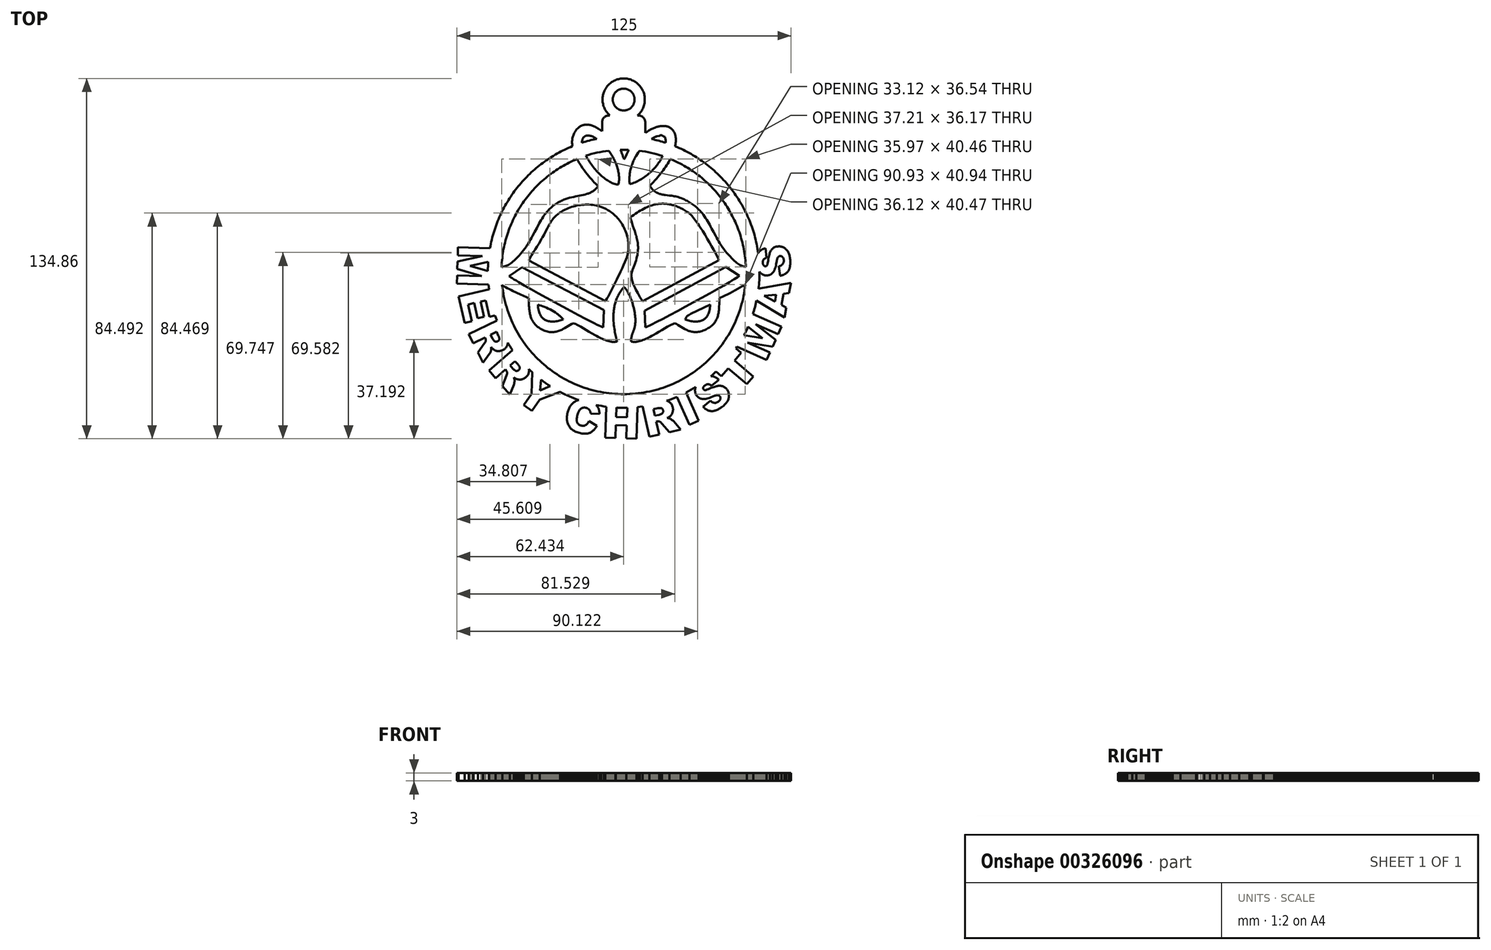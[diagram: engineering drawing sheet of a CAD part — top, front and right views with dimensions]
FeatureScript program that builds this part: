
annotation { "Feature Type Name" : "Feature", "Feature Type Description" : "" }
export const myFeature = defineFeature(function(context is Context, id is Id, definition is map)
    precondition{}
    {
        {
            var Q0;
            Q0=qCreatedBy(makeId("Top.planeOp"),FACE);
            var sketch = newSketch(context, id + "F0", { "sketchPlane" : qUnion([Q0])});
            skLineSegment(sketch, "E0", {"start": v(-50.73, -1.2) * mm, "end": v(-57.52, -2.69) * mm});
            skLineSegment(sketch, "E1", {"start": v(-57.52, -2.69) * mm, "end": v(-50.87, -4.64) * mm});
            skLineSegment(sketch, "E2", {"start": v(-50.87, -4.64) * mm, "end": v(-50.85, -3.77) * mm});
            skLineSegment(sketch, "E3", {"start": v(-50.85, -3.77) * mm, "end": v(-50.83, -2.91) * mm});
            skLineSegment(sketch, "E4", {"start": v(-50.83, -2.91) * mm, "end": v(-50.79, -2.06) * mm});
            skLineSegment(sketch, "E5", {"start": v(-50.79, -2.06) * mm, "end": v(-50.73, -1.2) * mm});
            skLineSegment(sketch, "E6", {"start": v(-0.07, 67.43) * mm, "end": v(0.33, 67.42) * mm});
            skLineSegment(sketch, "E7", {"start": v(0.33, 67.42) * mm, "end": v(0.74, 67.39) * mm});
            skLineSegment(sketch, "E8", {"start": v(0.74, 67.39) * mm, "end": v(1.13, 67.34) * mm});
            skLineSegment(sketch, "E9", {"start": v(1.13, 67.34) * mm, "end": v(1.52, 67.27) * mm});
            skLineSegment(sketch, "E10", {"start": v(1.52, 67.27) * mm, "end": v(1.9, 67.18) * mm});
            skLineSegment(sketch, "E11", {"start": v(1.9, 67.18) * mm, "end": v(2.28, 67.07) * mm});
            skLineSegment(sketch, "E12", {"start": v(2.28, 67.07) * mm, "end": v(2.64, 66.95) * mm});
            skLineSegment(sketch, "E13", {"start": v(2.64, 66.95) * mm, "end": v(3, 66.8) * mm});
            skLineSegment(sketch, "E14", {"start": v(3, 66.8) * mm, "end": v(3.35, 66.65) * mm});
            skLineSegment(sketch, "E15", {"start": v(3.35, 66.65) * mm, "end": v(3.7, 66.47) * mm});
            skLineSegment(sketch, "E16", {"start": v(3.7, 66.47) * mm, "end": v(4.02, 66.28) * mm});
            skLineSegment(sketch, "E17", {"start": v(4.02, 66.28) * mm, "end": v(4.34, 66.08) * mm});
            skLineSegment(sketch, "E18", {"start": v(4.34, 66.08) * mm, "end": v(4.65, 65.86) * mm});
            skLineSegment(sketch, "E19", {"start": v(4.65, 65.86) * mm, "end": v(4.95, 65.62) * mm});
            skLineSegment(sketch, "E20", {"start": v(4.95, 65.62) * mm, "end": v(5.24, 65.38) * mm});
            skLineSegment(sketch, "E21", {"start": v(5.24, 65.38) * mm, "end": v(5.51, 65.11) * mm});
            skLineSegment(sketch, "E22", {"start": v(5.51, 65.11) * mm, "end": v(5.78, 64.84) * mm});
            skLineSegment(sketch, "E23", {"start": v(5.78, 64.84) * mm, "end": v(6.02, 64.55) * mm});
            skLineSegment(sketch, "E24", {"start": v(6.02, 64.55) * mm, "end": v(6.26, 64.25) * mm});
            skLineSegment(sketch, "E25", {"start": v(6.26, 64.25) * mm, "end": v(6.48, 63.94) * mm});
            skLineSegment(sketch, "E26", {"start": v(6.48, 63.94) * mm, "end": v(6.68, 63.62) * mm});
            skLineSegment(sketch, "E27", {"start": v(6.68, 63.62) * mm, "end": v(6.87, 63.3) * mm});
            skLineSegment(sketch, "E28", {"start": v(6.87, 63.3) * mm, "end": v(7.05, 62.95) * mm});
            skLineSegment(sketch, "E29", {"start": v(7.05, 62.95) * mm, "end": v(7.2, 62.6) * mm});
            skLineSegment(sketch, "E30", {"start": v(7.2, 62.6) * mm, "end": v(7.35, 62.24) * mm});
            skLineSegment(sketch, "E31", {"start": v(7.35, 62.24) * mm, "end": v(7.47, 61.88) * mm});
            skLineSegment(sketch, "E32", {"start": v(7.47, 61.88) * mm, "end": v(7.58, 61.5) * mm});
            skLineSegment(sketch, "E33", {"start": v(7.58, 61.5) * mm, "end": v(7.67, 61.12) * mm});
            skLineSegment(sketch, "E34", {"start": v(7.67, 61.12) * mm, "end": v(7.74, 60.73) * mm});
            skLineSegment(sketch, "E35", {"start": v(7.74, 60.73) * mm, "end": v(7.79, 60.33) * mm});
            skLineSegment(sketch, "E36", {"start": v(7.79, 60.33) * mm, "end": v(7.82, 59.93) * mm});
            skLineSegment(sketch, "E37", {"start": v(7.82, 59.93) * mm, "end": v(7.83, 59.53) * mm});
            skLineSegment(sketch, "E38", {"start": v(7.83, 59.53) * mm, "end": v(7.82, 59.09) * mm});
            skLineSegment(sketch, "E39", {"start": v(7.82, 59.09) * mm, "end": v(7.78, 58.65) * mm});
            skLineSegment(sketch, "E40", {"start": v(7.78, 58.65) * mm, "end": v(7.72, 58.22) * mm});
            skLineSegment(sketch, "E41", {"start": v(7.72, 58.22) * mm, "end": v(7.64, 57.8) * mm});
            skLineSegment(sketch, "E42", {"start": v(7.64, 57.8) * mm, "end": v(7.54, 57.39) * mm});
            skLineSegment(sketch, "E43", {"start": v(7.54, 57.39) * mm, "end": v(7.41, 56.99) * mm});
            skLineSegment(sketch, "E44", {"start": v(7.41, 56.99) * mm, "end": v(7.26, 56.6) * mm});
            skLineSegment(sketch, "E45", {"start": v(7.26, 56.6) * mm, "end": v(7.1, 56.2) * mm});
            skLineSegment(sketch, "E46", {"start": v(7.1, 56.2) * mm, "end": v(6.91, 55.83) * mm});
            skLineSegment(sketch, "E47", {"start": v(6.91, 55.83) * mm, "end": v(6.7, 55.47) * mm});
            skLineSegment(sketch, "E48", {"start": v(6.7, 55.47) * mm, "end": v(6.49, 55.12) * mm});
            skLineSegment(sketch, "E49", {"start": v(6.49, 55.12) * mm, "end": v(6.25, 54.79) * mm});
            skLineSegment(sketch, "E50", {"start": v(6.25, 54.79) * mm, "end": v(6, 54.46) * mm});
            skLineSegment(sketch, "E51", {"start": v(6, 54.46) * mm, "end": v(5.72, 54.15) * mm});
            skLineSegment(sketch, "E52", {"start": v(5.72, 54.15) * mm, "end": v(5.43, 53.86) * mm});
            skLineSegment(sketch, "E53", {"start": v(5.43, 53.86) * mm, "end": v(5.13, 53.58) * mm});
            skLineSegment(sketch, "E54", {"start": v(5.13, 53.58) * mm, "end": v(5.46, 53.58) * mm});
            skLineSegment(sketch, "E55", {"start": v(5.46, 53.58) * mm, "end": v(5.72, 53.57) * mm});
            skLineSegment(sketch, "E56", {"start": v(5.72, 53.57) * mm, "end": v(5.97, 53.53) * mm});
            skLineSegment(sketch, "E57", {"start": v(5.97, 53.53) * mm, "end": v(6.22, 53.47) * mm});
            skLineSegment(sketch, "E58", {"start": v(6.22, 53.47) * mm, "end": v(6.45, 53.38) * mm});
            skLineSegment(sketch, "E59", {"start": v(6.45, 53.38) * mm, "end": v(6.67, 53.27) * mm});
            skLineSegment(sketch, "E60", {"start": v(6.67, 53.27) * mm, "end": v(6.88, 53.15) * mm});
            skLineSegment(sketch, "E61", {"start": v(6.88, 53.15) * mm, "end": v(7.08, 53) * mm});
            skLineSegment(sketch, "E62", {"start": v(7.08, 53) * mm, "end": v(7.26, 52.83) * mm});
            skLineSegment(sketch, "E63", {"start": v(7.26, 52.83) * mm, "end": v(7.42, 52.65) * mm});
            skLineSegment(sketch, "E64", {"start": v(7.42, 52.65) * mm, "end": v(7.57, 52.46) * mm});
            skLineSegment(sketch, "E65", {"start": v(7.57, 52.46) * mm, "end": v(7.7, 52.25) * mm});
            skLineSegment(sketch, "E66", {"start": v(7.7, 52.25) * mm, "end": v(7.8, 52.03) * mm});
            skLineSegment(sketch, "E67", {"start": v(7.8, 52.03) * mm, "end": v(7.89, 51.8) * mm});
            skLineSegment(sketch, "E68", {"start": v(7.89, 51.8) * mm, "end": v(7.95, 51.55) * mm});
            skLineSegment(sketch, "E69", {"start": v(7.95, 51.55) * mm, "end": v(8, 51.3) * mm});
            skLineSegment(sketch, "E70", {"start": v(8, 51.3) * mm, "end": v(8, 51.04) * mm});
            skLineSegment(sketch, "E71", {"start": v(8, 51.04) * mm, "end": v(8, 47.03) * mm});
            skLineSegment(sketch, "E72", {"start": v(8, 47.03) * mm, "end": v(8.34, 47.26) * mm});
            skLineSegment(sketch, "E73", {"start": v(8.34, 47.26) * mm, "end": v(8.67, 47.49) * mm});
            skLineSegment(sketch, "E74", {"start": v(8.67, 47.49) * mm, "end": v(9, 47.7) * mm});
            skLineSegment(sketch, "E75", {"start": v(9, 47.7) * mm, "end": v(9.33, 47.9) * mm});
            skLineSegment(sketch, "E76", {"start": v(9.33, 47.9) * mm, "end": v(9.65, 48.1) * mm});
            skLineSegment(sketch, "E77", {"start": v(9.65, 48.1) * mm, "end": v(9.97, 48.27) * mm});
            skLineSegment(sketch, "E78", {"start": v(9.97, 48.27) * mm, "end": v(10.3, 48.44) * mm});
            skLineSegment(sketch, "E79", {"start": v(10.3, 48.44) * mm, "end": v(10.6, 48.6) * mm});
            skLineSegment(sketch, "E80", {"start": v(10.6, 48.6) * mm, "end": v(10.92, 48.74) * mm});
            skLineSegment(sketch, "E81", {"start": v(10.92, 48.74) * mm, "end": v(11.23, 48.87) * mm});
            skLineSegment(sketch, "E82", {"start": v(11.23, 48.87) * mm, "end": v(11.53, 49) * mm});
            skLineSegment(sketch, "E83", {"start": v(11.53, 49) * mm, "end": v(11.83, 49.1) * mm});
            skLineSegment(sketch, "E84", {"start": v(11.83, 49.1) * mm, "end": v(12.13, 49.2) * mm});
            skLineSegment(sketch, "E85", {"start": v(12.13, 49.2) * mm, "end": v(12.42, 49.3) * mm});
            skLineSegment(sketch, "E86", {"start": v(12.42, 49.3) * mm, "end": v(12.71, 49.38) * mm});
            skLineSegment(sketch, "E87", {"start": v(12.71, 49.38) * mm, "end": v(13, 49.45) * mm});
            skLineSegment(sketch, "E88", {"start": v(13, 49.45) * mm, "end": v(13.28, 49.5) * mm});
            skLineSegment(sketch, "E89", {"start": v(13.28, 49.5) * mm, "end": v(13.55, 49.56) * mm});
            skLineSegment(sketch, "E90", {"start": v(13.55, 49.56) * mm, "end": v(13.82, 49.6) * mm});
            skLineSegment(sketch, "E91", {"start": v(13.82, 49.6) * mm, "end": v(14.1, 49.63) * mm});
            skLineSegment(sketch, "E92", {"start": v(14.1, 49.63) * mm, "end": v(14.35, 49.64) * mm});
            skLineSegment(sketch, "E93", {"start": v(14.35, 49.64) * mm, "end": v(14.6, 49.65) * mm});
            skLineSegment(sketch, "E94", {"start": v(14.6, 49.65) * mm, "end": v(14.86, 49.65) * mm});
            skLineSegment(sketch, "E95", {"start": v(14.86, 49.65) * mm, "end": v(15.1, 49.64) * mm});
            skLineSegment(sketch, "E96", {"start": v(15.1, 49.64) * mm, "end": v(15.35, 49.62) * mm});
            skLineSegment(sketch, "E97", {"start": v(15.35, 49.62) * mm, "end": v(15.58, 49.59) * mm});
            skLineSegment(sketch, "E98", {"start": v(15.58, 49.59) * mm, "end": v(15.81, 49.55) * mm});
            skLineSegment(sketch, "E99", {"start": v(15.81, 49.55) * mm, "end": v(16.04, 49.5) * mm});
            skLineSegment(sketch, "E100", {"start": v(16.04, 49.5) * mm, "end": v(16.26, 49.44) * mm});
            skLineSegment(sketch, "E101", {"start": v(16.26, 49.44) * mm, "end": v(16.47, 49.37) * mm});
            skLineSegment(sketch, "E102", {"start": v(16.47, 49.37) * mm, "end": v(16.68, 49.3) * mm});
            skLineSegment(sketch, "E103", {"start": v(16.68, 49.3) * mm, "end": v(16.88, 49.2) * mm});
            skLineSegment(sketch, "E104", {"start": v(16.88, 49.2) * mm, "end": v(17.07, 49.1) * mm});
            skLineSegment(sketch, "E105", {"start": v(17.07, 49.1) * mm, "end": v(17.26, 49) * mm});
            skLineSegment(sketch, "E106", {"start": v(17.26, 49) * mm, "end": v(17.44, 48.89) * mm});
            skLineSegment(sketch, "E107", {"start": v(17.44, 48.89) * mm, "end": v(17.6, 48.77) * mm});
            skLineSegment(sketch, "E108", {"start": v(17.6, 48.77) * mm, "end": v(17.78, 48.63) * mm});
            skLineSegment(sketch, "E109", {"start": v(17.78, 48.63) * mm, "end": v(17.93, 48.5) * mm});
            skLineSegment(sketch, "E110", {"start": v(17.93, 48.5) * mm, "end": v(18.09, 48.34) * mm});
            skLineSegment(sketch, "E111", {"start": v(18.09, 48.34) * mm, "end": v(18.23, 48.19) * mm});
            skLineSegment(sketch, "E112", {"start": v(18.23, 48.19) * mm, "end": v(18.37, 48.02) * mm});
            skLineSegment(sketch, "E113", {"start": v(18.37, 48.02) * mm, "end": v(18.5, 47.85) * mm});
            skLineSegment(sketch, "E114", {"start": v(18.5, 47.85) * mm, "end": v(18.62, 47.66) * mm});
            skLineSegment(sketch, "E115", {"start": v(18.62, 47.66) * mm, "end": v(18.73, 47.47) * mm});
            skLineSegment(sketch, "E116", {"start": v(18.73, 47.47) * mm, "end": v(18.84, 47.27) * mm});
            skLineSegment(sketch, "E117", {"start": v(18.84, 47.27) * mm, "end": v(18.94, 47.06) * mm});
            skLineSegment(sketch, "E118", {"start": v(18.94, 47.06) * mm, "end": v(19.03, 46.85) * mm});
            skLineSegment(sketch, "E119", {"start": v(19.03, 46.85) * mm, "end": v(19.1, 46.62) * mm});
            skLineSegment(sketch, "E120", {"start": v(19.1, 46.62) * mm, "end": v(19.18, 46.4) * mm});
            skLineSegment(sketch, "E121", {"start": v(19.18, 46.4) * mm, "end": v(19.25, 46.15) * mm});
            skLineSegment(sketch, "E122", {"start": v(19.25, 46.15) * mm, "end": v(19.3, 45.9) * mm});
            skLineSegment(sketch, "E123", {"start": v(19.3, 45.9) * mm, "end": v(19.35, 45.65) * mm});
            skLineSegment(sketch, "E124", {"start": v(19.35, 45.65) * mm, "end": v(19.39, 45.4) * mm});
            skLineSegment(sketch, "E125", {"start": v(19.39, 45.4) * mm, "end": v(19.41, 45.12) * mm});
            skLineSegment(sketch, "E126", {"start": v(19.41, 45.12) * mm, "end": v(19.43, 44.85) * mm});
            skLineSegment(sketch, "E127", {"start": v(19.43, 44.85) * mm, "end": v(19.44, 44.56) * mm});
            skLineSegment(sketch, "E128", {"start": v(19.44, 44.56) * mm, "end": v(19.44, 44.27) * mm});
            skLineSegment(sketch, "E129", {"start": v(19.44, 44.27) * mm, "end": v(19.43, 43.97) * mm});
            skLineSegment(sketch, "E130", {"start": v(19.43, 43.97) * mm, "end": v(19.41, 43.67) * mm});
            skLineSegment(sketch, "E131", {"start": v(19.41, 43.67) * mm, "end": v(19.38, 43.36) * mm});
            skLineSegment(sketch, "E132", {"start": v(19.38, 43.36) * mm, "end": v(19.35, 43.04) * mm});
            skLineSegment(sketch, "E133", {"start": v(19.35, 43.04) * mm, "end": v(19.3, 42.71) * mm});
            skLineSegment(sketch, "E134", {"start": v(19.3, 42.71) * mm, "end": v(19.24, 42.38) * mm});
            skLineSegment(sketch, "E135", {"start": v(19.24, 42.38) * mm, "end": v(19.17, 42.04) * mm});
            skLineSegment(sketch, "E136", {"start": v(19.17, 42.04) * mm, "end": v(19.93, 41.72) * mm});
            skLineSegment(sketch, "E137", {"start": v(19.93, 41.72) * mm, "end": v(20.7, 41.39) * mm});
            skLineSegment(sketch, "E138", {"start": v(20.7, 41.39) * mm, "end": v(21.45, 41.04) * mm});
            skLineSegment(sketch, "E139", {"start": v(21.45, 41.04) * mm, "end": v(22.2, 40.68) * mm});
            skLineSegment(sketch, "E140", {"start": v(22.2, 40.68) * mm, "end": v(22.93, 40.31) * mm});
            skLineSegment(sketch, "E141", {"start": v(22.93, 40.31) * mm, "end": v(23.67, 39.93) * mm});
            skLineSegment(sketch, "E142", {"start": v(23.67, 39.93) * mm, "end": v(24.4, 39.54) * mm});
            skLineSegment(sketch, "E143", {"start": v(24.4, 39.54) * mm, "end": v(25.11, 39.14) * mm});
            skLineSegment(sketch, "E144", {"start": v(25.11, 39.14) * mm, "end": v(25.83, 38.72) * mm});
            skLineSegment(sketch, "E145", {"start": v(25.83, 38.72) * mm, "end": v(26.53, 38.3) * mm});
            skLineSegment(sketch, "E146", {"start": v(26.53, 38.3) * mm, "end": v(27.23, 37.86) * mm});
            skLineSegment(sketch, "E147", {"start": v(27.23, 37.86) * mm, "end": v(27.92, 37.41) * mm});
            skLineSegment(sketch, "E148", {"start": v(27.92, 37.41) * mm, "end": v(28.6, 36.95) * mm});
            skLineSegment(sketch, "E149", {"start": v(28.6, 36.95) * mm, "end": v(29.27, 36.48) * mm});
            skLineSegment(sketch, "E150", {"start": v(29.27, 36.48) * mm, "end": v(29.94, 36) * mm});
            skLineSegment(sketch, "E151", {"start": v(29.94, 36) * mm, "end": v(30.6, 35.51) * mm});
            skLineSegment(sketch, "E152", {"start": v(30.6, 35.51) * mm, "end": v(31.25, 35.01) * mm});
            skLineSegment(sketch, "E153", {"start": v(31.25, 35.01) * mm, "end": v(31.89, 34.5) * mm});
            skLineSegment(sketch, "E154", {"start": v(31.89, 34.5) * mm, "end": v(32.52, 33.98) * mm});
            skLineSegment(sketch, "E155", {"start": v(32.52, 33.98) * mm, "end": v(33.14, 33.45) * mm});
            skLineSegment(sketch, "E156", {"start": v(33.14, 33.45) * mm, "end": v(33.76, 32.9) * mm});
            skLineSegment(sketch, "E157", {"start": v(33.76, 32.9) * mm, "end": v(34.36, 32.36) * mm});
            skLineSegment(sketch, "E158", {"start": v(34.36, 32.36) * mm, "end": v(34.96, 31.8) * mm});
            skLineSegment(sketch, "E159", {"start": v(34.96, 31.8) * mm, "end": v(35.55, 31.23) * mm});
            skLineSegment(sketch, "E160", {"start": v(35.55, 31.23) * mm, "end": v(36.13, 30.65) * mm});
            skLineSegment(sketch, "E161", {"start": v(36.13, 30.65) * mm, "end": v(36.7, 30.06) * mm});
            skLineSegment(sketch, "E162", {"start": v(36.7, 30.06) * mm, "end": v(37.26, 29.46) * mm});
            skLineSegment(sketch, "E163", {"start": v(37.26, 29.46) * mm, "end": v(37.8, 28.85) * mm});
            skLineSegment(sketch, "E164", {"start": v(37.8, 28.85) * mm, "end": v(38.35, 28.24) * mm});
            skLineSegment(sketch, "E165", {"start": v(38.35, 28.24) * mm, "end": v(38.88, 27.62) * mm});
            skLineSegment(sketch, "E166", {"start": v(38.88, 27.62) * mm, "end": v(39.4, 26.98) * mm});
            skLineSegment(sketch, "E167", {"start": v(39.4, 26.98) * mm, "end": v(39.91, 26.34) * mm});
            skLineSegment(sketch, "E168", {"start": v(39.91, 26.34) * mm, "end": v(40.42, 25.7) * mm});
            skLineSegment(sketch, "E169", {"start": v(40.42, 25.7) * mm, "end": v(40.9, 25.04) * mm});
            skLineSegment(sketch, "E170", {"start": v(40.9, 25.04) * mm, "end": v(41.39, 24.37) * mm});
            skLineSegment(sketch, "E171", {"start": v(41.39, 24.37) * mm, "end": v(41.86, 23.7) * mm});
            skLineSegment(sketch, "E172", {"start": v(41.86, 23.7) * mm, "end": v(42.32, 23.01) * mm});
            skLineSegment(sketch, "E173", {"start": v(42.32, 23.01) * mm, "end": v(42.76, 22.32) * mm});
            skLineSegment(sketch, "E174", {"start": v(42.76, 22.32) * mm, "end": v(43.2, 21.63) * mm});
            skLineSegment(sketch, "E175", {"start": v(43.2, 21.63) * mm, "end": v(43.63, 20.92) * mm});
            skLineSegment(sketch, "E176", {"start": v(43.63, 20.92) * mm, "end": v(44.04, 20.21) * mm});
            skLineSegment(sketch, "E177", {"start": v(44.04, 20.21) * mm, "end": v(44.45, 19.5) * mm});
            skLineSegment(sketch, "E178", {"start": v(44.45, 19.5) * mm, "end": v(44.84, 18.77) * mm});
            skLineSegment(sketch, "E179", {"start": v(44.84, 18.77) * mm, "end": v(45.22, 18.03) * mm});
            skLineSegment(sketch, "E180", {"start": v(45.22, 18.03) * mm, "end": v(45.59, 17.3) * mm});
            skLineSegment(sketch, "E181", {"start": v(45.59, 17.3) * mm, "end": v(45.95, 16.54) * mm});
            skLineSegment(sketch, "E182", {"start": v(45.95, 16.54) * mm, "end": v(46.3, 15.8) * mm});
            skLineSegment(sketch, "E183", {"start": v(46.3, 15.8) * mm, "end": v(46.63, 15.03) * mm});
            skLineSegment(sketch, "E184", {"start": v(46.63, 15.03) * mm, "end": v(46.95, 14.26) * mm});
            skLineSegment(sketch, "E185", {"start": v(46.95, 14.26) * mm, "end": v(47.26, 13.5) * mm});
            skLineSegment(sketch, "E186", {"start": v(47.26, 13.5) * mm, "end": v(47.56, 12.71) * mm});
            skLineSegment(sketch, "E187", {"start": v(47.56, 12.71) * mm, "end": v(47.84, 11.93) * mm});
            skLineSegment(sketch, "E188", {"start": v(47.84, 11.93) * mm, "end": v(48.11, 11.13) * mm});
            skLineSegment(sketch, "E189", {"start": v(48.11, 11.13) * mm, "end": v(48.37, 10.34) * mm});
            skLineSegment(sketch, "E190", {"start": v(48.37, 10.34) * mm, "end": v(48.62, 9.53) * mm});
            skLineSegment(sketch, "E191", {"start": v(48.62, 9.53) * mm, "end": v(48.85, 8.73) * mm});
            skLineSegment(sketch, "E192", {"start": v(48.85, 8.73) * mm, "end": v(49.07, 7.91) * mm});
            skLineSegment(sketch, "E193", {"start": v(49.07, 7.91) * mm, "end": v(49.28, 7.1) * mm});
            skLineSegment(sketch, "E194", {"start": v(49.28, 7.1) * mm, "end": v(49.47, 6.27) * mm});
            skLineSegment(sketch, "E195", {"start": v(49.47, 6.27) * mm, "end": v(49.65, 5.44) * mm});
            skLineSegment(sketch, "E196", {"start": v(49.65, 5.44) * mm, "end": v(49.82, 4.6) * mm});
            skLineSegment(sketch, "E197", {"start": v(49.82, 4.6) * mm, "end": v(49.97, 3.76) * mm});
            skLineSegment(sketch, "E198", {"start": v(49.97, 3.76) * mm, "end": v(50.11, 2.92) * mm});
            skLineSegment(sketch, "E199", {"start": v(50.11, 2.92) * mm, "end": v(50.24, 2.07) * mm});
            skLineSegment(sketch, "E200", {"start": v(50.24, 2.07) * mm, "end": v(50.3, 2.17) * mm});
            skLineSegment(sketch, "E201", {"start": v(50.3, 2.17) * mm, "end": v(50.4, 2.33) * mm});
            skLineSegment(sketch, "E202", {"start": v(50.4, 2.33) * mm, "end": v(50.5, 2.48) * mm});
            skLineSegment(sketch, "E203", {"start": v(50.5, 2.48) * mm, "end": v(50.62, 2.62) * mm});
            skLineSegment(sketch, "E204", {"start": v(50.62, 2.62) * mm, "end": v(50.75, 2.76) * mm});
            skLineSegment(sketch, "E205", {"start": v(50.75, 2.76) * mm, "end": v(50.88, 2.88) * mm});
            skLineSegment(sketch, "E206", {"start": v(50.88, 2.88) * mm, "end": v(51.03, 3) * mm});
            skLineSegment(sketch, "E207", {"start": v(51.03, 3) * mm, "end": v(51.18, 3.12) * mm});
            skLineSegment(sketch, "E208", {"start": v(51.18, 3.12) * mm, "end": v(51.34, 3.23) * mm});
            skLineSegment(sketch, "E209", {"start": v(51.34, 3.23) * mm, "end": v(51.5, 3.33) * mm});
            skLineSegment(sketch, "E210", {"start": v(51.5, 3.33) * mm, "end": v(51.68, 3.42) * mm});
            skLineSegment(sketch, "E211", {"start": v(51.68, 3.42) * mm, "end": v(51.87, 3.5) * mm});
            skLineSegment(sketch, "E212", {"start": v(51.87, 3.5) * mm, "end": v(52.06, 3.58) * mm});
            skLineSegment(sketch, "E213", {"start": v(52.06, 3.58) * mm, "end": v(52.27, 3.65) * mm});
            skLineSegment(sketch, "E214", {"start": v(52.27, 3.65) * mm, "end": v(52.48, 3.72) * mm});
            skLineSegment(sketch, "E215", {"start": v(52.48, 3.72) * mm, "end": v(52.7, 3.78) * mm});
            skLineSegment(sketch, "E216", {"start": v(52.7, 3.78) * mm, "end": v(52.93, 3.83) * mm});
            skLineSegment(sketch, "E217", {"start": v(52.93, 3.83) * mm, "end": v(53.4, 0.33) * mm});
            skLineSegment(sketch, "E218", {"start": v(53.4, 0.33) * mm, "end": v(53.2, 0.28) * mm});
            skLineSegment(sketch, "E219", {"start": v(53.2, 0.28) * mm, "end": v(53.03, 0.21) * mm});
            skLineSegment(sketch, "E220", {"start": v(53.03, 0.21) * mm, "end": v(52.86, 0.14) * mm});
            skLineSegment(sketch, "E221", {"start": v(52.86, 0.14) * mm, "end": v(52.71, 0.06) * mm});
            skLineSegment(sketch, "E222", {"start": v(52.71, 0.06) * mm, "end": v(52.57, -0.03) * mm});
            skLineSegment(sketch, "E223", {"start": v(52.57, -0.03) * mm, "end": v(52.45, -0.13) * mm});
            skLineSegment(sketch, "E224", {"start": v(52.45, -0.13) * mm, "end": v(52.34, -0.23) * mm});
            skLineSegment(sketch, "E225", {"start": v(52.34, -0.23) * mm, "end": v(52.25, -0.35) * mm});
            skLineSegment(sketch, "E226", {"start": v(52.25, -0.35) * mm, "end": v(52.17, -0.47) * mm});
            skLineSegment(sketch, "E227", {"start": v(52.17, -0.47) * mm, "end": v(52.1, -0.6) * mm});
            skLineSegment(sketch, "E228", {"start": v(52.1, -0.6) * mm, "end": v(52.05, -0.75) * mm});
            skLineSegment(sketch, "E229", {"start": v(52.05, -0.75) * mm, "end": v(52.01, -0.9) * mm});
            skLineSegment(sketch, "E230", {"start": v(52.01, -0.9) * mm, "end": v(51.98, -1.07) * mm});
            skLineSegment(sketch, "E231", {"start": v(51.98, -1.07) * mm, "end": v(51.97, -1.24) * mm});
            skLineSegment(sketch, "E232", {"start": v(51.97, -1.24) * mm, "end": v(51.96, -1.43) * mm});
            skLineSegment(sketch, "E233", {"start": v(51.96, -1.43) * mm, "end": v(51.97, -1.62) * mm});
            skLineSegment(sketch, "E234", {"start": v(51.97, -1.62) * mm, "end": v(51.99, -1.78) * mm});
            skLineSegment(sketch, "E235", {"start": v(51.99, -1.78) * mm, "end": v(52.01, -1.92) * mm});
            skLineSegment(sketch, "E236", {"start": v(52.01, -1.92) * mm, "end": v(52.05, -2.06) * mm});
            skLineSegment(sketch, "E237", {"start": v(52.05, -2.06) * mm, "end": v(52.09, -2.18) * mm});
            skLineSegment(sketch, "E238", {"start": v(52.09, -2.18) * mm, "end": v(52.13, -2.3) * mm});
            skLineSegment(sketch, "E239", {"start": v(52.13, -2.3) * mm, "end": v(52.19, -2.4) * mm});
            skLineSegment(sketch, "E240", {"start": v(52.19, -2.4) * mm, "end": v(52.25, -2.5) * mm});
            skLineSegment(sketch, "E241", {"start": v(52.25, -2.5) * mm, "end": v(52.32, -2.58) * mm});
            skLineSegment(sketch, "E242", {"start": v(52.32, -2.58) * mm, "end": v(52.4, -2.65) * mm});
            skLineSegment(sketch, "E243", {"start": v(52.4, -2.65) * mm, "end": v(52.48, -2.71) * mm});
            skLineSegment(sketch, "E244", {"start": v(52.48, -2.71) * mm, "end": v(52.56, -2.76) * mm});
            skLineSegment(sketch, "E245", {"start": v(52.56, -2.76) * mm, "end": v(52.65, -2.8) * mm});
            skLineSegment(sketch, "E246", {"start": v(52.65, -2.8) * mm, "end": v(52.74, -2.83) * mm});
            skLineSegment(sketch, "E247", {"start": v(52.74, -2.83) * mm, "end": v(52.83, -2.85) * mm});
            skLineSegment(sketch, "E248", {"start": v(52.83, -2.85) * mm, "end": v(52.92, -2.86) * mm});
            skLineSegment(sketch, "E249", {"start": v(52.92, -2.86) * mm, "end": v(53.02, -2.86) * mm});
            skLineSegment(sketch, "E250", {"start": v(53.02, -2.86) * mm, "end": v(53.1, -2.85) * mm});
            skLineSegment(sketch, "E251", {"start": v(53.1, -2.85) * mm, "end": v(53.16, -2.83) * mm});
            skLineSegment(sketch, "E252", {"start": v(53.16, -2.83) * mm, "end": v(53.23, -2.8) * mm});
            skLineSegment(sketch, "E253", {"start": v(53.23, -2.8) * mm, "end": v(53.29, -2.77) * mm});
            skLineSegment(sketch, "E254", {"start": v(53.29, -2.77) * mm, "end": v(53.35, -2.73) * mm});
            skLineSegment(sketch, "E255", {"start": v(53.35, -2.73) * mm, "end": v(53.4, -2.68) * mm});
            skLineSegment(sketch, "E256", {"start": v(53.4, -2.68) * mm, "end": v(53.52, -2.55) * mm});
            skLineSegment(sketch, "E257", {"start": v(53.52, -2.55) * mm, "end": v(53.57, -2.47) * mm});
            skLineSegment(sketch, "E258", {"start": v(53.57, -2.47) * mm, "end": v(53.62, -2.37) * mm});
            skLineSegment(sketch, "E259", {"start": v(53.62, -2.37) * mm, "end": v(53.67, -2.24) * mm});
            skLineSegment(sketch, "E260", {"start": v(53.67, -2.24) * mm, "end": v(53.72, -2.1) * mm});
            skLineSegment(sketch, "E261", {"start": v(53.72, -2.1) * mm, "end": v(53.8, -1.73) * mm});
            skLineSegment(sketch, "E262", {"start": v(53.8, -1.73) * mm, "end": v(53.87, -1.27) * mm});
            skLineSegment(sketch, "E263", {"start": v(53.87, -1.27) * mm, "end": v(53.96, -0.67) * mm});
            skLineSegment(sketch, "E264", {"start": v(53.96, -0.67) * mm, "end": v(54.05, -0.11) * mm});
            skLineSegment(sketch, "E265", {"start": v(54.05, -0.11) * mm, "end": v(54.14, 0.4) * mm});
            skLineSegment(sketch, "E266", {"start": v(54.14, 0.4) * mm, "end": v(54.24, 0.87) * mm});
            skLineSegment(sketch, "E267", {"start": v(54.24, 0.87) * mm, "end": v(54.34, 1.3) * mm});
            skLineSegment(sketch, "E268", {"start": v(54.34, 1.3) * mm, "end": v(54.45, 1.68) * mm});
            skLineSegment(sketch, "E269", {"start": v(54.45, 1.68) * mm, "end": v(54.56, 2.02) * mm});
            skLineSegment(sketch, "E270", {"start": v(54.56, 2.02) * mm, "end": v(54.67, 2.32) * mm});
            skLineSegment(sketch, "E271", {"start": v(54.67, 2.32) * mm, "end": v(54.8, 2.58) * mm});
            skLineSegment(sketch, "E272", {"start": v(54.8, 2.58) * mm, "end": v(54.92, 2.83) * mm});
            skLineSegment(sketch, "E273", {"start": v(54.92, 2.83) * mm, "end": v(55.06, 3.06) * mm});
            skLineSegment(sketch, "E274", {"start": v(55.06, 3.06) * mm, "end": v(55.2, 3.28) * mm});
            skLineSegment(sketch, "E275", {"start": v(55.2, 3.28) * mm, "end": v(55.36, 3.47) * mm});
            skLineSegment(sketch, "E276", {"start": v(55.36, 3.47) * mm, "end": v(55.53, 3.65) * mm});
            skLineSegment(sketch, "E277", {"start": v(55.53, 3.65) * mm, "end": v(55.7, 3.82) * mm});
            skLineSegment(sketch, "E278", {"start": v(55.7, 3.82) * mm, "end": v(55.9, 3.96) * mm});
            skLineSegment(sketch, "E279", {"start": v(55.9, 3.96) * mm, "end": v(56.09, 4.09) * mm});
            skLineSegment(sketch, "E280", {"start": v(56.09, 4.09) * mm, "end": v(56.29, 4.2) * mm});
            skLineSegment(sketch, "E281", {"start": v(56.29, 4.2) * mm, "end": v(56.5, 4.3) * mm});
            skLineSegment(sketch, "E282", {"start": v(56.5, 4.3) * mm, "end": v(56.71, 4.39) * mm});
            skLineSegment(sketch, "E283", {"start": v(56.71, 4.39) * mm, "end": v(56.93, 4.45) * mm});
            skLineSegment(sketch, "E284", {"start": v(56.93, 4.45) * mm, "end": v(57.16, 4.51) * mm});
            skLineSegment(sketch, "E285", {"start": v(57.16, 4.51) * mm, "end": v(57.4, 4.55) * mm});
            skLineSegment(sketch, "E286", {"start": v(57.4, 4.55) * mm, "end": v(57.65, 4.58) * mm});
            skLineSegment(sketch, "E287", {"start": v(57.65, 4.58) * mm, "end": v(57.93, 4.59) * mm});
            skLineSegment(sketch, "E288", {"start": v(57.93, 4.59) * mm, "end": v(58.22, 4.58) * mm});
            skLineSegment(sketch, "E289", {"start": v(58.22, 4.58) * mm, "end": v(58.5, 4.55) * mm});
            skLineSegment(sketch, "E290", {"start": v(58.5, 4.55) * mm, "end": v(58.77, 4.5) * mm});
            skLineSegment(sketch, "E291", {"start": v(58.77, 4.5) * mm, "end": v(59.05, 4.43) * mm});
            skLineSegment(sketch, "E292", {"start": v(59.05, 4.43) * mm, "end": v(59.32, 4.34) * mm});
            skLineSegment(sketch, "E293", {"start": v(59.32, 4.34) * mm, "end": v(59.58, 4.23) * mm});
            skLineSegment(sketch, "E294", {"start": v(59.58, 4.23) * mm, "end": v(59.84, 4.1) * mm});
            skLineSegment(sketch, "E295", {"start": v(59.84, 4.1) * mm, "end": v(60.09, 3.95) * mm});
            skLineSegment(sketch, "E296", {"start": v(60.09, 3.95) * mm, "end": v(60.33, 3.78) * mm});
            skLineSegment(sketch, "E297", {"start": v(60.33, 3.78) * mm, "end": v(60.55, 3.6) * mm});
            skLineSegment(sketch, "E298", {"start": v(60.55, 3.6) * mm, "end": v(60.76, 3.4) * mm});
            skLineSegment(sketch, "E299", {"start": v(60.76, 3.4) * mm, "end": v(60.96, 3.17) * mm});
            skLineSegment(sketch, "E300", {"start": v(60.96, 3.17) * mm, "end": v(61.14, 2.94) * mm});
            skLineSegment(sketch, "E301", {"start": v(61.14, 2.94) * mm, "end": v(61.3, 2.69) * mm});
            skLineSegment(sketch, "E302", {"start": v(61.3, 2.69) * mm, "end": v(61.47, 2.41) * mm});
            skLineSegment(sketch, "E303", {"start": v(61.47, 2.41) * mm, "end": v(61.6, 2.13) * mm});
            skLineSegment(sketch, "E304", {"start": v(61.6, 2.13) * mm, "end": v(61.73, 1.82) * mm});
            skLineSegment(sketch, "E305", {"start": v(61.73, 1.82) * mm, "end": v(61.85, 1.49) * mm});
            skLineSegment(sketch, "E306", {"start": v(61.85, 1.49) * mm, "end": v(61.94, 1.14) * mm});
            skLineSegment(sketch, "E307", {"start": v(61.94, 1.14) * mm, "end": v(62.03, 0.77) * mm});
            skLineSegment(sketch, "E308", {"start": v(62.03, 0.77) * mm, "end": v(62.1, 0.38) * mm});
            skLineSegment(sketch, "E309", {"start": v(62.1, 0.38) * mm, "end": v(62.15, -0.02) * mm});
            skLineSegment(sketch, "E310", {"start": v(62.15, -0.02) * mm, "end": v(62.2, -0.45) * mm});
            skLineSegment(sketch, "E311", {"start": v(62.2, -0.45) * mm, "end": v(62.22, -0.83) * mm});
            skLineSegment(sketch, "E312", {"start": v(62.22, -0.83) * mm, "end": v(62.23, -1.2) * mm});
            skLineSegment(sketch, "E313", {"start": v(62.23, -1.2) * mm, "end": v(62.23, -1.55) * mm});
            skLineSegment(sketch, "E314", {"start": v(62.23, -1.55) * mm, "end": v(62.23, -1.88) * mm});
            skLineSegment(sketch, "E315", {"start": v(62.23, -1.88) * mm, "end": v(62.2, -2.2) * mm});
            skLineSegment(sketch, "E316", {"start": v(62.2, -2.2) * mm, "end": v(62.18, -2.51) * mm});
            skLineSegment(sketch, "E317", {"start": v(62.18, -2.51) * mm, "end": v(62.14, -2.8) * mm});
            skLineSegment(sketch, "E318", {"start": v(62.14, -2.8) * mm, "end": v(62.1, -3.08) * mm});
            skLineSegment(sketch, "E319", {"start": v(62.1, -3.08) * mm, "end": v(62.04, -3.35) * mm});
            skLineSegment(sketch, "E320", {"start": v(62.04, -3.35) * mm, "end": v(61.97, -3.6) * mm});
            skLineSegment(sketch, "E321", {"start": v(61.97, -3.6) * mm, "end": v(61.89, -3.84) * mm});
            skLineSegment(sketch, "E322", {"start": v(61.89, -3.84) * mm, "end": v(61.8, -4.06) * mm});
            skLineSegment(sketch, "E323", {"start": v(61.8, -4.06) * mm, "end": v(61.7, -4.27) * mm});
            skLineSegment(sketch, "E324", {"start": v(61.7, -4.27) * mm, "end": v(61.58, -4.47) * mm});
            skLineSegment(sketch, "E325", {"start": v(61.58, -4.47) * mm, "end": v(61.46, -4.65) * mm});
            skLineSegment(sketch, "E326", {"start": v(61.46, -4.65) * mm, "end": v(61.33, -4.81) * mm});
            skLineSegment(sketch, "E327", {"start": v(61.33, -4.81) * mm, "end": v(61.2, -4.97) * mm});
            skLineSegment(sketch, "E328", {"start": v(61.2, -4.97) * mm, "end": v(61.05, -5.12) * mm});
            skLineSegment(sketch, "E329", {"start": v(61.05, -5.12) * mm, "end": v(60.9, -5.26) * mm});
            skLineSegment(sketch, "E330", {"start": v(60.9, -5.26) * mm, "end": v(60.74, -5.4) * mm});
            skLineSegment(sketch, "E331", {"start": v(60.74, -5.4) * mm, "end": v(60.58, -5.52) * mm});
            skLineSegment(sketch, "E332", {"start": v(60.58, -5.52) * mm, "end": v(60.4, -5.63) * mm});
            skLineSegment(sketch, "E333", {"start": v(60.4, -5.63) * mm, "end": v(60.23, -5.74) * mm});
            skLineSegment(sketch, "E334", {"start": v(60.23, -5.74) * mm, "end": v(60.06, -5.84) * mm});
            skLineSegment(sketch, "E335", {"start": v(60.06, -5.84) * mm, "end": v(59.87, -5.94) * mm});
            skLineSegment(sketch, "E336", {"start": v(59.87, -5.94) * mm, "end": v(59.68, -6.03) * mm});
            skLineSegment(sketch, "E337", {"start": v(59.68, -6.03) * mm, "end": v(59.48, -6.1) * mm});
            skLineSegment(sketch, "E338", {"start": v(59.48, -6.1) * mm, "end": v(59.28, -6.18) * mm});
            skLineSegment(sketch, "E339", {"start": v(59.28, -6.18) * mm, "end": v(59.08, -6.24) * mm});
            skLineSegment(sketch, "E340", {"start": v(59.08, -6.24) * mm, "end": v(58.86, -6.3) * mm});
            skLineSegment(sketch, "E341", {"start": v(58.86, -6.3) * mm, "end": v(58.64, -6.34) * mm});
            skLineSegment(sketch, "E342", {"start": v(58.64, -6.34) * mm, "end": v(58.42, -6.39) * mm});
            skLineSegment(sketch, "E343", {"start": v(58.42, -6.39) * mm, "end": v(57.93, -2.86) * mm});
            skLineSegment(sketch, "E344", {"start": v(57.93, -2.86) * mm, "end": v(58.13, -2.8) * mm});
            skLineSegment(sketch, "E345", {"start": v(58.13, -2.8) * mm, "end": v(58.33, -2.75) * mm});
            skLineSegment(sketch, "E346", {"start": v(58.33, -2.75) * mm, "end": v(58.5, -2.7) * mm});
            skLineSegment(sketch, "E347", {"start": v(58.5, -2.7) * mm, "end": v(58.67, -2.62) * mm});
            skLineSegment(sketch, "E348", {"start": v(58.67, -2.62) * mm, "end": v(58.83, -2.55) * mm});
            skLineSegment(sketch, "E349", {"start": v(58.83, -2.55) * mm, "end": v(58.96, -2.47) * mm});
            skLineSegment(sketch, "E350", {"start": v(58.96, -2.47) * mm, "end": v(59.1, -2.38) * mm});
            skLineSegment(sketch, "E351", {"start": v(59.1, -2.38) * mm, "end": v(59.2, -2.29) * mm});
            skLineSegment(sketch, "E352", {"start": v(59.2, -2.29) * mm, "end": v(59.36, -2.12) * mm});
            skLineSegment(sketch, "E353", {"start": v(59.36, -2.12) * mm, "end": v(59.5, -1.94) * mm});
            skLineSegment(sketch, "E354", {"start": v(59.5, -1.94) * mm, "end": v(59.6, -1.75) * mm});
            skLineSegment(sketch, "E355", {"start": v(59.6, -1.75) * mm, "end": v(59.7, -1.54) * mm});
            skLineSegment(sketch, "E356", {"start": v(59.7, -1.54) * mm, "end": v(59.76, -1.32) * mm});
            skLineSegment(sketch, "E357", {"start": v(59.76, -1.32) * mm, "end": v(59.8, -1.1) * mm});
            skLineSegment(sketch, "E358", {"start": v(59.8, -1.1) * mm, "end": v(59.82, -0.84) * mm});
            skLineSegment(sketch, "E359", {"start": v(59.82, -0.84) * mm, "end": v(59.8, -0.58) * mm});
            skLineSegment(sketch, "E360", {"start": v(59.8, -0.58) * mm, "end": v(59.79, -0.39) * mm});
            skLineSegment(sketch, "E361", {"start": v(59.79, -0.39) * mm, "end": v(59.76, -0.2) * mm});
            skLineSegment(sketch, "E362", {"start": v(59.76, -0.2) * mm, "end": v(59.71, -0.04) * mm});
            skLineSegment(sketch, "E363", {"start": v(59.71, -0.04) * mm, "end": v(59.66, 0.12) * mm});
            skLineSegment(sketch, "E364", {"start": v(59.66, 0.12) * mm, "end": v(59.6, 0.26) * mm});
            skLineSegment(sketch, "E365", {"start": v(59.6, 0.26) * mm, "end": v(59.52, 0.4) * mm});
            skLineSegment(sketch, "E366", {"start": v(59.52, 0.4) * mm, "end": v(59.44, 0.51) * mm});
            skLineSegment(sketch, "E367", {"start": v(59.44, 0.51) * mm, "end": v(59.34, 0.62) * mm});
            skLineSegment(sketch, "E368", {"start": v(59.34, 0.62) * mm, "end": v(59.24, 0.71) * mm});
            skLineSegment(sketch, "E369", {"start": v(59.24, 0.71) * mm, "end": v(59.13, 0.8) * mm});
            skLineSegment(sketch, "E370", {"start": v(59.13, 0.8) * mm, "end": v(59.02, 0.86) * mm});
            skLineSegment(sketch, "E371", {"start": v(59.02, 0.86) * mm, "end": v(58.91, 0.91) * mm});
            skLineSegment(sketch, "E372", {"start": v(58.91, 0.91) * mm, "end": v(58.8, 0.95) * mm});
            skLineSegment(sketch, "E373", {"start": v(58.8, 0.95) * mm, "end": v(58.68, 0.98) * mm});
            skLineSegment(sketch, "E374", {"start": v(58.68, 0.98) * mm, "end": v(58.56, 0.99) * mm});
            skLineSegment(sketch, "E375", {"start": v(58.56, 0.99) * mm, "end": v(58.44, 0.99) * mm});
            skLineSegment(sketch, "E376", {"start": v(58.44, 0.99) * mm, "end": v(58.32, 0.97) * mm});
            skLineSegment(sketch, "E377", {"start": v(58.32, 0.97) * mm, "end": v(58.21, 0.94) * mm});
            skLineSegment(sketch, "E378", {"start": v(58.21, 0.94) * mm, "end": v(58.1, 0.9) * mm});
            skLineSegment(sketch, "E379", {"start": v(58.1, 0.9) * mm, "end": v(58, 0.85) * mm});
            skLineSegment(sketch, "E380", {"start": v(58, 0.85) * mm, "end": v(57.9, 0.79) * mm});
            skLineSegment(sketch, "E381", {"start": v(57.9, 0.79) * mm, "end": v(57.8, 0.7) * mm});
            skLineSegment(sketch, "E382", {"start": v(57.8, 0.7) * mm, "end": v(57.71, 0.62) * mm});
            skLineSegment(sketch, "E383", {"start": v(57.71, 0.62) * mm, "end": v(57.63, 0.51) * mm});
            skLineSegment(sketch, "E384", {"start": v(57.63, 0.51) * mm, "end": v(57.54, 0.39) * mm});
            skLineSegment(sketch, "E385", {"start": v(57.54, 0.39) * mm, "end": v(57.47, 0.23) * mm});
            skLineSegment(sketch, "E386", {"start": v(57.47, 0.23) * mm, "end": v(57.4, 0.03) * mm});
            skLineSegment(sketch, "E387", {"start": v(57.4, 0.03) * mm, "end": v(57.32, -0.2) * mm});
            skLineSegment(sketch, "E388", {"start": v(57.32, -0.2) * mm, "end": v(57.25, -0.46) * mm});
            skLineSegment(sketch, "E389", {"start": v(57.25, -0.46) * mm, "end": v(57.19, -0.75) * mm});
            skLineSegment(sketch, "E390", {"start": v(57.19, -0.75) * mm, "end": v(57.13, -1.08) * mm});
            skLineSegment(sketch, "E391", {"start": v(57.13, -1.08) * mm, "end": v(57.07, -1.45) * mm});
            skLineSegment(sketch, "E392", {"start": v(57.07, -1.45) * mm, "end": v(56.97, -2.05) * mm});
            skLineSegment(sketch, "E393", {"start": v(56.97, -2.05) * mm, "end": v(56.86, -2.6) * mm});
            skLineSegment(sketch, "E394", {"start": v(56.86, -2.6) * mm, "end": v(56.73, -3.13) * mm});
            skLineSegment(sketch, "E395", {"start": v(56.73, -3.13) * mm, "end": v(56.6, -3.6) * mm});
            skLineSegment(sketch, "E396", {"start": v(56.6, -3.6) * mm, "end": v(56.43, -4.03) * mm});
            skLineSegment(sketch, "E397", {"start": v(56.43, -4.03) * mm, "end": v(56.35, -4.23) * mm});
            skLineSegment(sketch, "E398", {"start": v(56.35, -4.23) * mm, "end": v(56.26, -4.42) * mm});
            skLineSegment(sketch, "E399", {"start": v(56.26, -4.42) * mm, "end": v(56.17, -4.6) * mm});
            skLineSegment(sketch, "E400", {"start": v(56.17, -4.6) * mm, "end": v(56.07, -4.76) * mm});
            skLineSegment(sketch, "E401", {"start": v(56.07, -4.76) * mm, "end": v(55.98, -4.91) * mm});
            skLineSegment(sketch, "E402", {"start": v(55.98, -4.91) * mm, "end": v(55.87, -5.06) * mm});
            skLineSegment(sketch, "E403", {"start": v(55.87, -5.06) * mm, "end": v(55.77, -5.2) * mm});
            skLineSegment(sketch, "E404", {"start": v(55.77, -5.2) * mm, "end": v(55.66, -5.32) * mm});
            skLineSegment(sketch, "E405", {"start": v(55.66, -5.32) * mm, "end": v(55.54, -5.45) * mm});
            skLineSegment(sketch, "E406", {"start": v(55.54, -5.45) * mm, "end": v(55.42, -5.56) * mm});
            skLineSegment(sketch, "E407", {"start": v(55.42, -5.56) * mm, "end": v(55.3, -5.66) * mm});
            skLineSegment(sketch, "E408", {"start": v(55.3, -5.66) * mm, "end": v(55.17, -5.76) * mm});
            skLineSegment(sketch, "E409", {"start": v(55.17, -5.76) * mm, "end": v(55.03, -5.85) * mm});
            skLineSegment(sketch, "E410", {"start": v(55.03, -5.85) * mm, "end": v(54.9, -5.93) * mm});
            skLineSegment(sketch, "E411", {"start": v(54.9, -5.93) * mm, "end": v(54.75, -6) * mm});
            skLineSegment(sketch, "E412", {"start": v(54.75, -6) * mm, "end": v(54.6, -6.07) * mm});
            skLineSegment(sketch, "E413", {"start": v(54.6, -6.07) * mm, "end": v(54.45, -6.13) * mm});
            skLineSegment(sketch, "E414", {"start": v(54.45, -6.13) * mm, "end": v(54.3, -6.17) * mm});
            skLineSegment(sketch, "E415", {"start": v(54.3, -6.17) * mm, "end": v(54.13, -6.22) * mm});
            skLineSegment(sketch, "E416", {"start": v(54.13, -6.22) * mm, "end": v(53.97, -6.25) * mm});
            skLineSegment(sketch, "E417", {"start": v(53.97, -6.25) * mm, "end": v(53.8, -6.27) * mm});
            skLineSegment(sketch, "E418", {"start": v(53.8, -6.27) * mm, "end": v(53.62, -6.3) * mm});
            skLineSegment(sketch, "E419", {"start": v(53.62, -6.3) * mm, "end": v(53.4, -6.3) * mm});
            skLineSegment(sketch, "E420", {"start": v(53.4, -6.3) * mm, "end": v(53.16, -6.3) * mm});
            skLineSegment(sketch, "E421", {"start": v(53.16, -6.3) * mm, "end": v(52.94, -6.27) * mm});
            skLineSegment(sketch, "E422", {"start": v(52.94, -6.27) * mm, "end": v(52.7, -6.23) * mm});
            skLineSegment(sketch, "E423", {"start": v(52.7, -6.23) * mm, "end": v(52.49, -6.17) * mm});
            skLineSegment(sketch, "E424", {"start": v(52.49, -6.17) * mm, "end": v(52.26, -6.1) * mm});
            skLineSegment(sketch, "E425", {"start": v(52.26, -6.1) * mm, "end": v(52.04, -6) * mm});
            skLineSegment(sketch, "E426", {"start": v(52.04, -6) * mm, "end": v(51.83, -5.89) * mm});
            skLineSegment(sketch, "E427", {"start": v(51.83, -5.89) * mm, "end": v(51.67, -5.8) * mm});
            skLineSegment(sketch, "E428", {"start": v(51.67, -5.8) * mm, "end": v(51.52, -5.7) * mm});
            skLineSegment(sketch, "E429", {"start": v(51.52, -5.7) * mm, "end": v(51.37, -5.58) * mm});
            skLineSegment(sketch, "E430", {"start": v(51.37, -5.58) * mm, "end": v(51.23, -5.46) * mm});
            skLineSegment(sketch, "E431", {"start": v(51.23, -5.46) * mm, "end": v(51.1, -5.34) * mm});
            skLineSegment(sketch, "E432", {"start": v(51.1, -5.34) * mm, "end": v(50.97, -5.2) * mm});
            skLineSegment(sketch, "E433", {"start": v(50.97, -5.2) * mm, "end": v(50.85, -5.05) * mm});
            skLineSegment(sketch, "E434", {"start": v(50.85, -5.05) * mm, "end": v(50.73, -4.9) * mm});
            skLineSegment(sketch, "E435", {"start": v(50.73, -4.9) * mm, "end": v(50.73, -4.99) * mm});
            skLineSegment(sketch, "E436", {"start": v(50.73, -4.99) * mm, "end": v(50.72, -5.78) * mm});
            skLineSegment(sketch, "E437", {"start": v(50.72, -5.78) * mm, "end": v(50.7, -6.56) * mm});
            skLineSegment(sketch, "E438", {"start": v(50.7, -6.56) * mm, "end": v(50.67, -7.34) * mm});
            skLineSegment(sketch, "E439", {"start": v(50.67, -7.34) * mm, "end": v(50.63, -8.12) * mm});
            skLineSegment(sketch, "E440", {"start": v(50.63, -8.12) * mm, "end": v(50.58, -8.9) * mm});
            skLineSegment(sketch, "E441", {"start": v(50.58, -8.9) * mm, "end": v(50.51, -9.67) * mm});
            skLineSegment(sketch, "E442", {"start": v(50.51, -9.67) * mm, "end": v(50.44, -10.43) * mm});
            skLineSegment(sketch, "E443", {"start": v(50.44, -10.43) * mm, "end": v(50.35, -11.2) * mm});
            skLineSegment(sketch, "E444", {"start": v(50.35, -11.2) * mm, "end": v(62.5, -9.09) * mm});
            skLineSegment(sketch, "E445", {"start": v(62.5, -9.09) * mm, "end": v(61.77, -12.94) * mm});
            skLineSegment(sketch, "E446", {"start": v(61.77, -12.94) * mm, "end": v(59.7, -13.17) * mm});
            skLineSegment(sketch, "E447", {"start": v(59.7, -13.17) * mm, "end": v(58.9, -17.34) * mm});
            skLineSegment(sketch, "E448", {"start": v(58.9, -17.34) * mm, "end": v(60.76, -18.3) * mm});
            skLineSegment(sketch, "E449", {"start": v(60.76, -18.3) * mm, "end": v(60.05, -22.06) * mm});
            skLineSegment(sketch, "E450", {"start": v(60.05, -22.06) * mm, "end": v(49.6, -15.7) * mm});
            skLineSegment(sketch, "E451", {"start": v(49.6, -15.7) * mm, "end": v(49.45, -16.34) * mm});
            skLineSegment(sketch, "E452", {"start": v(49.45, -16.34) * mm, "end": v(49.3, -16.98) * mm});
            skLineSegment(sketch, "E453", {"start": v(49.3, -16.98) * mm, "end": v(49.14, -17.6) * mm});
            skLineSegment(sketch, "E454", {"start": v(49.14, -17.6) * mm, "end": v(48.98, -18.24) * mm});
            skLineSegment(sketch, "E455", {"start": v(48.98, -18.24) * mm, "end": v(48.8, -18.86) * mm});
            skLineSegment(sketch, "E456", {"start": v(48.8, -18.86) * mm, "end": v(48.63, -19.48) * mm});
            skLineSegment(sketch, "E457", {"start": v(48.63, -19.48) * mm, "end": v(48.44, -20.1) * mm});
            skLineSegment(sketch, "E458", {"start": v(48.44, -20.1) * mm, "end": v(48.24, -20.72) * mm});
            skLineSegment(sketch, "E459", {"start": v(48.24, -20.72) * mm, "end": v(58.94, -25.48) * mm});
            skLineSegment(sketch, "E460", {"start": v(58.94, -25.48) * mm, "end": v(57.7, -28.28) * mm});
            skLineSegment(sketch, "E461", {"start": v(57.7, -28.28) * mm, "end": v(49.25, -24.52) * mm});
            skLineSegment(sketch, "E462", {"start": v(49.25, -24.52) * mm, "end": v(56.73, -30.44) * mm});
            skLineSegment(sketch, "E463", {"start": v(56.73, -30.44) * mm, "end": v(55.6, -32.98) * mm});
            skLineSegment(sketch, "E464", {"start": v(55.6, -32.98) * mm, "end": v(46.2, -31.38) * mm});
            skLineSegment(sketch, "E465", {"start": v(46.2, -31.38) * mm, "end": v(54.64, -35.14) * mm});
            skLineSegment(sketch, "E466", {"start": v(54.64, -35.14) * mm, "end": v(53.4, -37.94) * mm});
            skLineSegment(sketch, "E467", {"start": v(53.4, -37.94) * mm, "end": v(42.32, -33) * mm});
            skLineSegment(sketch, "E468", {"start": v(42.32, -33) * mm, "end": v(42.34, -32.95) * mm});
            skLineSegment(sketch, "E469", {"start": v(42.34, -32.95) * mm, "end": v(41.91, -33.6) * mm});
            skLineSegment(sketch, "E470", {"start": v(41.91, -33.6) * mm, "end": v(43.9, -35.28) * mm});
            skLineSegment(sketch, "E471", {"start": v(43.9, -35.28) * mm, "end": v(41.41, -38.2) * mm});
            skLineSegment(sketch, "E472", {"start": v(41.41, -38.2) * mm, "end": v(48.37, -44.1) * mm});
            skLineSegment(sketch, "E473", {"start": v(48.37, -44.1) * mm, "end": v(45.94, -46.95) * mm});
            skLineSegment(sketch, "E474", {"start": v(45.94, -46.95) * mm, "end": v(38.99, -41.04) * mm});
            skLineSegment(sketch, "E475", {"start": v(38.99, -41.04) * mm, "end": v(36.5, -43.96) * mm});
            skLineSegment(sketch, "E476", {"start": v(36.5, -43.96) * mm, "end": v(34.48, -42.23) * mm});
            skLineSegment(sketch, "E477", {"start": v(34.48, -42.23) * mm, "end": v(33.98, -42.68) * mm});
            skLineSegment(sketch, "E478", {"start": v(33.98, -42.68) * mm, "end": v(33.49, -43.12) * mm});
            skLineSegment(sketch, "E479", {"start": v(33.49, -43.12) * mm, "end": v(32.98, -43.56) * mm});
            skLineSegment(sketch, "E480", {"start": v(32.98, -43.56) * mm, "end": v(32.47, -44) * mm});
            skLineSegment(sketch, "E481", {"start": v(32.47, -44) * mm, "end": v(32.68, -43.99) * mm});
            skLineSegment(sketch, "E482", {"start": v(32.68, -43.99) * mm, "end": v(32.87, -44) * mm});
            skLineSegment(sketch, "E483", {"start": v(32.87, -44) * mm, "end": v(33.05, -44) * mm});
            skLineSegment(sketch, "E484", {"start": v(33.05, -44) * mm, "end": v(33.23, -44.03) * mm});
            skLineSegment(sketch, "E485", {"start": v(33.23, -44.03) * mm, "end": v(33.42, -44.07) * mm});
            skLineSegment(sketch, "E486", {"start": v(33.42, -44.07) * mm, "end": v(33.6, -44.12) * mm});
            skLineSegment(sketch, "E487", {"start": v(33.6, -44.12) * mm, "end": v(33.77, -44.17) * mm});
            skLineSegment(sketch, "E488", {"start": v(33.77, -44.17) * mm, "end": v(33.95, -44.24) * mm});
            skLineSegment(sketch, "E489", {"start": v(33.95, -44.24) * mm, "end": v(34.12, -44.32) * mm});
            skLineSegment(sketch, "E490", {"start": v(34.12, -44.32) * mm, "end": v(34.3, -44.42) * mm});
            skLineSegment(sketch, "E491", {"start": v(34.3, -44.42) * mm, "end": v(34.47, -44.52) * mm});
            skLineSegment(sketch, "E492", {"start": v(34.47, -44.52) * mm, "end": v(34.64, -44.63) * mm});
            skLineSegment(sketch, "E493", {"start": v(34.64, -44.63) * mm, "end": v(34.8, -44.76) * mm});
            skLineSegment(sketch, "E494", {"start": v(34.8, -44.76) * mm, "end": v(34.98, -44.9) * mm});
            skLineSegment(sketch, "E495", {"start": v(34.98, -44.9) * mm, "end": v(35.14, -45.04) * mm});
            skLineSegment(sketch, "E496", {"start": v(35.14, -45.04) * mm, "end": v(35.3, -45.2) * mm});
            skLineSegment(sketch, "E497", {"start": v(35.3, -45.2) * mm, "end": v(35.47, -45.37) * mm});
            skLineSegment(sketch, "E498", {"start": v(35.47, -45.37) * mm, "end": v(32.74, -47.6) * mm});
            skLineSegment(sketch, "E499", {"start": v(32.74, -47.6) * mm, "end": v(32.59, -47.46) * mm});
            skLineSegment(sketch, "E500", {"start": v(32.59, -47.46) * mm, "end": v(32.44, -47.34) * mm});
            skLineSegment(sketch, "E501", {"start": v(32.44, -47.34) * mm, "end": v(32.29, -47.24) * mm});
            skLineSegment(sketch, "E502", {"start": v(32.29, -47.24) * mm, "end": v(32.14, -47.15) * mm});
            skLineSegment(sketch, "E503", {"start": v(32.14, -47.15) * mm, "end": v(32, -47.08) * mm});
            skLineSegment(sketch, "E504", {"start": v(32, -47.08) * mm, "end": v(31.85, -47.03) * mm});
            skLineSegment(sketch, "E505", {"start": v(31.85, -47.03) * mm, "end": v(31.7, -47) * mm});
            skLineSegment(sketch, "E506", {"start": v(31.7, -47) * mm, "end": v(31.56, -46.97) * mm});
            skLineSegment(sketch, "E507", {"start": v(31.56, -46.97) * mm, "end": v(31.4, -46.97) * mm});
            skLineSegment(sketch, "E508", {"start": v(31.4, -46.97) * mm, "end": v(31.26, -46.98) * mm});
            skLineSegment(sketch, "E509", {"start": v(31.26, -46.98) * mm, "end": v(31.1, -47.01) * mm});
            skLineSegment(sketch, "E510", {"start": v(31.1, -47.01) * mm, "end": v(30.95, -47.06) * mm});
            skLineSegment(sketch, "E511", {"start": v(30.95, -47.06) * mm, "end": v(30.8, -47.12) * mm});
            skLineSegment(sketch, "E512", {"start": v(30.8, -47.12) * mm, "end": v(30.64, -47.2) * mm});
            skLineSegment(sketch, "E513", {"start": v(30.64, -47.2) * mm, "end": v(30.49, -47.29) * mm});
            skLineSegment(sketch, "E514", {"start": v(30.49, -47.29) * mm, "end": v(30.33, -47.4) * mm});
            skLineSegment(sketch, "E515", {"start": v(30.33, -47.4) * mm, "end": v(30.2, -47.5) * mm});
            skLineSegment(sketch, "E516", {"start": v(30.2, -47.5) * mm, "end": v(30.09, -47.6) * mm});
            skLineSegment(sketch, "E517", {"start": v(30.09, -47.6) * mm, "end": v(29.99, -47.69) * mm});
            skLineSegment(sketch, "E518", {"start": v(29.99, -47.69) * mm, "end": v(29.9, -47.79) * mm});
            skLineSegment(sketch, "E519", {"start": v(29.9, -47.79) * mm, "end": v(29.83, -47.89) * mm});
            skLineSegment(sketch, "E520", {"start": v(29.83, -47.89) * mm, "end": v(29.77, -48) * mm});
            skLineSegment(sketch, "E521", {"start": v(29.77, -48) * mm, "end": v(29.72, -48.1) * mm});
            skLineSegment(sketch, "E522", {"start": v(29.72, -48.1) * mm, "end": v(29.69, -48.2) * mm});
            skLineSegment(sketch, "E523", {"start": v(29.69, -48.2) * mm, "end": v(29.67, -48.3) * mm});
            skLineSegment(sketch, "E524", {"start": v(29.67, -48.3) * mm, "end": v(29.66, -48.4) * mm});
            skLineSegment(sketch, "E525", {"start": v(29.66, -48.4) * mm, "end": v(29.66, -48.5) * mm});
            skLineSegment(sketch, "E526", {"start": v(29.66, -48.5) * mm, "end": v(29.67, -48.6) * mm});
            skLineSegment(sketch, "E527", {"start": v(29.67, -48.6) * mm, "end": v(29.69, -48.68) * mm});
            skLineSegment(sketch, "E528", {"start": v(29.69, -48.68) * mm, "end": v(29.72, -48.77) * mm});
            skLineSegment(sketch, "E529", {"start": v(29.72, -48.77) * mm, "end": v(29.76, -48.86) * mm});
            skLineSegment(sketch, "E530", {"start": v(29.76, -48.86) * mm, "end": v(29.82, -48.94) * mm});
            skLineSegment(sketch, "E531", {"start": v(29.82, -48.94) * mm, "end": v(29.86, -49) * mm});
            skLineSegment(sketch, "E532", {"start": v(29.86, -49) * mm, "end": v(29.91, -49.04) * mm});
            skLineSegment(sketch, "E533", {"start": v(29.91, -49.04) * mm, "end": v(29.97, -49.08) * mm});
            skLineSegment(sketch, "E534", {"start": v(29.97, -49.08) * mm, "end": v(30.03, -49.12) * mm});
            skLineSegment(sketch, "E535", {"start": v(30.03, -49.12) * mm, "end": v(30.1, -49.15) * mm});
            skLineSegment(sketch, "E536", {"start": v(30.1, -49.15) * mm, "end": v(30.17, -49.17) * mm});
            skLineSegment(sketch, "E537", {"start": v(30.17, -49.17) * mm, "end": v(30.34, -49.2) * mm});
            skLineSegment(sketch, "E538", {"start": v(30.34, -49.2) * mm, "end": v(30.44, -49.2) * mm});
            skLineSegment(sketch, "E539", {"start": v(30.44, -49.2) * mm, "end": v(30.55, -49.2) * mm});
            skLineSegment(sketch, "E540", {"start": v(30.55, -49.2) * mm, "end": v(30.68, -49.17) * mm});
            skLineSegment(sketch, "E541", {"start": v(30.68, -49.17) * mm, "end": v(30.83, -49.13) * mm});
            skLineSegment(sketch, "E542", {"start": v(30.83, -49.13) * mm, "end": v(31.19, -49) * mm});
            skLineSegment(sketch, "E543", {"start": v(31.19, -49) * mm, "end": v(31.61, -48.83) * mm});
            skLineSegment(sketch, "E544", {"start": v(31.61, -48.83) * mm, "end": v(32.17, -48.6) * mm});
            skLineSegment(sketch, "E545", {"start": v(32.17, -48.6) * mm, "end": v(32.7, -48.38) * mm});
            skLineSegment(sketch, "E546", {"start": v(32.7, -48.38) * mm, "end": v(33.18, -48.2) * mm});
            skLineSegment(sketch, "E547", {"start": v(33.18, -48.2) * mm, "end": v(33.63, -48.03) * mm});
            skLineSegment(sketch, "E548", {"start": v(33.63, -48.03) * mm, "end": v(34.05, -47.9) * mm});
            skLineSegment(sketch, "E549", {"start": v(34.05, -47.9) * mm, "end": v(34.43, -47.78) * mm});
            skLineSegment(sketch, "E550", {"start": v(34.43, -47.78) * mm, "end": v(34.78, -47.7) * mm});
            skLineSegment(sketch, "E551", {"start": v(34.78, -47.7) * mm, "end": v(35.09, -47.64) * mm});
            skLineSegment(sketch, "E552", {"start": v(35.09, -47.64) * mm, "end": v(35.38, -47.6) * mm});
            skLineSegment(sketch, "E553", {"start": v(35.38, -47.6) * mm, "end": v(35.66, -47.59) * mm});
            skLineSegment(sketch, "E554", {"start": v(35.66, -47.59) * mm, "end": v(35.93, -47.58) * mm});
            skLineSegment(sketch, "E555", {"start": v(35.93, -47.58) * mm, "end": v(36.19, -47.6) * mm});
            skLineSegment(sketch, "E556", {"start": v(36.19, -47.6) * mm, "end": v(36.44, -47.63) * mm});
            skLineSegment(sketch, "E557", {"start": v(36.44, -47.63) * mm, "end": v(36.68, -47.68) * mm});
            skLineSegment(sketch, "E558", {"start": v(36.68, -47.68) * mm, "end": v(36.9, -47.74) * mm});
            skLineSegment(sketch, "E559", {"start": v(36.9, -47.74) * mm, "end": v(37.13, -47.83) * mm});
            skLineSegment(sketch, "E560", {"start": v(37.13, -47.83) * mm, "end": v(37.34, -47.92) * mm});
            skLineSegment(sketch, "E561", {"start": v(37.34, -47.92) * mm, "end": v(37.54, -48.04) * mm});
            skLineSegment(sketch, "E562", {"start": v(37.54, -48.04) * mm, "end": v(37.74, -48.16) * mm});
            skLineSegment(sketch, "E563", {"start": v(37.74, -48.16) * mm, "end": v(37.92, -48.3) * mm});
            skLineSegment(sketch, "E564", {"start": v(37.92, -48.3) * mm, "end": v(38.1, -48.46) * mm});
            skLineSegment(sketch, "E565", {"start": v(38.1, -48.46) * mm, "end": v(38.26, -48.62) * mm});
            skLineSegment(sketch, "E566", {"start": v(38.26, -48.62) * mm, "end": v(38.42, -48.8) * mm});
            skLineSegment(sketch, "E567", {"start": v(38.42, -48.8) * mm, "end": v(38.57, -49) * mm});
            skLineSegment(sketch, "E568", {"start": v(38.57, -49) * mm, "end": v(38.73, -49.24) * mm});
            skLineSegment(sketch, "E569", {"start": v(38.73, -49.24) * mm, "end": v(38.87, -49.49) * mm});
            skLineSegment(sketch, "E570", {"start": v(38.87, -49.49) * mm, "end": v(39, -49.74) * mm});
            skLineSegment(sketch, "E571", {"start": v(39, -49.74) * mm, "end": v(39.1, -50) * mm});
            skLineSegment(sketch, "E572", {"start": v(39.1, -50) * mm, "end": v(39.18, -50.27) * mm});
            skLineSegment(sketch, "E573", {"start": v(39.18, -50.27) * mm, "end": v(39.24, -50.55) * mm});
            skLineSegment(sketch, "E574", {"start": v(39.24, -50.55) * mm, "end": v(39.29, -50.83) * mm});
            skLineSegment(sketch, "E575", {"start": v(39.29, -50.83) * mm, "end": v(39.3, -51.12) * mm});
            skLineSegment(sketch, "E576", {"start": v(39.3, -51.12) * mm, "end": v(39.31, -51.41) * mm});
            skLineSegment(sketch, "E577", {"start": v(39.31, -51.41) * mm, "end": v(39.3, -51.7) * mm});
            skLineSegment(sketch, "E578", {"start": v(39.3, -51.7) * mm, "end": v(39.25, -51.99) * mm});
            skLineSegment(sketch, "E579", {"start": v(39.25, -51.99) * mm, "end": v(39.19, -52.27) * mm});
            skLineSegment(sketch, "E580", {"start": v(39.19, -52.27) * mm, "end": v(39.1, -52.56) * mm});
            skLineSegment(sketch, "E581", {"start": v(39.1, -52.56) * mm, "end": v(39, -52.83) * mm});
            skLineSegment(sketch, "E582", {"start": v(39, -52.83) * mm, "end": v(38.87, -53.11) * mm});
            skLineSegment(sketch, "E583", {"start": v(38.87, -53.11) * mm, "end": v(38.72, -53.39) * mm});
            skLineSegment(sketch, "E584", {"start": v(38.72, -53.39) * mm, "end": v(38.55, -53.66) * mm});
            skLineSegment(sketch, "E585", {"start": v(38.55, -53.66) * mm, "end": v(38.35, -53.93) * mm});
            skLineSegment(sketch, "E586", {"start": v(38.35, -53.93) * mm, "end": v(38.13, -54.2) * mm});
            skLineSegment(sketch, "E587", {"start": v(38.13, -54.2) * mm, "end": v(37.89, -54.46) * mm});
            skLineSegment(sketch, "E588", {"start": v(37.89, -54.46) * mm, "end": v(37.62, -54.72) * mm});
            skLineSegment(sketch, "E589", {"start": v(37.62, -54.72) * mm, "end": v(37.32, -54.99) * mm});
            skLineSegment(sketch, "E590", {"start": v(37.32, -54.99) * mm, "end": v(37, -55.25) * mm});
            skLineSegment(sketch, "E591", {"start": v(37, -55.25) * mm, "end": v(36.66, -55.5) * mm});
            skLineSegment(sketch, "E592", {"start": v(36.66, -55.5) * mm, "end": v(36.35, -55.72) * mm});
            skLineSegment(sketch, "E593", {"start": v(36.35, -55.72) * mm, "end": v(36.04, -55.92) * mm});
            skLineSegment(sketch, "E594", {"start": v(36.04, -55.92) * mm, "end": v(35.75, -56.1) * mm});
            skLineSegment(sketch, "E595", {"start": v(35.75, -56.1) * mm, "end": v(35.46, -56.28) * mm});
            skLineSegment(sketch, "E596", {"start": v(35.46, -56.28) * mm, "end": v(35.17, -56.43) * mm});
            skLineSegment(sketch, "E597", {"start": v(35.17, -56.43) * mm, "end": v(34.9, -56.57) * mm});
            skLineSegment(sketch, "E598", {"start": v(34.9, -56.57) * mm, "end": v(34.62, -56.69) * mm});
            skLineSegment(sketch, "E599", {"start": v(34.62, -56.69) * mm, "end": v(34.36, -56.8) * mm});
            skLineSegment(sketch, "E600", {"start": v(34.36, -56.8) * mm, "end": v(34.1, -56.88) * mm});
            skLineSegment(sketch, "E601", {"start": v(34.1, -56.88) * mm, "end": v(33.85, -56.95) * mm});
            skLineSegment(sketch, "E602", {"start": v(33.85, -56.95) * mm, "end": v(33.6, -57.01) * mm});
            skLineSegment(sketch, "E603", {"start": v(33.6, -57.01) * mm, "end": v(33.37, -57.05) * mm});
            skLineSegment(sketch, "E604", {"start": v(33.37, -57.05) * mm, "end": v(33.14, -57.07) * mm});
            skLineSegment(sketch, "E605", {"start": v(33.14, -57.07) * mm, "end": v(32.92, -57.08) * mm});
            skLineSegment(sketch, "E606", {"start": v(32.92, -57.08) * mm, "end": v(32.7, -57.07) * mm});
            skLineSegment(sketch, "E607", {"start": v(32.7, -57.07) * mm, "end": v(32.49, -57.05) * mm});
            skLineSegment(sketch, "E608", {"start": v(32.49, -57.05) * mm, "end": v(32.28, -57) * mm});
            skLineSegment(sketch, "E609", {"start": v(32.28, -57) * mm, "end": v(32.08, -56.96) * mm});
            skLineSegment(sketch, "E610", {"start": v(32.08, -56.96) * mm, "end": v(31.88, -56.9) * mm});
            skLineSegment(sketch, "E611", {"start": v(31.88, -56.9) * mm, "end": v(31.69, -56.84) * mm});
            skLineSegment(sketch, "E612", {"start": v(31.69, -56.84) * mm, "end": v(31.5, -56.77) * mm});
            skLineSegment(sketch, "E613", {"start": v(31.5, -56.77) * mm, "end": v(31.3, -56.69) * mm});
            skLineSegment(sketch, "E614", {"start": v(31.3, -56.69) * mm, "end": v(31.12, -56.6) * mm});
            skLineSegment(sketch, "E615", {"start": v(31.12, -56.6) * mm, "end": v(30.94, -56.5) * mm});
            skLineSegment(sketch, "E616", {"start": v(30.94, -56.5) * mm, "end": v(30.77, -56.39) * mm});
            skLineSegment(sketch, "E617", {"start": v(30.77, -56.39) * mm, "end": v(30.6, -56.27) * mm});
            skLineSegment(sketch, "E618", {"start": v(30.6, -56.27) * mm, "end": v(30.42, -56.14) * mm});
            skLineSegment(sketch, "E619", {"start": v(30.42, -56.14) * mm, "end": v(30.26, -56.01) * mm});
            skLineSegment(sketch, "E620", {"start": v(30.26, -56.01) * mm, "end": v(30.1, -55.87) * mm});
            skLineSegment(sketch, "E621", {"start": v(30.1, -55.87) * mm, "end": v(29.93, -55.71) * mm});
            skLineSegment(sketch, "E622", {"start": v(29.93, -55.71) * mm, "end": v(29.78, -55.55) * mm});
            skLineSegment(sketch, "E623", {"start": v(29.78, -55.55) * mm, "end": v(29.63, -55.38) * mm});
            skLineSegment(sketch, "E624", {"start": v(29.63, -55.38) * mm, "end": v(32.38, -53.12) * mm});
            skLineSegment(sketch, "E625", {"start": v(32.38, -53.12) * mm, "end": v(32.53, -53.27) * mm});
            skLineSegment(sketch, "E626", {"start": v(32.53, -53.27) * mm, "end": v(32.68, -53.4) * mm});
            skLineSegment(sketch, "E627", {"start": v(32.68, -53.4) * mm, "end": v(32.82, -53.53) * mm});
            skLineSegment(sketch, "E628", {"start": v(32.82, -53.53) * mm, "end": v(32.97, -53.64) * mm});
            skLineSegment(sketch, "E629", {"start": v(32.97, -53.64) * mm, "end": v(33.11, -53.73) * mm});
            skLineSegment(sketch, "E630", {"start": v(33.11, -53.73) * mm, "end": v(33.25, -53.8) * mm});
            skLineSegment(sketch, "E631", {"start": v(33.25, -53.8) * mm, "end": v(33.4, -53.86) * mm});
            skLineSegment(sketch, "E632", {"start": v(33.4, -53.86) * mm, "end": v(33.53, -53.91) * mm});
            skLineSegment(sketch, "E633", {"start": v(33.53, -53.91) * mm, "end": v(33.76, -53.96) * mm});
            skLineSegment(sketch, "E634", {"start": v(33.76, -53.96) * mm, "end": v(33.98, -53.98) * mm});
            skLineSegment(sketch, "E635", {"start": v(33.98, -53.98) * mm, "end": v(34.2, -53.98) * mm});
            skLineSegment(sketch, "E636", {"start": v(34.2, -53.98) * mm, "end": v(34.42, -53.94) * mm});
            skLineSegment(sketch, "E637", {"start": v(34.42, -53.94) * mm, "end": v(34.64, -53.88) * mm});
            skLineSegment(sketch, "E638", {"start": v(34.64, -53.88) * mm, "end": v(34.86, -53.8) * mm});
            skLineSegment(sketch, "E639", {"start": v(34.86, -53.8) * mm, "end": v(35.08, -53.68) * mm});
            skLineSegment(sketch, "E640", {"start": v(35.08, -53.68) * mm, "end": v(35.3, -53.54) * mm});
            skLineSegment(sketch, "E641", {"start": v(35.3, -53.54) * mm, "end": v(35.46, -53.42) * mm});
            skLineSegment(sketch, "E642", {"start": v(35.46, -53.42) * mm, "end": v(35.6, -53.3) * mm});
            skLineSegment(sketch, "E643", {"start": v(35.6, -53.3) * mm, "end": v(35.72, -53.17) * mm});
            skLineSegment(sketch, "E644", {"start": v(35.72, -53.17) * mm, "end": v(35.82, -53.05) * mm});
            skLineSegment(sketch, "E645", {"start": v(35.82, -53.05) * mm, "end": v(35.91, -52.92) * mm});
            skLineSegment(sketch, "E646", {"start": v(35.91, -52.92) * mm, "end": v(35.98, -52.78) * mm});
            skLineSegment(sketch, "E647", {"start": v(35.98, -52.78) * mm, "end": v(36.04, -52.65) * mm});
            skLineSegment(sketch, "E648", {"start": v(36.04, -52.65) * mm, "end": v(36.08, -52.51) * mm});
            skLineSegment(sketch, "E649", {"start": v(36.08, -52.51) * mm, "end": v(36.1, -52.37) * mm});
            skLineSegment(sketch, "E650", {"start": v(36.1, -52.37) * mm, "end": v(36.12, -52.24) * mm});
            skLineSegment(sketch, "E651", {"start": v(36.12, -52.24) * mm, "end": v(36.12, -52.11) * mm});
            skLineSegment(sketch, "E652", {"start": v(36.12, -52.11) * mm, "end": v(36.1, -52) * mm});
            skLineSegment(sketch, "E653", {"start": v(36.1, -52) * mm, "end": v(36.08, -51.87) * mm});
            skLineSegment(sketch, "E654", {"start": v(36.08, -51.87) * mm, "end": v(36.04, -51.76) * mm});
            skLineSegment(sketch, "E655", {"start": v(36.04, -51.76) * mm, "end": v(35.99, -51.65) * mm});
            skLineSegment(sketch, "E656", {"start": v(35.99, -51.65) * mm, "end": v(35.92, -51.55) * mm});
            skLineSegment(sketch, "E657", {"start": v(35.92, -51.55) * mm, "end": v(35.85, -51.46) * mm});
            skLineSegment(sketch, "E658", {"start": v(35.85, -51.46) * mm, "end": v(35.77, -51.38) * mm});
            skLineSegment(sketch, "E659", {"start": v(35.77, -51.38) * mm, "end": v(35.68, -51.3) * mm});
            skLineSegment(sketch, "E660", {"start": v(35.68, -51.3) * mm, "end": v(35.58, -51.25) * mm});
            skLineSegment(sketch, "E661", {"start": v(35.58, -51.25) * mm, "end": v(35.47, -51.2) * mm});
            skLineSegment(sketch, "E662", {"start": v(35.47, -51.2) * mm, "end": v(35.36, -51.16) * mm});
            skLineSegment(sketch, "E663", {"start": v(35.36, -51.16) * mm, "end": v(35.23, -51.13) * mm});
            skLineSegment(sketch, "E664", {"start": v(35.23, -51.13) * mm, "end": v(35.1, -51.1) * mm});
            skLineSegment(sketch, "E665", {"start": v(35.1, -51.1) * mm, "end": v(34.95, -51.1) * mm});
            skLineSegment(sketch, "E666", {"start": v(34.95, -51.1) * mm, "end": v(34.77, -51.12) * mm});
            skLineSegment(sketch, "E667", {"start": v(34.77, -51.12) * mm, "end": v(34.56, -51.15) * mm});
            skLineSegment(sketch, "E668", {"start": v(34.56, -51.15) * mm, "end": v(34.33, -51.21) * mm});
            skLineSegment(sketch, "E669", {"start": v(34.33, -51.21) * mm, "end": v(34.07, -51.3) * mm});
            skLineSegment(sketch, "E670", {"start": v(34.07, -51.3) * mm, "end": v(33.79, -51.4) * mm});
            skLineSegment(sketch, "E671", {"start": v(33.79, -51.4) * mm, "end": v(33.47, -51.51) * mm});
            skLineSegment(sketch, "E672", {"start": v(33.47, -51.51) * mm, "end": v(33.13, -51.66) * mm});
            skLineSegment(sketch, "E673", {"start": v(33.13, -51.66) * mm, "end": v(32.57, -51.89) * mm});
            skLineSegment(sketch, "E674", {"start": v(32.57, -51.89) * mm, "end": v(32.03, -52.08) * mm});
            skLineSegment(sketch, "E675", {"start": v(32.03, -52.08) * mm, "end": v(31.53, -52.24) * mm});
            skLineSegment(sketch, "E676", {"start": v(31.53, -52.24) * mm, "end": v(31.05, -52.37) * mm});
            skLineSegment(sketch, "E677", {"start": v(31.05, -52.37) * mm, "end": v(30.6, -52.46) * mm});
            skLineSegment(sketch, "E678", {"start": v(30.6, -52.46) * mm, "end": v(30.39, -52.5) * mm});
            skLineSegment(sketch, "E679", {"start": v(30.39, -52.5) * mm, "end": v(30.18, -52.51) * mm});
            skLineSegment(sketch, "E680", {"start": v(30.18, -52.51) * mm, "end": v(29.98, -52.53) * mm});
            skLineSegment(sketch, "E681", {"start": v(29.98, -52.53) * mm, "end": v(29.79, -52.53) * mm});
            skLineSegment(sketch, "E682", {"start": v(29.79, -52.53) * mm, "end": v(29.6, -52.53) * mm});
            skLineSegment(sketch, "E683", {"start": v(29.6, -52.53) * mm, "end": v(29.43, -52.52) * mm});
            skLineSegment(sketch, "E684", {"start": v(29.43, -52.52) * mm, "end": v(29.26, -52.5) * mm});
            skLineSegment(sketch, "E685", {"start": v(29.26, -52.5) * mm, "end": v(29.09, -52.47) * mm});
            skLineSegment(sketch, "E686", {"start": v(29.09, -52.47) * mm, "end": v(28.92, -52.44) * mm});
            skLineSegment(sketch, "E687", {"start": v(28.92, -52.44) * mm, "end": v(28.77, -52.4) * mm});
            skLineSegment(sketch, "E688", {"start": v(28.77, -52.4) * mm, "end": v(28.61, -52.34) * mm});
            skLineSegment(sketch, "E689", {"start": v(28.61, -52.34) * mm, "end": v(28.46, -52.28) * mm});
            skLineSegment(sketch, "E690", {"start": v(28.46, -52.28) * mm, "end": v(28.32, -52.22) * mm});
            skLineSegment(sketch, "E691", {"start": v(28.32, -52.22) * mm, "end": v(28.17, -52.14) * mm});
            skLineSegment(sketch, "E692", {"start": v(28.17, -52.14) * mm, "end": v(28.04, -52.06) * mm});
            skLineSegment(sketch, "E693", {"start": v(28.04, -52.06) * mm, "end": v(27.9, -51.96) * mm});
            skLineSegment(sketch, "E694", {"start": v(27.9, -51.96) * mm, "end": v(27.78, -51.86) * mm});
            skLineSegment(sketch, "E695", {"start": v(27.78, -51.86) * mm, "end": v(27.65, -51.76) * mm});
            skLineSegment(sketch, "E696", {"start": v(27.65, -51.76) * mm, "end": v(27.53, -51.64) * mm});
            skLineSegment(sketch, "E697", {"start": v(27.53, -51.64) * mm, "end": v(27.42, -51.52) * mm});
            skLineSegment(sketch, "E698", {"start": v(27.42, -51.52) * mm, "end": v(27.3, -51.39) * mm});
            skLineSegment(sketch, "E699", {"start": v(27.3, -51.39) * mm, "end": v(27.2, -51.24) * mm});
            skLineSegment(sketch, "E700", {"start": v(27.2, -51.24) * mm, "end": v(27.07, -51.05) * mm});
            skLineSegment(sketch, "E701", {"start": v(27.07, -51.05) * mm, "end": v(26.96, -50.85) * mm});
            skLineSegment(sketch, "E702", {"start": v(26.96, -50.85) * mm, "end": v(26.86, -50.65) * mm});
            skLineSegment(sketch, "E703", {"start": v(26.86, -50.65) * mm, "end": v(26.78, -50.43) * mm});
            skLineSegment(sketch, "E704", {"start": v(26.78, -50.43) * mm, "end": v(26.71, -50.2) * mm});
            skLineSegment(sketch, "E705", {"start": v(26.71, -50.2) * mm, "end": v(26.66, -49.98) * mm});
            skLineSegment(sketch, "E706", {"start": v(26.66, -49.98) * mm, "end": v(26.63, -49.74) * mm});
            skLineSegment(sketch, "E707", {"start": v(26.63, -49.74) * mm, "end": v(26.6, -49.5) * mm});
            skLineSegment(sketch, "E708", {"start": v(26.6, -49.5) * mm, "end": v(26.6, -49.32) * mm});
            skLineSegment(sketch, "E709", {"start": v(26.6, -49.32) * mm, "end": v(26.61, -49.14) * mm});
            skLineSegment(sketch, "E710", {"start": v(26.61, -49.14) * mm, "end": v(26.63, -48.96) * mm});
            skLineSegment(sketch, "E711", {"start": v(26.63, -48.96) * mm, "end": v(26.66, -48.78) * mm});
            skLineSegment(sketch, "E712", {"start": v(26.66, -48.78) * mm, "end": v(26.7, -48.6) * mm});
            skLineSegment(sketch, "E713", {"start": v(26.7, -48.6) * mm, "end": v(26.75, -48.42) * mm});
            skLineSegment(sketch, "E714", {"start": v(26.75, -48.42) * mm, "end": v(26.8, -48.24) * mm});
            skLineSegment(sketch, "E715", {"start": v(26.8, -48.24) * mm, "end": v(26.88, -48.05) * mm});
            skLineSegment(sketch, "E716", {"start": v(26.88, -48.05) * mm, "end": v(25.99, -48.6) * mm});
            skLineSegment(sketch, "E717", {"start": v(25.99, -48.6) * mm, "end": v(25.08, -49.13) * mm});
            skLineSegment(sketch, "E718", {"start": v(25.08, -49.13) * mm, "end": v(24.17, -49.64) * mm});
            skLineSegment(sketch, "E719", {"start": v(24.17, -49.64) * mm, "end": v(23.24, -50.13) * mm});
            skLineSegment(sketch, "E720", {"start": v(23.24, -50.13) * mm, "end": v(27.98, -60.6) * mm});
            skLineSegment(sketch, "E721", {"start": v(27.98, -60.6) * mm, "end": v(24.56, -62.16) * mm});
            skLineSegment(sketch, "E722", {"start": v(24.56, -62.16) * mm, "end": v(19.84, -51.73) * mm});
            skLineSegment(sketch, "E723", {"start": v(19.84, -51.73) * mm, "end": v(18.9, -52.12) * mm});
            skLineSegment(sketch, "E724", {"start": v(18.9, -52.12) * mm, "end": v(17.95, -52.5) * mm});
            skLineSegment(sketch, "E725", {"start": v(17.95, -52.5) * mm, "end": v(17, -52.85) * mm});
            skLineSegment(sketch, "E726", {"start": v(17, -52.85) * mm, "end": v(16.03, -53.18) * mm});
            skLineSegment(sketch, "E727", {"start": v(16.03, -53.18) * mm, "end": v(16.2, -53.23) * mm});
            skLineSegment(sketch, "E728", {"start": v(16.2, -53.23) * mm, "end": v(16.37, -53.29) * mm});
            skLineSegment(sketch, "E729", {"start": v(16.37, -53.29) * mm, "end": v(16.53, -53.36) * mm});
            skLineSegment(sketch, "E730", {"start": v(16.53, -53.36) * mm, "end": v(16.69, -53.43) * mm});
            skLineSegment(sketch, "E731", {"start": v(16.69, -53.43) * mm, "end": v(16.84, -53.52) * mm});
            skLineSegment(sketch, "E732", {"start": v(16.84, -53.52) * mm, "end": v(17, -53.62) * mm});
            skLineSegment(sketch, "E733", {"start": v(17, -53.62) * mm, "end": v(17.14, -53.73) * mm});
            skLineSegment(sketch, "E734", {"start": v(17.14, -53.73) * mm, "end": v(17.28, -53.85) * mm});
            skLineSegment(sketch, "E735", {"start": v(17.28, -53.85) * mm, "end": v(17.46, -54.03) * mm});
            skLineSegment(sketch, "E736", {"start": v(17.46, -54.03) * mm, "end": v(17.62, -54.21) * mm});
            skLineSegment(sketch, "E737", {"start": v(17.62, -54.21) * mm, "end": v(17.76, -54.42) * mm});
            skLineSegment(sketch, "E738", {"start": v(17.76, -54.42) * mm, "end": v(17.9, -54.63) * mm});
            skLineSegment(sketch, "E739", {"start": v(17.9, -54.63) * mm, "end": v(18, -54.86) * mm});
            skLineSegment(sketch, "E740", {"start": v(18, -54.86) * mm, "end": v(18.11, -55.11) * mm});
            skLineSegment(sketch, "E741", {"start": v(18.11, -55.11) * mm, "end": v(18.2, -55.37) * mm});
            skLineSegment(sketch, "E742", {"start": v(18.2, -55.37) * mm, "end": v(18.27, -55.65) * mm});
            skLineSegment(sketch, "E743", {"start": v(18.27, -55.65) * mm, "end": v(18.32, -55.89) * mm});
            skLineSegment(sketch, "E744", {"start": v(18.32, -55.89) * mm, "end": v(18.35, -56.13) * mm});
            skLineSegment(sketch, "E745", {"start": v(18.35, -56.13) * mm, "end": v(18.37, -56.36) * mm});
            skLineSegment(sketch, "E746", {"start": v(18.37, -56.36) * mm, "end": v(18.38, -56.59) * mm});
            skLineSegment(sketch, "E747", {"start": v(18.38, -56.59) * mm, "end": v(18.37, -56.8) * mm});
            skLineSegment(sketch, "E748", {"start": v(18.37, -56.8) * mm, "end": v(18.34, -57.02) * mm});
            skLineSegment(sketch, "E749", {"start": v(18.34, -57.02) * mm, "end": v(18.3, -57.24) * mm});
            skLineSegment(sketch, "E750", {"start": v(18.3, -57.24) * mm, "end": v(18.24, -57.44) * mm});
            skLineSegment(sketch, "E751", {"start": v(18.24, -57.44) * mm, "end": v(18.17, -57.64) * mm});
            skLineSegment(sketch, "E752", {"start": v(18.17, -57.64) * mm, "end": v(18.1, -57.83) * mm});
            skLineSegment(sketch, "E753", {"start": v(18.1, -57.83) * mm, "end": v(18, -58.02) * mm});
            skLineSegment(sketch, "E754", {"start": v(18, -58.02) * mm, "end": v(17.9, -58.2) * mm});
            skLineSegment(sketch, "E755", {"start": v(17.9, -58.2) * mm, "end": v(17.78, -58.38) * mm});
            skLineSegment(sketch, "E756", {"start": v(17.78, -58.38) * mm, "end": v(17.65, -58.55) * mm});
            skLineSegment(sketch, "E757", {"start": v(17.65, -58.55) * mm, "end": v(17.5, -58.71) * mm});
            skLineSegment(sketch, "E758", {"start": v(17.5, -58.71) * mm, "end": v(17.35, -58.87) * mm});
            skLineSegment(sketch, "E759", {"start": v(17.35, -58.87) * mm, "end": v(17.25, -58.96) * mm});
            skLineSegment(sketch, "E760", {"start": v(17.25, -58.96) * mm, "end": v(17.13, -59.06) * mm});
            skLineSegment(sketch, "E761", {"start": v(17.13, -59.06) * mm, "end": v(16.86, -59.25) * mm});
            skLineSegment(sketch, "E762", {"start": v(16.86, -59.25) * mm, "end": v(16.54, -59.44) * mm});
            skLineSegment(sketch, "E763", {"start": v(16.54, -59.44) * mm, "end": v(16.18, -59.63) * mm});
            skLineSegment(sketch, "E764", {"start": v(16.18, -59.63) * mm, "end": v(16.5, -59.67) * mm});
            skLineSegment(sketch, "E765", {"start": v(16.5, -59.67) * mm, "end": v(16.8, -59.72) * mm});
            skLineSegment(sketch, "E766", {"start": v(16.8, -59.72) * mm, "end": v(17.03, -59.78) * mm});
            skLineSegment(sketch, "E767", {"start": v(17.03, -59.78) * mm, "end": v(17.23, -59.85) * mm});
            skLineSegment(sketch, "E768", {"start": v(17.23, -59.85) * mm, "end": v(17.36, -59.91) * mm});
            skLineSegment(sketch, "E769", {"start": v(17.36, -59.91) * mm, "end": v(17.53, -60.02) * mm});
            skLineSegment(sketch, "E770", {"start": v(17.53, -60.02) * mm, "end": v(17.73, -60.16) * mm});
            skLineSegment(sketch, "E771", {"start": v(17.73, -60.16) * mm, "end": v(17.96, -60.33) * mm});
            skLineSegment(sketch, "E772", {"start": v(17.96, -60.33) * mm, "end": v(18.18, -60.52) * mm});
            skLineSegment(sketch, "E773", {"start": v(18.18, -60.52) * mm, "end": v(18.37, -60.68) * mm});
            skLineSegment(sketch, "E774", {"start": v(18.37, -60.68) * mm, "end": v(18.52, -60.83) * mm});
            skLineSegment(sketch, "E775", {"start": v(18.52, -60.83) * mm, "end": v(18.63, -60.95) * mm});
            skLineSegment(sketch, "E776", {"start": v(18.63, -60.95) * mm, "end": v(21.2, -63.95) * mm});
            skLineSegment(sketch, "E777", {"start": v(21.2, -63.95) * mm, "end": v(17.07, -64.9) * mm});
            skLineSegment(sketch, "E778", {"start": v(17.07, -64.9) * mm, "end": v(14.29, -61.75) * mm});
            skLineSegment(sketch, "E779", {"start": v(14.29, -61.75) * mm, "end": v(14.04, -61.48) * mm});
            skLineSegment(sketch, "E780", {"start": v(14.04, -61.48) * mm, "end": v(13.8, -61.26) * mm});
            skLineSegment(sketch, "E781", {"start": v(13.8, -61.26) * mm, "end": v(13.7, -61.17) * mm});
            skLineSegment(sketch, "E782", {"start": v(13.7, -61.17) * mm, "end": v(13.6, -61.1) * mm});
            skLineSegment(sketch, "E783", {"start": v(13.6, -61.1) * mm, "end": v(13.5, -61.04) * mm});
            skLineSegment(sketch, "E784", {"start": v(13.5, -61.04) * mm, "end": v(13.42, -61) * mm});
            skLineSegment(sketch, "E785", {"start": v(13.42, -61) * mm, "end": v(13.3, -60.95) * mm});
            skLineSegment(sketch, "E786", {"start": v(13.3, -60.95) * mm, "end": v(13.19, -60.92) * mm});
            skLineSegment(sketch, "E787", {"start": v(13.19, -60.92) * mm, "end": v(13.07, -60.9) * mm});
            skLineSegment(sketch, "E788", {"start": v(13.07, -60.9) * mm, "end": v(12.95, -60.89) * mm});
            skLineSegment(sketch, "E789", {"start": v(12.95, -60.89) * mm, "end": v(12.83, -60.89) * mm});
            skLineSegment(sketch, "E790", {"start": v(12.83, -60.89) * mm, "end": v(12.7, -60.9) * mm});
            skLineSegment(sketch, "E791", {"start": v(12.7, -60.9) * mm, "end": v(12.58, -60.9) * mm});
            skLineSegment(sketch, "E792", {"start": v(12.58, -60.9) * mm, "end": v(12.46, -60.93) * mm});
            skLineSegment(sketch, "E793", {"start": v(12.46, -60.93) * mm, "end": v(12.14, -61) * mm});
            skLineSegment(sketch, "E794", {"start": v(12.14, -61) * mm, "end": v(13.24, -65.79) * mm});
            skLineSegment(sketch, "E795", {"start": v(13.24, -65.79) * mm, "end": v(9.58, -66.63) * mm});
            skLineSegment(sketch, "E796", {"start": v(9.58, -66.63) * mm, "end": v(6.96, -55.3) * mm});
            skLineSegment(sketch, "E797", {"start": v(6.96, -55.3) * mm, "end": v(6.02, -55.43) * mm});
            skLineSegment(sketch, "E798", {"start": v(6.02, -55.43) * mm, "end": v(5.07, -55.53) * mm});
            skLineSegment(sketch, "E799", {"start": v(5.07, -55.53) * mm, "end": v(4.66, -67.43) * mm});
            skLineSegment(sketch, "E800", {"start": v(4.66, -67.43) * mm, "end": v(0.9, -67.3) * mm});
            skLineSegment(sketch, "E801", {"start": v(0.9, -67.3) * mm, "end": v(1.07, -62.39) * mm});
            skLineSegment(sketch, "E802", {"start": v(1.07, -62.39) * mm, "end": v(-3.03, -62.25) * mm});
            skLineSegment(sketch, "E803", {"start": v(-3.03, -62.25) * mm, "end": v(-3.2, -67.16) * mm});
            skLineSegment(sketch, "E804", {"start": v(-3.2, -67.16) * mm, "end": v(-6.94, -67.03) * mm});
            skLineSegment(sketch, "E805", {"start": v(-6.94, -67.03) * mm, "end": v(-6.53, -55.38) * mm});
            skLineSegment(sketch, "E806", {"start": v(-6.53, -55.38) * mm, "end": v(-7.5, -55.25) * mm});
            skLineSegment(sketch, "E807", {"start": v(-7.5, -55.25) * mm, "end": v(-8.47, -55.1) * mm});
            skLineSegment(sketch, "E808", {"start": v(-8.47, -55.1) * mm, "end": v(-9.42, -54.93) * mm});
            skLineSegment(sketch, "E809", {"start": v(-9.42, -54.93) * mm, "end": v(-10.37, -54.74) * mm});
            skLineSegment(sketch, "E810", {"start": v(-10.37, -54.74) * mm, "end": v(-10.25, -54.89) * mm});
            skLineSegment(sketch, "E811", {"start": v(-10.25, -54.89) * mm, "end": v(-10.12, -55.04) * mm});
            skLineSegment(sketch, "E812", {"start": v(-10.12, -55.04) * mm, "end": v(-10, -55.2) * mm});
            skLineSegment(sketch, "E813", {"start": v(-10, -55.2) * mm, "end": v(-9.9, -55.38) * mm});
            skLineSegment(sketch, "E814", {"start": v(-9.9, -55.38) * mm, "end": v(-9.79, -55.55) * mm});
            skLineSegment(sketch, "E815", {"start": v(-9.79, -55.55) * mm, "end": v(-9.69, -55.73) * mm});
            skLineSegment(sketch, "E816", {"start": v(-9.69, -55.73) * mm, "end": v(-9.6, -55.92) * mm});
            skLineSegment(sketch, "E817", {"start": v(-9.6, -55.92) * mm, "end": v(-9.52, -56.11) * mm});
            skLineSegment(sketch, "E818", {"start": v(-9.52, -56.11) * mm, "end": v(-9.44, -56.31) * mm});
            skLineSegment(sketch, "E819", {"start": v(-9.44, -56.31) * mm, "end": v(-9.37, -56.52) * mm});
            skLineSegment(sketch, "E820", {"start": v(-9.37, -56.52) * mm, "end": v(-9.3, -56.73) * mm});
            skLineSegment(sketch, "E821", {"start": v(-9.3, -56.73) * mm, "end": v(-9.25, -56.95) * mm});
            skLineSegment(sketch, "E822", {"start": v(-9.25, -56.95) * mm, "end": v(-9.2, -57.18) * mm});
            skLineSegment(sketch, "E823", {"start": v(-9.2, -57.18) * mm, "end": v(-9.17, -57.4) * mm});
            skLineSegment(sketch, "E824", {"start": v(-9.17, -57.4) * mm, "end": v(-9.13, -57.64) * mm});
            skLineSegment(sketch, "E825", {"start": v(-9.13, -57.64) * mm, "end": v(-9.1, -57.89) * mm});
            skLineSegment(sketch, "E826", {"start": v(-9.1, -57.89) * mm, "end": v(-9.09, -58.14) * mm});
            skLineSegment(sketch, "E827", {"start": v(-9.09, -58.14) * mm, "end": v(-12.47, -58) * mm});
            skLineSegment(sketch, "E828", {"start": v(-12.47, -58) * mm, "end": v(-12.48, -57.73) * mm});
            skLineSegment(sketch, "E829", {"start": v(-12.48, -57.73) * mm, "end": v(-12.52, -57.5) * mm});
            skLineSegment(sketch, "E830", {"start": v(-12.52, -57.5) * mm, "end": v(-12.56, -57.3) * mm});
            skLineSegment(sketch, "E831", {"start": v(-12.56, -57.3) * mm, "end": v(-12.61, -57.13) * mm});
            skLineSegment(sketch, "E832", {"start": v(-12.61, -57.13) * mm, "end": v(-12.72, -56.9) * mm});
            skLineSegment(sketch, "E833", {"start": v(-12.72, -56.9) * mm, "end": v(-12.86, -56.68) * mm});
            skLineSegment(sketch, "E834", {"start": v(-12.86, -56.68) * mm, "end": v(-13.01, -56.48) * mm});
            skLineSegment(sketch, "E835", {"start": v(-13.01, -56.48) * mm, "end": v(-13.2, -56.3) * mm});
            skLineSegment(sketch, "E836", {"start": v(-13.2, -56.3) * mm, "end": v(-13.29, -56.22) * mm});
            skLineSegment(sketch, "E837", {"start": v(-13.29, -56.22) * mm, "end": v(-13.4, -56.14) * mm});
            skLineSegment(sketch, "E838", {"start": v(-13.4, -56.14) * mm, "end": v(-13.5, -56.07) * mm});
            skLineSegment(sketch, "E839", {"start": v(-13.5, -56.07) * mm, "end": v(-13.61, -56.01) * mm});
            skLineSegment(sketch, "E840", {"start": v(-13.61, -56.01) * mm, "end": v(-13.73, -55.95) * mm});
            skLineSegment(sketch, "E841", {"start": v(-13.73, -55.95) * mm, "end": v(-13.86, -55.9) * mm});
            skLineSegment(sketch, "E842", {"start": v(-13.86, -55.9) * mm, "end": v(-14.12, -55.82) * mm});
            skLineSegment(sketch, "E843", {"start": v(-14.12, -55.82) * mm, "end": v(-14.27, -55.78) * mm});
            skLineSegment(sketch, "E844", {"start": v(-14.27, -55.78) * mm, "end": v(-14.42, -55.76) * mm});
            skLineSegment(sketch, "E845", {"start": v(-14.42, -55.76) * mm, "end": v(-14.57, -55.74) * mm});
            skLineSegment(sketch, "E846", {"start": v(-14.57, -55.74) * mm, "end": v(-14.72, -55.73) * mm});
            skLineSegment(sketch, "E847", {"start": v(-14.72, -55.73) * mm, "end": v(-14.86, -55.73) * mm});
            skLineSegment(sketch, "E848", {"start": v(-14.86, -55.73) * mm, "end": v(-15, -55.74) * mm});
            skLineSegment(sketch, "E849", {"start": v(-15, -55.74) * mm, "end": v(-15.14, -55.75) * mm});
            skLineSegment(sketch, "E850", {"start": v(-15.14, -55.75) * mm, "end": v(-15.27, -55.78) * mm});
            skLineSegment(sketch, "E851", {"start": v(-15.27, -55.78) * mm, "end": v(-15.4, -55.82) * mm});
            skLineSegment(sketch, "E852", {"start": v(-15.4, -55.82) * mm, "end": v(-15.54, -55.86) * mm});
            skLineSegment(sketch, "E853", {"start": v(-15.54, -55.86) * mm, "end": v(-15.67, -55.91) * mm});
            skLineSegment(sketch, "E854", {"start": v(-15.67, -55.91) * mm, "end": v(-15.8, -55.97) * mm});
            skLineSegment(sketch, "E855", {"start": v(-15.8, -55.97) * mm, "end": v(-15.91, -56.04) * mm});
            skLineSegment(sketch, "E856", {"start": v(-15.91, -56.04) * mm, "end": v(-16.04, -56.12) * mm});
            skLineSegment(sketch, "E857", {"start": v(-16.04, -56.12) * mm, "end": v(-16.15, -56.21) * mm});
            skLineSegment(sketch, "E858", {"start": v(-16.15, -56.21) * mm, "end": v(-16.27, -56.31) * mm});
            skLineSegment(sketch, "E859", {"start": v(-16.27, -56.31) * mm, "end": v(-16.44, -56.48) * mm});
            skLineSegment(sketch, "E860", {"start": v(-16.44, -56.48) * mm, "end": v(-16.6, -56.67) * mm});
            skLineSegment(sketch, "E861", {"start": v(-16.6, -56.67) * mm, "end": v(-16.75, -56.9) * mm});
            skLineSegment(sketch, "E862", {"start": v(-16.75, -56.9) * mm, "end": v(-16.89, -57.16) * mm});
            skLineSegment(sketch, "E863", {"start": v(-16.89, -57.16) * mm, "end": v(-17.02, -57.44) * mm});
            skLineSegment(sketch, "E864", {"start": v(-17.02, -57.44) * mm, "end": v(-17.15, -57.76) * mm});
            skLineSegment(sketch, "E865", {"start": v(-17.15, -57.76) * mm, "end": v(-17.26, -58.1) * mm});
            skLineSegment(sketch, "E866", {"start": v(-17.26, -58.1) * mm, "end": v(-17.37, -58.48) * mm});
            skLineSegment(sketch, "E867", {"start": v(-17.37, -58.48) * mm, "end": v(-17.48, -58.95) * mm});
            skLineSegment(sketch, "E868", {"start": v(-17.48, -58.95) * mm, "end": v(-17.57, -59.4) * mm});
            skLineSegment(sketch, "E869", {"start": v(-17.57, -59.4) * mm, "end": v(-17.63, -59.8) * mm});
            skLineSegment(sketch, "E870", {"start": v(-17.63, -59.8) * mm, "end": v(-17.65, -60.16) * mm});
            skLineSegment(sketch, "E871", {"start": v(-17.65, -60.16) * mm, "end": v(-17.65, -60.5) * mm});
            skLineSegment(sketch, "E872", {"start": v(-17.65, -60.5) * mm, "end": v(-17.64, -60.66) * mm});
            skLineSegment(sketch, "E873", {"start": v(-17.64, -60.66) * mm, "end": v(-17.62, -60.8) * mm});
            skLineSegment(sketch, "E874", {"start": v(-17.62, -60.8) * mm, "end": v(-17.6, -60.94) * mm});
            skLineSegment(sketch, "E875", {"start": v(-17.6, -60.94) * mm, "end": v(-17.57, -61.07) * mm});
            skLineSegment(sketch, "E876", {"start": v(-17.57, -61.07) * mm, "end": v(-17.53, -61.2) * mm});
            skLineSegment(sketch, "E877", {"start": v(-17.53, -61.2) * mm, "end": v(-17.48, -61.3) * mm});
            skLineSegment(sketch, "E878", {"start": v(-17.48, -61.3) * mm, "end": v(-17.37, -61.52) * mm});
            skLineSegment(sketch, "E879", {"start": v(-17.37, -61.52) * mm, "end": v(-17.24, -61.71) * mm});
            skLineSegment(sketch, "E880", {"start": v(-17.24, -61.71) * mm, "end": v(-17.08, -61.88) * mm});
            skLineSegment(sketch, "E881", {"start": v(-17.08, -61.88) * mm, "end": v(-16.9, -62.04) * mm});
            skLineSegment(sketch, "E882", {"start": v(-16.9, -62.04) * mm, "end": v(-16.71, -62.17) * mm});
            skLineSegment(sketch, "E883", {"start": v(-16.71, -62.17) * mm, "end": v(-16.5, -62.29) * mm});
            skLineSegment(sketch, "E884", {"start": v(-16.5, -62.29) * mm, "end": v(-16.26, -62.39) * mm});
            skLineSegment(sketch, "E885", {"start": v(-16.26, -62.39) * mm, "end": v(-16, -62.47) * mm});
            skLineSegment(sketch, "E886", {"start": v(-16, -62.47) * mm, "end": v(-15.75, -62.52) * mm});
            skLineSegment(sketch, "E887", {"start": v(-15.75, -62.52) * mm, "end": v(-15.5, -62.56) * mm});
            skLineSegment(sketch, "E888", {"start": v(-15.5, -62.56) * mm, "end": v(-15.27, -62.57) * mm});
            skLineSegment(sketch, "E889", {"start": v(-15.27, -62.57) * mm, "end": v(-15.05, -62.56) * mm});
            skLineSegment(sketch, "E890", {"start": v(-15.05, -62.56) * mm, "end": v(-14.84, -62.53) * mm});
            skLineSegment(sketch, "E891", {"start": v(-14.84, -62.53) * mm, "end": v(-14.64, -62.47) * mm});
            skLineSegment(sketch, "E892", {"start": v(-14.64, -62.47) * mm, "end": v(-14.46, -62.4) * mm});
            skLineSegment(sketch, "E893", {"start": v(-14.46, -62.4) * mm, "end": v(-14.28, -62.3) * mm});
            skLineSegment(sketch, "E894", {"start": v(-14.28, -62.3) * mm, "end": v(-14.1, -62.18) * mm});
            skLineSegment(sketch, "E895", {"start": v(-14.1, -62.18) * mm, "end": v(-13.95, -62.04) * mm});
            skLineSegment(sketch, "E896", {"start": v(-13.95, -62.04) * mm, "end": v(-13.79, -61.88) * mm});
            skLineSegment(sketch, "E897", {"start": v(-13.79, -61.88) * mm, "end": v(-13.63, -61.7) * mm});
            skLineSegment(sketch, "E898", {"start": v(-13.63, -61.7) * mm, "end": v(-13.48, -61.5) * mm});
            skLineSegment(sketch, "E899", {"start": v(-13.48, -61.5) * mm, "end": v(-13.34, -61.3) * mm});
            skLineSegment(sketch, "E900", {"start": v(-13.34, -61.3) * mm, "end": v(-13.2, -61.06) * mm});
            skLineSegment(sketch, "E901", {"start": v(-13.2, -61.06) * mm, "end": v(-13.06, -60.8) * mm});
            skLineSegment(sketch, "E902", {"start": v(-13.06, -60.8) * mm, "end": v(-10.14, -62.6) * mm});
            skLineSegment(sketch, "E903", {"start": v(-10.14, -62.6) * mm, "end": v(-10.3, -62.9) * mm});
            skLineSegment(sketch, "E904", {"start": v(-10.3, -62.9) * mm, "end": v(-10.49, -63.2) * mm});
            skLineSegment(sketch, "E905", {"start": v(-10.49, -63.2) * mm, "end": v(-10.67, -63.46) * mm});
            skLineSegment(sketch, "E906", {"start": v(-10.67, -63.46) * mm, "end": v(-10.87, -63.72) * mm});
            skLineSegment(sketch, "E907", {"start": v(-10.87, -63.72) * mm, "end": v(-11.07, -63.95) * mm});
            skLineSegment(sketch, "E908", {"start": v(-11.07, -63.95) * mm, "end": v(-11.28, -64.17) * mm});
            skLineSegment(sketch, "E909", {"start": v(-11.28, -64.17) * mm, "end": v(-11.5, -64.38) * mm});
            skLineSegment(sketch, "E910", {"start": v(-11.5, -64.38) * mm, "end": v(-11.73, -64.56) * mm});
            skLineSegment(sketch, "E911", {"start": v(-11.73, -64.56) * mm, "end": v(-11.97, -64.73) * mm});
            skLineSegment(sketch, "E912", {"start": v(-11.97, -64.73) * mm, "end": v(-12.2, -64.89) * mm});
            skLineSegment(sketch, "E913", {"start": v(-12.2, -64.89) * mm, "end": v(-12.45, -65.03) * mm});
            skLineSegment(sketch, "E914", {"start": v(-12.45, -65.03) * mm, "end": v(-12.7, -65.15) * mm});
            skLineSegment(sketch, "E915", {"start": v(-12.7, -65.15) * mm, "end": v(-12.97, -65.25) * mm});
            skLineSegment(sketch, "E916", {"start": v(-12.97, -65.25) * mm, "end": v(-13.24, -65.34) * mm});
            skLineSegment(sketch, "E917", {"start": v(-13.24, -65.34) * mm, "end": v(-13.51, -65.41) * mm});
            skLineSegment(sketch, "E918", {"start": v(-13.51, -65.41) * mm, "end": v(-13.8, -65.47) * mm});
            skLineSegment(sketch, "E919", {"start": v(-13.8, -65.47) * mm, "end": v(-14.09, -65.5) * mm});
            skLineSegment(sketch, "E920", {"start": v(-14.09, -65.5) * mm, "end": v(-14.4, -65.52) * mm});
            skLineSegment(sketch, "E921", {"start": v(-14.4, -65.52) * mm, "end": v(-14.71, -65.52) * mm});
            skLineSegment(sketch, "E922", {"start": v(-14.71, -65.52) * mm, "end": v(-15.04, -65.5) * mm});
            skLineSegment(sketch, "E923", {"start": v(-15.04, -65.5) * mm, "end": v(-15.39, -65.47) * mm});
            skLineSegment(sketch, "E924", {"start": v(-15.39, -65.47) * mm, "end": v(-15.75, -65.4) * mm});
            skLineSegment(sketch, "E925", {"start": v(-15.75, -65.4) * mm, "end": v(-16.12, -65.33) * mm});
            skLineSegment(sketch, "E926", {"start": v(-16.12, -65.33) * mm, "end": v(-16.51, -65.24) * mm});
            skLineSegment(sketch, "E927", {"start": v(-16.51, -65.24) * mm, "end": v(-16.98, -65.1) * mm});
            skLineSegment(sketch, "E928", {"start": v(-16.98, -65.1) * mm, "end": v(-17.42, -64.97) * mm});
            skLineSegment(sketch, "E929", {"start": v(-17.42, -64.97) * mm, "end": v(-17.83, -64.81) * mm});
            skLineSegment(sketch, "E930", {"start": v(-17.83, -64.81) * mm, "end": v(-18.21, -64.64) * mm});
            skLineSegment(sketch, "E931", {"start": v(-18.21, -64.64) * mm, "end": v(-18.57, -64.47) * mm});
            skLineSegment(sketch, "E932", {"start": v(-18.57, -64.47) * mm, "end": v(-18.9, -64.28) * mm});
            skLineSegment(sketch, "E933", {"start": v(-18.9, -64.28) * mm, "end": v(-19.21, -64.08) * mm});
            skLineSegment(sketch, "E934", {"start": v(-19.21, -64.08) * mm, "end": v(-19.5, -63.86) * mm});
            skLineSegment(sketch, "E935", {"start": v(-19.5, -63.86) * mm, "end": v(-19.75, -63.63) * mm});
            skLineSegment(sketch, "E936", {"start": v(-19.75, -63.63) * mm, "end": v(-20, -63.38) * mm});
            skLineSegment(sketch, "E937", {"start": v(-20, -63.38) * mm, "end": v(-20.21, -63.1) * mm});
            skLineSegment(sketch, "E938", {"start": v(-20.21, -63.1) * mm, "end": v(-20.42, -62.8) * mm});
            skLineSegment(sketch, "E939", {"start": v(-20.42, -62.8) * mm, "end": v(-20.6, -62.48) * mm});
            skLineSegment(sketch, "E940", {"start": v(-20.6, -62.48) * mm, "end": v(-20.78, -62.13) * mm});
            skLineSegment(sketch, "E941", {"start": v(-20.78, -62.13) * mm, "end": v(-20.93, -61.76) * mm});
            skLineSegment(sketch, "E942", {"start": v(-20.93, -61.76) * mm, "end": v(-21.07, -61.36) * mm});
            skLineSegment(sketch, "E943", {"start": v(-21.07, -61.36) * mm, "end": v(-21.13, -61.16) * mm});
            skLineSegment(sketch, "E944", {"start": v(-21.13, -61.16) * mm, "end": v(-21.18, -60.95) * mm});
            skLineSegment(sketch, "E945", {"start": v(-21.18, -60.95) * mm, "end": v(-21.23, -60.73) * mm});
            skLineSegment(sketch, "E946", {"start": v(-21.23, -60.73) * mm, "end": v(-21.26, -60.51) * mm});
            skLineSegment(sketch, "E947", {"start": v(-21.26, -60.51) * mm, "end": v(-21.29, -60.29) * mm});
            skLineSegment(sketch, "E948", {"start": v(-21.29, -60.29) * mm, "end": v(-21.3, -60.06) * mm});
            skLineSegment(sketch, "E949", {"start": v(-21.3, -60.06) * mm, "end": v(-21.31, -59.83) * mm});
            skLineSegment(sketch, "E950", {"start": v(-21.31, -59.83) * mm, "end": v(-21.31, -59.6) * mm});
            skLineSegment(sketch, "E951", {"start": v(-21.31, -59.6) * mm, "end": v(-21.3, -59.35) * mm});
            skLineSegment(sketch, "E952", {"start": v(-21.3, -59.35) * mm, "end": v(-21.29, -59.1) * mm});
            skLineSegment(sketch, "E953", {"start": v(-21.29, -59.1) * mm, "end": v(-21.26, -58.86) * mm});
            skLineSegment(sketch, "E954", {"start": v(-21.26, -58.86) * mm, "end": v(-21.23, -58.6) * mm});
            skLineSegment(sketch, "E955", {"start": v(-21.23, -58.6) * mm, "end": v(-21.14, -58.09) * mm});
            skLineSegment(sketch, "E956", {"start": v(-21.14, -58.09) * mm, "end": v(-21.01, -57.55) * mm});
            skLineSegment(sketch, "E957", {"start": v(-21.01, -57.55) * mm, "end": v(-20.91, -57.2) * mm});
            skLineSegment(sketch, "E958", {"start": v(-20.91, -57.2) * mm, "end": v(-20.8, -56.85) * mm});
            skLineSegment(sketch, "E959", {"start": v(-20.8, -56.85) * mm, "end": v(-20.68, -56.52) * mm});
            skLineSegment(sketch, "E960", {"start": v(-20.68, -56.52) * mm, "end": v(-20.56, -56.2) * mm});
            skLineSegment(sketch, "E961", {"start": v(-20.56, -56.2) * mm, "end": v(-20.42, -55.9) * mm});
            skLineSegment(sketch, "E962", {"start": v(-20.42, -55.9) * mm, "end": v(-20.27, -55.62) * mm});
            skLineSegment(sketch, "E963", {"start": v(-20.27, -55.62) * mm, "end": v(-20.12, -55.34) * mm});
            skLineSegment(sketch, "E964", {"start": v(-20.12, -55.34) * mm, "end": v(-19.95, -55.08) * mm});
            skLineSegment(sketch, "E965", {"start": v(-19.95, -55.08) * mm, "end": v(-19.78, -54.83) * mm});
            skLineSegment(sketch, "E966", {"start": v(-19.78, -54.83) * mm, "end": v(-19.6, -54.6) * mm});
            skLineSegment(sketch, "E967", {"start": v(-19.6, -54.6) * mm, "end": v(-19.4, -54.38) * mm});
            skLineSegment(sketch, "E968", {"start": v(-19.4, -54.38) * mm, "end": v(-19.2, -54.17) * mm});
            skLineSegment(sketch, "E969", {"start": v(-19.2, -54.17) * mm, "end": v(-18.98, -53.98) * mm});
            skLineSegment(sketch, "E970", {"start": v(-18.98, -53.98) * mm, "end": v(-18.76, -53.8) * mm});
            skLineSegment(sketch, "E971", {"start": v(-18.76, -53.8) * mm, "end": v(-18.53, -53.64) * mm});
            skLineSegment(sketch, "E972", {"start": v(-18.53, -53.64) * mm, "end": v(-18.3, -53.49) * mm});
            skLineSegment(sketch, "E973", {"start": v(-18.3, -53.49) * mm, "end": v(-17.96, -53.3) * mm});
            skLineSegment(sketch, "E974", {"start": v(-17.96, -53.3) * mm, "end": v(-17.62, -53.16) * mm});
            skLineSegment(sketch, "E975", {"start": v(-17.62, -53.16) * mm, "end": v(-17.27, -53.03) * mm});
            skLineSegment(sketch, "E976", {"start": v(-17.27, -53.03) * mm, "end": v(-16.9, -52.93) * mm});
            skLineSegment(sketch, "E977", {"start": v(-16.9, -52.93) * mm, "end": v(-17.8, -52.6) * mm});
            skLineSegment(sketch, "E978", {"start": v(-17.8, -52.6) * mm, "end": v(-18.68, -52.27) * mm});
            skLineSegment(sketch, "E979", {"start": v(-18.68, -52.27) * mm, "end": v(-19.56, -51.91) * mm});
            skLineSegment(sketch, "E980", {"start": v(-19.56, -51.91) * mm, "end": v(-20.43, -51.54) * mm});
            skLineSegment(sketch, "E981", {"start": v(-20.43, -51.54) * mm, "end": v(-21.3, -51.15) * mm});
            skLineSegment(sketch, "E982", {"start": v(-21.3, -51.15) * mm, "end": v(-22.15, -50.75) * mm});
            skLineSegment(sketch, "E983", {"start": v(-22.15, -50.75) * mm, "end": v(-23, -50.33) * mm});
            skLineSegment(sketch, "E984", {"start": v(-23, -50.33) * mm, "end": v(-23.83, -49.9) * mm});
            skLineSegment(sketch, "E985", {"start": v(-23.83, -49.9) * mm, "end": v(-31.49, -52.8) * mm});
            skLineSegment(sketch, "E986", {"start": v(-31.49, -52.8) * mm, "end": v(-34.44, -56.93) * mm});
            skLineSegment(sketch, "E987", {"start": v(-34.44, -56.93) * mm, "end": v(-37.5, -54.74) * mm});
            skLineSegment(sketch, "E988", {"start": v(-37.5, -54.74) * mm, "end": v(-34.54, -50.6) * mm});
            skLineSegment(sketch, "E989", {"start": v(-34.54, -50.6) * mm, "end": v(-34.3, -42.52) * mm});
            skLineSegment(sketch, "E990", {"start": v(-34.3, -42.52) * mm, "end": v(-34.92, -41.95) * mm});
            skLineSegment(sketch, "E991", {"start": v(-34.92, -41.95) * mm, "end": v(-35.52, -41.37) * mm});
            skLineSegment(sketch, "E992", {"start": v(-35.52, -41.37) * mm, "end": v(-35.5, -41.53) * mm});
            skLineSegment(sketch, "E993", {"start": v(-35.5, -41.53) * mm, "end": v(-35.47, -41.69) * mm});
            skLineSegment(sketch, "E994", {"start": v(-35.47, -41.69) * mm, "end": v(-35.46, -41.85) * mm});
            skLineSegment(sketch, "E995", {"start": v(-35.46, -41.85) * mm, "end": v(-35.46, -42) * mm});
            skLineSegment(sketch, "E996", {"start": v(-35.46, -42) * mm, "end": v(-35.47, -42.17) * mm});
            skLineSegment(sketch, "E997", {"start": v(-35.47, -42.17) * mm, "end": v(-35.5, -42.33) * mm});
            skLineSegment(sketch, "E998", {"start": v(-35.5, -42.33) * mm, "end": v(-35.52, -42.5) * mm});
            skLineSegment(sketch, "E999", {"start": v(-35.52, -42.5) * mm, "end": v(-35.55, -42.66) * mm});
            skLineSegment(sketch, "E1000", {"start": v(-35.55, -42.66) * mm, "end": v(-35.62, -42.9) * mm});
            skLineSegment(sketch, "E1001", {"start": v(-35.62, -42.9) * mm, "end": v(-35.71, -43.13) * mm});
            skLineSegment(sketch, "E1002", {"start": v(-35.71, -43.13) * mm, "end": v(-35.82, -43.35) * mm});
            skLineSegment(sketch, "E1003", {"start": v(-35.82, -43.35) * mm, "end": v(-35.95, -43.57) * mm});
            skLineSegment(sketch, "E1004", {"start": v(-35.95, -43.57) * mm, "end": v(-36.1, -43.78) * mm});
            skLineSegment(sketch, "E1005", {"start": v(-36.1, -43.78) * mm, "end": v(-36.27, -43.99) * mm});
            skLineSegment(sketch, "E1006", {"start": v(-36.27, -43.99) * mm, "end": v(-36.46, -44.19) * mm});
            skLineSegment(sketch, "E1007", {"start": v(-36.46, -44.19) * mm, "end": v(-36.67, -44.38) * mm});
            skLineSegment(sketch, "E1008", {"start": v(-36.67, -44.38) * mm, "end": v(-36.86, -44.54) * mm});
            skLineSegment(sketch, "E1009", {"start": v(-36.86, -44.54) * mm, "end": v(-37.05, -44.68) * mm});
            skLineSegment(sketch, "E1010", {"start": v(-37.05, -44.68) * mm, "end": v(-37.25, -44.8) * mm});
            skLineSegment(sketch, "E1011", {"start": v(-37.25, -44.8) * mm, "end": v(-37.45, -44.92) * mm});
            skLineSegment(sketch, "E1012", {"start": v(-37.45, -44.92) * mm, "end": v(-37.65, -45.01) * mm});
            skLineSegment(sketch, "E1013", {"start": v(-37.65, -45.01) * mm, "end": v(-37.85, -45.1) * mm});
            skLineSegment(sketch, "E1014", {"start": v(-37.85, -45.1) * mm, "end": v(-38.06, -45.16) * mm});
            skLineSegment(sketch, "E1015", {"start": v(-38.06, -45.16) * mm, "end": v(-38.26, -45.2) * mm});
            skLineSegment(sketch, "E1016", {"start": v(-38.26, -45.2) * mm, "end": v(-38.47, -45.24) * mm});
            skLineSegment(sketch, "E1017", {"start": v(-38.47, -45.24) * mm, "end": v(-38.68, -45.26) * mm});
            skLineSegment(sketch, "E1018", {"start": v(-38.68, -45.26) * mm, "end": v(-38.9, -45.26) * mm});
            skLineSegment(sketch, "E1019", {"start": v(-38.9, -45.26) * mm, "end": v(-39.1, -45.26) * mm});
            skLineSegment(sketch, "E1020", {"start": v(-39.1, -45.26) * mm, "end": v(-39.31, -45.23) * mm});
            skLineSegment(sketch, "E1021", {"start": v(-39.31, -45.23) * mm, "end": v(-39.52, -45.2) * mm});
            skLineSegment(sketch, "E1022", {"start": v(-39.52, -45.2) * mm, "end": v(-39.73, -45.15) * mm});
            skLineSegment(sketch, "E1023", {"start": v(-39.73, -45.15) * mm, "end": v(-39.94, -45.1) * mm});
            skLineSegment(sketch, "E1024", {"start": v(-39.94, -45.1) * mm, "end": v(-40.08, -45.04) * mm});
            skLineSegment(sketch, "E1025", {"start": v(-40.08, -45.04) * mm, "end": v(-40.22, -44.99) * mm});
            skLineSegment(sketch, "E1026", {"start": v(-40.22, -44.99) * mm, "end": v(-40.51, -44.84) * mm});
            skLineSegment(sketch, "E1027", {"start": v(-40.51, -44.84) * mm, "end": v(-40.83, -44.65) * mm});
            skLineSegment(sketch, "E1028", {"start": v(-40.83, -44.65) * mm, "end": v(-41.17, -44.42) * mm});
            skLineSegment(sketch, "E1029", {"start": v(-41.17, -44.42) * mm, "end": v(-41.05, -44.73) * mm});
            skLineSegment(sketch, "E1030", {"start": v(-41.05, -44.73) * mm, "end": v(-40.96, -45) * mm});
            skLineSegment(sketch, "E1031", {"start": v(-40.96, -45) * mm, "end": v(-40.9, -45.24) * mm});
            skLineSegment(sketch, "E1032", {"start": v(-40.9, -45.24) * mm, "end": v(-40.86, -45.44) * mm});
            skLineSegment(sketch, "E1033", {"start": v(-40.86, -45.44) * mm, "end": v(-40.86, -45.6) * mm});
            skLineSegment(sketch, "E1034", {"start": v(-40.86, -45.6) * mm, "end": v(-40.87, -45.79) * mm});
            skLineSegment(sketch, "E1035", {"start": v(-40.87, -45.79) * mm, "end": v(-40.9, -46.03) * mm});
            skLineSegment(sketch, "E1036", {"start": v(-40.9, -46.03) * mm, "end": v(-40.95, -46.31) * mm});
            skLineSegment(sketch, "E1037", {"start": v(-40.95, -46.31) * mm, "end": v(-41, -46.6) * mm});
            skLineSegment(sketch, "E1038", {"start": v(-41, -46.6) * mm, "end": v(-41.06, -46.84) * mm});
            skLineSegment(sketch, "E1039", {"start": v(-41.06, -46.84) * mm, "end": v(-41.12, -47.04) * mm});
            skLineSegment(sketch, "E1040", {"start": v(-41.12, -47.04) * mm, "end": v(-41.17, -47.2) * mm});
            skLineSegment(sketch, "E1041", {"start": v(-41.17, -47.2) * mm, "end": v(-42.62, -50.88) * mm});
            skLineSegment(sketch, "E1042", {"start": v(-42.62, -50.88) * mm, "end": v(-45.4, -47.69) * mm});
            skLineSegment(sketch, "E1043", {"start": v(-45.4, -47.69) * mm, "end": v(-43.93, -43.75) * mm});
            skLineSegment(sketch, "E1044", {"start": v(-43.93, -43.75) * mm, "end": v(-43.8, -43.4) * mm});
            skLineSegment(sketch, "E1045", {"start": v(-43.8, -43.4) * mm, "end": v(-43.72, -43.09) * mm});
            skLineSegment(sketch, "E1046", {"start": v(-43.72, -43.09) * mm, "end": v(-43.7, -42.95) * mm});
            skLineSegment(sketch, "E1047", {"start": v(-43.7, -42.95) * mm, "end": v(-43.68, -42.83) * mm});
            skLineSegment(sketch, "E1048", {"start": v(-43.68, -42.83) * mm, "end": v(-43.67, -42.72) * mm});
            skLineSegment(sketch, "E1049", {"start": v(-43.67, -42.72) * mm, "end": v(-43.67, -42.62) * mm});
            skLineSegment(sketch, "E1050", {"start": v(-43.67, -42.62) * mm, "end": v(-43.7, -42.5) * mm});
            skLineSegment(sketch, "E1051", {"start": v(-43.7, -42.5) * mm, "end": v(-43.72, -42.39) * mm});
            skLineSegment(sketch, "E1052", {"start": v(-43.72, -42.39) * mm, "end": v(-43.75, -42.27) * mm});
            skLineSegment(sketch, "E1053", {"start": v(-43.75, -42.27) * mm, "end": v(-43.8, -42.16) * mm});
            skLineSegment(sketch, "E1054", {"start": v(-43.8, -42.16) * mm, "end": v(-43.85, -42.05) * mm});
            skLineSegment(sketch, "E1055", {"start": v(-43.85, -42.05) * mm, "end": v(-43.92, -41.95) * mm});
            skLineSegment(sketch, "E1056", {"start": v(-43.92, -41.95) * mm, "end": v(-43.99, -41.85) * mm});
            skLineSegment(sketch, "E1057", {"start": v(-43.99, -41.85) * mm, "end": v(-44.07, -41.75) * mm});
            skLineSegment(sketch, "E1058", {"start": v(-44.07, -41.75) * mm, "end": v(-44.28, -41.5) * mm});
            skLineSegment(sketch, "E1059", {"start": v(-44.28, -41.5) * mm, "end": v(-47.98, -44.73) * mm});
            skLineSegment(sketch, "E1060", {"start": v(-47.98, -44.73) * mm, "end": v(-50.45, -41.9) * mm});
            skLineSegment(sketch, "E1061", {"start": v(-50.45, -41.9) * mm, "end": v(-41.64, -34.2) * mm});
            skLineSegment(sketch, "E1062", {"start": v(-41.64, -34.2) * mm, "end": v(-42.1, -33.53) * mm});
            skLineSegment(sketch, "E1063", {"start": v(-42.1, -33.53) * mm, "end": v(-42.55, -32.85) * mm});
            skLineSegment(sketch, "E1064", {"start": v(-42.55, -32.85) * mm, "end": v(-43, -32.17) * mm});
            skLineSegment(sketch, "E1065", {"start": v(-43, -32.17) * mm, "end": v(-43.43, -31.48) * mm});
            skLineSegment(sketch, "E1066", {"start": v(-43.43, -31.48) * mm, "end": v(-43.43, -31.65) * mm});
            skLineSegment(sketch, "E1067", {"start": v(-43.43, -31.65) * mm, "end": v(-43.45, -31.83) * mm});
            skLineSegment(sketch, "E1068", {"start": v(-43.45, -31.83) * mm, "end": v(-43.48, -32) * mm});
            skLineSegment(sketch, "E1069", {"start": v(-43.48, -32) * mm, "end": v(-43.52, -32.17) * mm});
            skLineSegment(sketch, "E1070", {"start": v(-43.52, -32.17) * mm, "end": v(-43.57, -32.34) * mm});
            skLineSegment(sketch, "E1071", {"start": v(-43.57, -32.34) * mm, "end": v(-43.63, -32.5) * mm});
            skLineSegment(sketch, "E1072", {"start": v(-43.63, -32.5) * mm, "end": v(-43.7, -32.67) * mm});
            skLineSegment(sketch, "E1073", {"start": v(-43.7, -32.67) * mm, "end": v(-43.8, -32.84) * mm});
            skLineSegment(sketch, "E1074", {"start": v(-43.8, -32.84) * mm, "end": v(-43.92, -33.05) * mm});
            skLineSegment(sketch, "E1075", {"start": v(-43.92, -33.05) * mm, "end": v(-44.07, -33.25) * mm});
            skLineSegment(sketch, "E1076", {"start": v(-44.07, -33.25) * mm, "end": v(-44.23, -33.44) * mm});
            skLineSegment(sketch, "E1077", {"start": v(-44.23, -33.44) * mm, "end": v(-44.4, -33.61) * mm});
            skLineSegment(sketch, "E1078", {"start": v(-44.4, -33.61) * mm, "end": v(-44.6, -33.78) * mm});
            skLineSegment(sketch, "E1079", {"start": v(-44.6, -33.78) * mm, "end": v(-44.82, -33.94) * mm});
            skLineSegment(sketch, "E1080", {"start": v(-44.82, -33.94) * mm, "end": v(-45.06, -34.08) * mm});
            skLineSegment(sketch, "E1081", {"start": v(-45.06, -34.08) * mm, "end": v(-45.3, -34.21) * mm});
            skLineSegment(sketch, "E1082", {"start": v(-45.3, -34.21) * mm, "end": v(-45.53, -34.32) * mm});
            skLineSegment(sketch, "E1083", {"start": v(-45.53, -34.32) * mm, "end": v(-45.76, -34.4) * mm});
            skLineSegment(sketch, "E1084", {"start": v(-45.76, -34.4) * mm, "end": v(-45.98, -34.48) * mm});
            skLineSegment(sketch, "E1085", {"start": v(-45.98, -34.48) * mm, "end": v(-46.2, -34.53) * mm});
            skLineSegment(sketch, "E1086", {"start": v(-46.2, -34.53) * mm, "end": v(-46.42, -34.57) * mm});
            skLineSegment(sketch, "E1087", {"start": v(-46.42, -34.57) * mm, "end": v(-46.63, -34.6) * mm});
            skLineSegment(sketch, "E1088", {"start": v(-46.63, -34.6) * mm, "end": v(-46.85, -34.6) * mm});
            skLineSegment(sketch, "E1089", {"start": v(-46.85, -34.6) * mm, "end": v(-47.06, -34.6) * mm});
            skLineSegment(sketch, "E1090", {"start": v(-47.06, -34.6) * mm, "end": v(-47.27, -34.58) * mm});
            skLineSegment(sketch, "E1091", {"start": v(-47.27, -34.58) * mm, "end": v(-47.48, -34.54) * mm});
            skLineSegment(sketch, "E1092", {"start": v(-47.48, -34.54) * mm, "end": v(-47.68, -34.5) * mm});
            skLineSegment(sketch, "E1093", {"start": v(-47.68, -34.5) * mm, "end": v(-47.88, -34.43) * mm});
            skLineSegment(sketch, "E1094", {"start": v(-47.88, -34.43) * mm, "end": v(-48.08, -34.36) * mm});
            skLineSegment(sketch, "E1095", {"start": v(-48.08, -34.36) * mm, "end": v(-48.28, -34.27) * mm});
            skLineSegment(sketch, "E1096", {"start": v(-48.28, -34.27) * mm, "end": v(-48.47, -34.17) * mm});
            skLineSegment(sketch, "E1097", {"start": v(-48.47, -34.17) * mm, "end": v(-48.65, -34.06) * mm});
            skLineSegment(sketch, "E1098", {"start": v(-48.65, -34.06) * mm, "end": v(-48.77, -33.98) * mm});
            skLineSegment(sketch, "E1099", {"start": v(-48.77, -33.98) * mm, "end": v(-48.9, -33.89) * mm});
            skLineSegment(sketch, "E1100", {"start": v(-48.9, -33.89) * mm, "end": v(-49.14, -33.67) * mm});
            skLineSegment(sketch, "E1101", {"start": v(-49.14, -33.67) * mm, "end": v(-49.4, -33.4) * mm});
            skLineSegment(sketch, "E1102", {"start": v(-49.4, -33.4) * mm, "end": v(-49.67, -33.1) * mm});
            skLineSegment(sketch, "E1103", {"start": v(-49.67, -33.1) * mm, "end": v(-49.63, -33.42) * mm});
            skLineSegment(sketch, "E1104", {"start": v(-49.63, -33.42) * mm, "end": v(-49.61, -33.71) * mm});
            skLineSegment(sketch, "E1105", {"start": v(-49.61, -33.71) * mm, "end": v(-49.61, -33.96) * mm});
            skLineSegment(sketch, "E1106", {"start": v(-49.61, -33.96) * mm, "end": v(-49.64, -34.16) * mm});
            skLineSegment(sketch, "E1107", {"start": v(-49.64, -34.16) * mm, "end": v(-49.67, -34.3) * mm});
            skLineSegment(sketch, "E1108", {"start": v(-49.67, -34.3) * mm, "end": v(-49.73, -34.5) * mm});
            skLineSegment(sketch, "E1109", {"start": v(-49.73, -34.5) * mm, "end": v(-49.83, -34.72) * mm});
            skLineSegment(sketch, "E1110", {"start": v(-49.83, -34.72) * mm, "end": v(-49.94, -34.98) * mm});
            skLineSegment(sketch, "E1111", {"start": v(-49.94, -34.98) * mm, "end": v(-50.07, -35.25) * mm});
            skLineSegment(sketch, "E1112", {"start": v(-50.07, -35.25) * mm, "end": v(-50.19, -35.47) * mm});
            skLineSegment(sketch, "E1113", {"start": v(-50.19, -35.47) * mm, "end": v(-50.3, -35.65) * mm});
            skLineSegment(sketch, "E1114", {"start": v(-50.3, -35.65) * mm, "end": v(-50.39, -35.78) * mm});
            skLineSegment(sketch, "E1115", {"start": v(-50.39, -35.78) * mm, "end": v(-52.72, -38.97) * mm});
            skLineSegment(sketch, "E1116", {"start": v(-52.72, -38.97) * mm, "end": v(-54.6, -35.17) * mm});
            skLineSegment(sketch, "E1117", {"start": v(-54.6, -35.17) * mm, "end": v(-52.17, -31.74) * mm});
            skLineSegment(sketch, "E1118", {"start": v(-52.17, -31.74) * mm, "end": v(-51.95, -31.43) * mm});
            skLineSegment(sketch, "E1119", {"start": v(-51.95, -31.43) * mm, "end": v(-51.8, -31.16) * mm});
            skLineSegment(sketch, "E1120", {"start": v(-51.8, -31.16) * mm, "end": v(-51.73, -31.03) * mm});
            skLineSegment(sketch, "E1121", {"start": v(-51.73, -31.03) * mm, "end": v(-51.69, -30.92) * mm});
            skLineSegment(sketch, "E1122", {"start": v(-51.69, -30.92) * mm, "end": v(-51.65, -30.81) * mm});
            skLineSegment(sketch, "E1123", {"start": v(-51.65, -30.81) * mm, "end": v(-51.63, -30.72) * mm});
            skLineSegment(sketch, "E1124", {"start": v(-51.63, -30.72) * mm, "end": v(-51.62, -30.6) * mm});
            skLineSegment(sketch, "E1125", {"start": v(-51.62, -30.6) * mm, "end": v(-51.61, -30.48) * mm});
            skLineSegment(sketch, "E1126", {"start": v(-51.61, -30.48) * mm, "end": v(-51.62, -30.36) * mm});
            skLineSegment(sketch, "E1127", {"start": v(-51.62, -30.36) * mm, "end": v(-51.63, -30.24) * mm});
            skLineSegment(sketch, "E1128", {"start": v(-51.63, -30.24) * mm, "end": v(-51.66, -30.12) * mm});
            skLineSegment(sketch, "E1129", {"start": v(-51.66, -30.12) * mm, "end": v(-51.7, -30) * mm});
            skLineSegment(sketch, "E1130", {"start": v(-51.7, -30) * mm, "end": v(-51.73, -29.89) * mm});
            skLineSegment(sketch, "E1131", {"start": v(-51.73, -29.89) * mm, "end": v(-51.78, -29.77) * mm});
            skLineSegment(sketch, "E1132", {"start": v(-51.78, -29.77) * mm, "end": v(-51.93, -29.47) * mm});
            skLineSegment(sketch, "E1133", {"start": v(-51.93, -29.47) * mm, "end": v(-56.33, -31.65) * mm});
            skLineSegment(sketch, "E1134", {"start": v(-56.33, -31.65) * mm, "end": v(-58, -28.28) * mm});
            skLineSegment(sketch, "E1135", {"start": v(-58, -28.28) * mm, "end": v(-47.54, -23.12) * mm});
            skLineSegment(sketch, "E1136", {"start": v(-47.54, -23.12) * mm, "end": v(-47.88, -22.19) * mm});
            skLineSegment(sketch, "E1137", {"start": v(-47.88, -22.19) * mm, "end": v(-48.21, -21.25) * mm});
            skLineSegment(sketch, "E1138", {"start": v(-48.21, -21.25) * mm, "end": v(-50.3, -21.73) * mm});
            skLineSegment(sketch, "E1139", {"start": v(-50.3, -21.73) * mm, "end": v(-51.7, -15.63) * mm});
            skLineSegment(sketch, "E1140", {"start": v(-51.7, -15.63) * mm, "end": v(-53.59, -16.06) * mm});
            skLineSegment(sketch, "E1141", {"start": v(-53.59, -16.06) * mm, "end": v(-52.28, -21.72) * mm});
            skLineSegment(sketch, "E1142", {"start": v(-52.28, -21.72) * mm, "end": v(-54.69, -22.28) * mm});
            skLineSegment(sketch, "E1143", {"start": v(-54.69, -22.28) * mm, "end": v(-56, -16.62) * mm});
            skLineSegment(sketch, "E1144", {"start": v(-56, -16.62) * mm, "end": v(-58.32, -17.16) * mm});
            skLineSegment(sketch, "E1145", {"start": v(-58.32, -17.16) * mm, "end": v(-56.87, -23.44) * mm});
            skLineSegment(sketch, "E1146", {"start": v(-56.87, -23.44) * mm, "end": v(-59.54, -24.06) * mm});
            skLineSegment(sketch, "E1147", {"start": v(-59.54, -24.06) * mm, "end": v(-61.84, -14.1) * mm});
            skLineSegment(sketch, "E1148", {"start": v(-61.84, -14.1) * mm, "end": v(-50.46, -11.48) * mm});
            skLineSegment(sketch, "E1149", {"start": v(-50.46, -11.48) * mm, "end": v(-50.56, -10.61) * mm});
            skLineSegment(sketch, "E1150", {"start": v(-50.56, -10.61) * mm, "end": v(-50.65, -9.74) * mm});
            skLineSegment(sketch, "E1151", {"start": v(-50.65, -9.74) * mm, "end": v(-62.5, -9.33) * mm});
            skLineSegment(sketch, "E1152", {"start": v(-62.5, -9.33) * mm, "end": v(-62.4, -6.26) * mm});
            skLineSegment(sketch, "E1153", {"start": v(-62.4, -6.26) * mm, "end": v(-53.15, -6.58) * mm});
            skLineSegment(sketch, "E1154", {"start": v(-53.15, -6.58) * mm, "end": v(-62.3, -3.9) * mm});
            skLineSegment(sketch, "E1155", {"start": v(-62.3, -3.9) * mm, "end": v(-62.21, -1.12) * mm});
            skLineSegment(sketch, "E1156", {"start": v(-62.21, -1.12) * mm, "end": v(-52.9, 0.91) * mm});
            skLineSegment(sketch, "E1157", {"start": v(-52.9, 0.91) * mm, "end": v(-62.13, 1.23) * mm});
            skLineSegment(sketch, "E1158", {"start": v(-62.13, 1.23) * mm, "end": v(-62.03, 4.3) * mm});
            skLineSegment(sketch, "E1159", {"start": v(-62.03, 4.3) * mm, "end": v(-50.1, 3.88) * mm});
            skLineSegment(sketch, "E1160", {"start": v(-50.1, 3.88) * mm, "end": v(-49.95, 4.7) * mm});
            skLineSegment(sketch, "E1161", {"start": v(-49.95, 4.7) * mm, "end": v(-49.79, 5.5) * mm});
            skLineSegment(sketch, "E1162", {"start": v(-49.79, 5.5) * mm, "end": v(-49.61, 6.3) * mm});
            skLineSegment(sketch, "E1163", {"start": v(-49.61, 6.3) * mm, "end": v(-49.42, 7.1) * mm});
            skLineSegment(sketch, "E1164", {"start": v(-49.42, 7.1) * mm, "end": v(-49.22, 7.9) * mm});
            skLineSegment(sketch, "E1165", {"start": v(-49.22, 7.9) * mm, "end": v(-49, 8.69) * mm});
            skLineSegment(sketch, "E1166", {"start": v(-49, 8.69) * mm, "end": v(-48.78, 9.47) * mm});
            skLineSegment(sketch, "E1167", {"start": v(-48.78, 9.47) * mm, "end": v(-48.55, 10.25) * mm});
            skLineSegment(sketch, "E1168", {"start": v(-48.55, 10.25) * mm, "end": v(-48.3, 11.02) * mm});
            skLineSegment(sketch, "E1169", {"start": v(-48.3, 11.02) * mm, "end": v(-48.04, 11.79) * mm});
            skLineSegment(sketch, "E1170", {"start": v(-48.04, 11.79) * mm, "end": v(-47.76, 12.55) * mm});
            skLineSegment(sketch, "E1171", {"start": v(-47.76, 12.55) * mm, "end": v(-47.48, 13.3) * mm});
            skLineSegment(sketch, "E1172", {"start": v(-47.48, 13.3) * mm, "end": v(-47.18, 14.05) * mm});
            skLineSegment(sketch, "E1173", {"start": v(-47.18, 14.05) * mm, "end": v(-46.87, 14.8) * mm});
            skLineSegment(sketch, "E1174", {"start": v(-46.87, 14.8) * mm, "end": v(-46.55, 15.54) * mm});
            skLineSegment(sketch, "E1175", {"start": v(-46.55, 15.54) * mm, "end": v(-46.22, 16.27) * mm});
            skLineSegment(sketch, "E1176", {"start": v(-46.22, 16.27) * mm, "end": v(-45.88, 17) * mm});
            skLineSegment(sketch, "E1177", {"start": v(-45.88, 17) * mm, "end": v(-45.53, 17.71) * mm});
            skLineSegment(sketch, "E1178", {"start": v(-45.53, 17.71) * mm, "end": v(-45.16, 18.43) * mm});
            skLineSegment(sketch, "E1179", {"start": v(-45.16, 18.43) * mm, "end": v(-44.79, 19.13) * mm});
            skLineSegment(sketch, "E1180", {"start": v(-44.79, 19.13) * mm, "end": v(-44.4, 19.83) * mm});
            skLineSegment(sketch, "E1181", {"start": v(-44.4, 19.83) * mm, "end": v(-44, 20.53) * mm});
            skLineSegment(sketch, "E1182", {"start": v(-44, 20.53) * mm, "end": v(-43.6, 21.21) * mm});
            skLineSegment(sketch, "E1183", {"start": v(-43.6, 21.21) * mm, "end": v(-43.18, 21.9) * mm});
            skLineSegment(sketch, "E1184", {"start": v(-43.18, 21.9) * mm, "end": v(-42.76, 22.56) * mm});
            skLineSegment(sketch, "E1185", {"start": v(-42.76, 22.56) * mm, "end": v(-42.32, 23.23) * mm});
            skLineSegment(sketch, "E1186", {"start": v(-42.32, 23.23) * mm, "end": v(-41.87, 23.89) * mm});
            skLineSegment(sketch, "E1187", {"start": v(-41.87, 23.89) * mm, "end": v(-41.41, 24.54) * mm});
            skLineSegment(sketch, "E1188", {"start": v(-41.41, 24.54) * mm, "end": v(-40.95, 25.18) * mm});
            skLineSegment(sketch, "E1189", {"start": v(-40.95, 25.18) * mm, "end": v(-40.47, 25.82) * mm});
            skLineSegment(sketch, "E1190", {"start": v(-40.47, 25.82) * mm, "end": v(-39.98, 26.44) * mm});
            skLineSegment(sketch, "E1191", {"start": v(-39.98, 26.44) * mm, "end": v(-39.48, 27.06) * mm});
            skLineSegment(sketch, "E1192", {"start": v(-39.48, 27.06) * mm, "end": v(-38.98, 27.67) * mm});
            skLineSegment(sketch, "E1193", {"start": v(-38.98, 27.67) * mm, "end": v(-38.46, 28.28) * mm});
            skLineSegment(sketch, "E1194", {"start": v(-38.46, 28.28) * mm, "end": v(-37.94, 28.87) * mm});
            skLineSegment(sketch, "E1195", {"start": v(-37.94, 28.87) * mm, "end": v(-37.4, 29.46) * mm});
            skLineSegment(sketch, "E1196", {"start": v(-37.4, 29.46) * mm, "end": v(-36.86, 30.04) * mm});
            skLineSegment(sketch, "E1197", {"start": v(-36.86, 30.04) * mm, "end": v(-36.31, 30.6) * mm});
            skLineSegment(sketch, "E1198", {"start": v(-36.31, 30.6) * mm, "end": v(-35.75, 31.17) * mm});
            skLineSegment(sketch, "E1199", {"start": v(-35.75, 31.17) * mm, "end": v(-35.18, 31.72) * mm});
            skLineSegment(sketch, "E1200", {"start": v(-35.18, 31.72) * mm, "end": v(-34.6, 32.26) * mm});
            skLineSegment(sketch, "E1201", {"start": v(-34.6, 32.26) * mm, "end": v(-34.02, 32.8) * mm});
            skLineSegment(sketch, "E1202", {"start": v(-34.02, 32.8) * mm, "end": v(-33.43, 33.33) * mm});
            skLineSegment(sketch, "E1203", {"start": v(-33.43, 33.33) * mm, "end": v(-32.82, 33.84) * mm});
            skLineSegment(sketch, "E1204", {"start": v(-32.82, 33.84) * mm, "end": v(-32.21, 34.35) * mm});
            skLineSegment(sketch, "E1205", {"start": v(-32.21, 34.35) * mm, "end": v(-31.6, 34.85) * mm});
            skLineSegment(sketch, "E1206", {"start": v(-31.6, 34.85) * mm, "end": v(-30.97, 35.33) * mm});
            skLineSegment(sketch, "E1207", {"start": v(-30.97, 35.33) * mm, "end": v(-30.34, 35.81) * mm});
            skLineSegment(sketch, "E1208", {"start": v(-30.34, 35.81) * mm, "end": v(-29.7, 36.28) * mm});
            skLineSegment(sketch, "E1209", {"start": v(-29.7, 36.28) * mm, "end": v(-29.05, 36.74) * mm});
            skLineSegment(sketch, "E1210", {"start": v(-29.05, 36.74) * mm, "end": v(-28.39, 37.2) * mm});
            skLineSegment(sketch, "E1211", {"start": v(-28.39, 37.2) * mm, "end": v(-27.72, 37.63) * mm});
            skLineSegment(sketch, "E1212", {"start": v(-27.72, 37.63) * mm, "end": v(-27.05, 38.06) * mm});
            skLineSegment(sketch, "E1213", {"start": v(-27.05, 38.06) * mm, "end": v(-26.38, 38.48) * mm});
            skLineSegment(sketch, "E1214", {"start": v(-26.38, 38.48) * mm, "end": v(-25.7, 38.89) * mm});
            skLineSegment(sketch, "E1215", {"start": v(-25.7, 38.89) * mm, "end": v(-25, 39.28) * mm});
            skLineSegment(sketch, "E1216", {"start": v(-25, 39.28) * mm, "end": v(-24.3, 39.67) * mm});
            skLineSegment(sketch, "E1217", {"start": v(-24.3, 39.67) * mm, "end": v(-23.6, 40.05) * mm});
            skLineSegment(sketch, "E1218", {"start": v(-23.6, 40.05) * mm, "end": v(-22.88, 40.41) * mm});
            skLineSegment(sketch, "E1219", {"start": v(-22.88, 40.41) * mm, "end": v(-22.16, 40.77) * mm});
            skLineSegment(sketch, "E1220", {"start": v(-22.16, 40.77) * mm, "end": v(-21.44, 41.11) * mm});
            skLineSegment(sketch, "E1221", {"start": v(-21.44, 41.11) * mm, "end": v(-20.7, 41.44) * mm});
            skLineSegment(sketch, "E1222", {"start": v(-20.7, 41.44) * mm, "end": v(-19.97, 41.76) * mm});
            skLineSegment(sketch, "E1223", {"start": v(-19.97, 41.76) * mm, "end": v(-19.23, 42.07) * mm});
            skLineSegment(sketch, "E1224", {"start": v(-19.23, 42.07) * mm, "end": v(-19.28, 42.45) * mm});
            skLineSegment(sketch, "E1225", {"start": v(-19.28, 42.45) * mm, "end": v(-19.32, 42.83) * mm});
            skLineSegment(sketch, "E1226", {"start": v(-19.32, 42.83) * mm, "end": v(-19.35, 43.2) * mm});
            skLineSegment(sketch, "E1227", {"start": v(-19.35, 43.2) * mm, "end": v(-19.36, 43.58) * mm});
            skLineSegment(sketch, "E1228", {"start": v(-19.36, 43.58) * mm, "end": v(-19.36, 43.95) * mm});
            skLineSegment(sketch, "E1229", {"start": v(-19.36, 43.95) * mm, "end": v(-19.33, 44.32) * mm});
            skLineSegment(sketch, "E1230", {"start": v(-19.33, 44.32) * mm, "end": v(-19.3, 44.69) * mm});
            skLineSegment(sketch, "E1231", {"start": v(-19.3, 44.69) * mm, "end": v(-19.24, 45.05) * mm});
            skLineSegment(sketch, "E1232", {"start": v(-19.24, 45.05) * mm, "end": v(-19.17, 45.4) * mm});
            skLineSegment(sketch, "E1233", {"start": v(-19.17, 45.4) * mm, "end": v(-19.07, 45.75) * mm});
            skLineSegment(sketch, "E1234", {"start": v(-19.07, 45.75) * mm, "end": v(-18.96, 46.1) * mm});
            skLineSegment(sketch, "E1235", {"start": v(-18.96, 46.1) * mm, "end": v(-18.83, 46.44) * mm});
            skLineSegment(sketch, "E1236", {"start": v(-18.83, 46.44) * mm, "end": v(-18.68, 46.78) * mm});
            skLineSegment(sketch, "E1237", {"start": v(-18.68, 46.78) * mm, "end": v(-18.5, 47.1) * mm});
            skLineSegment(sketch, "E1238", {"start": v(-18.5, 47.1) * mm, "end": v(-18.31, 47.43) * mm});
            skLineSegment(sketch, "E1239", {"start": v(-18.31, 47.43) * mm, "end": v(-18.1, 47.75) * mm});
            skLineSegment(sketch, "E1240", {"start": v(-18.1, 47.75) * mm, "end": v(-17.84, 48.1) * mm});
            skLineSegment(sketch, "E1241", {"start": v(-17.84, 48.1) * mm, "end": v(-17.57, 48.4) * mm});
            skLineSegment(sketch, "E1242", {"start": v(-17.57, 48.4) * mm, "end": v(-17.3, 48.69) * mm});
            skLineSegment(sketch, "E1243", {"start": v(-17.3, 48.69) * mm, "end": v(-17.03, 48.95) * mm});
            skLineSegment(sketch, "E1244", {"start": v(-17.03, 48.95) * mm, "end": v(-16.74, 49.18) * mm});
            skLineSegment(sketch, "E1245", {"start": v(-16.74, 49.18) * mm, "end": v(-16.46, 49.38) * mm});
            skLineSegment(sketch, "E1246", {"start": v(-16.46, 49.38) * mm, "end": v(-16.17, 49.56) * mm});
            skLineSegment(sketch, "E1247", {"start": v(-16.17, 49.56) * mm, "end": v(-15.87, 49.7) * mm});
            skLineSegment(sketch, "E1248", {"start": v(-15.87, 49.7) * mm, "end": v(-15.57, 49.84) * mm});
            skLineSegment(sketch, "E1249", {"start": v(-15.57, 49.84) * mm, "end": v(-15.27, 49.94) * mm});
            skLineSegment(sketch, "E1250", {"start": v(-15.27, 49.94) * mm, "end": v(-14.96, 50.02) * mm});
            skLineSegment(sketch, "E1251", {"start": v(-14.96, 50.02) * mm, "end": v(-14.65, 50.08) * mm});
            skLineSegment(sketch, "E1252", {"start": v(-14.65, 50.08) * mm, "end": v(-14.34, 50.12) * mm});
            skLineSegment(sketch, "E1253", {"start": v(-14.34, 50.12) * mm, "end": v(-14.02, 50.14) * mm});
            skLineSegment(sketch, "E1254", {"start": v(-14.02, 50.14) * mm, "end": v(-13.7, 50.14) * mm});
            skLineSegment(sketch, "E1255", {"start": v(-13.7, 50.14) * mm, "end": v(-13.38, 50.11) * mm});
            skLineSegment(sketch, "E1256", {"start": v(-13.38, 50.11) * mm, "end": v(-13.06, 50.07) * mm});
            skLineSegment(sketch, "E1257", {"start": v(-13.06, 50.07) * mm, "end": v(-12.74, 50.01) * mm});
            skLineSegment(sketch, "E1258", {"start": v(-12.74, 50.01) * mm, "end": v(-12.41, 49.94) * mm});
            skLineSegment(sketch, "E1259", {"start": v(-12.41, 49.94) * mm, "end": v(-12.08, 49.84) * mm});
            skLineSegment(sketch, "E1260", {"start": v(-12.08, 49.84) * mm, "end": v(-11.75, 49.73) * mm});
            skLineSegment(sketch, "E1261", {"start": v(-11.75, 49.73) * mm, "end": v(-11.43, 49.6) * mm});
            skLineSegment(sketch, "E1262", {"start": v(-11.43, 49.6) * mm, "end": v(-11.1, 49.47) * mm});
            skLineSegment(sketch, "E1263", {"start": v(-11.1, 49.47) * mm, "end": v(-10.77, 49.31) * mm});
            skLineSegment(sketch, "E1264", {"start": v(-10.77, 49.31) * mm, "end": v(-10.44, 49.14) * mm});
            skLineSegment(sketch, "E1265", {"start": v(-10.44, 49.14) * mm, "end": v(-10.1, 48.96) * mm});
            skLineSegment(sketch, "E1266", {"start": v(-10.1, 48.96) * mm, "end": v(-9.78, 48.77) * mm});
            skLineSegment(sketch, "E1267", {"start": v(-9.78, 48.77) * mm, "end": v(-9.45, 48.57) * mm});
            skLineSegment(sketch, "E1268", {"start": v(-9.45, 48.57) * mm, "end": v(-9.12, 48.35) * mm});
            skLineSegment(sketch, "E1269", {"start": v(-9.12, 48.35) * mm, "end": v(-8.8, 48.13) * mm});
            skLineSegment(sketch, "E1270", {"start": v(-8.8, 48.13) * mm, "end": v(-8.47, 47.9) * mm});
            skLineSegment(sketch, "E1271", {"start": v(-8.47, 47.9) * mm, "end": v(-8.15, 47.65) * mm});
            skLineSegment(sketch, "E1272", {"start": v(-8.15, 47.65) * mm, "end": v(-8.15, 51.04) * mm});
            skLineSegment(sketch, "E1273", {"start": v(-8.15, 51.04) * mm, "end": v(-8.14, 51.3) * mm});
            skLineSegment(sketch, "E1274", {"start": v(-8.14, 51.3) * mm, "end": v(-8.1, 51.55) * mm});
            skLineSegment(sketch, "E1275", {"start": v(-8.1, 51.55) * mm, "end": v(-8.03, 51.8) * mm});
            skLineSegment(sketch, "E1276", {"start": v(-8.03, 51.8) * mm, "end": v(-7.95, 52.03) * mm});
            skLineSegment(sketch, "E1277", {"start": v(-7.95, 52.03) * mm, "end": v(-7.84, 52.25) * mm});
            skLineSegment(sketch, "E1278", {"start": v(-7.84, 52.25) * mm, "end": v(-7.71, 52.46) * mm});
            skLineSegment(sketch, "E1279", {"start": v(-7.71, 52.46) * mm, "end": v(-7.57, 52.65) * mm});
            skLineSegment(sketch, "E1280", {"start": v(-7.57, 52.65) * mm, "end": v(-7.4, 52.83) * mm});
            skLineSegment(sketch, "E1281", {"start": v(-7.4, 52.83) * mm, "end": v(-7.22, 53) * mm});
            skLineSegment(sketch, "E1282", {"start": v(-7.22, 53) * mm, "end": v(-7.03, 53.15) * mm});
            skLineSegment(sketch, "E1283", {"start": v(-7.03, 53.15) * mm, "end": v(-6.82, 53.27) * mm});
            skLineSegment(sketch, "E1284", {"start": v(-6.82, 53.27) * mm, "end": v(-6.6, 53.38) * mm});
            skLineSegment(sketch, "E1285", {"start": v(-6.6, 53.38) * mm, "end": v(-6.36, 53.47) * mm});
            skLineSegment(sketch, "E1286", {"start": v(-6.36, 53.47) * mm, "end": v(-6.12, 53.53) * mm});
            skLineSegment(sketch, "E1287", {"start": v(-6.12, 53.53) * mm, "end": v(-5.87, 53.57) * mm});
            skLineSegment(sketch, "E1288", {"start": v(-5.87, 53.57) * mm, "end": v(-5.6, 53.58) * mm});
            skLineSegment(sketch, "E1289", {"start": v(-5.6, 53.58) * mm, "end": v(-5.27, 53.58) * mm});
            skLineSegment(sketch, "E1290", {"start": v(-5.27, 53.58) * mm, "end": v(-5.58, 53.86) * mm});
            skLineSegment(sketch, "E1291", {"start": v(-5.58, 53.86) * mm, "end": v(-5.86, 54.15) * mm});
            skLineSegment(sketch, "E1292", {"start": v(-5.86, 54.15) * mm, "end": v(-6.14, 54.46) * mm});
            skLineSegment(sketch, "E1293", {"start": v(-6.14, 54.46) * mm, "end": v(-6.4, 54.79) * mm});
            skLineSegment(sketch, "E1294", {"start": v(-6.4, 54.79) * mm, "end": v(-6.63, 55.12) * mm});
            skLineSegment(sketch, "E1295", {"start": v(-6.63, 55.12) * mm, "end": v(-6.85, 55.47) * mm});
            skLineSegment(sketch, "E1296", {"start": v(-6.85, 55.47) * mm, "end": v(-7.06, 55.83) * mm});
            skLineSegment(sketch, "E1297", {"start": v(-7.06, 55.83) * mm, "end": v(-7.24, 56.2) * mm});
            skLineSegment(sketch, "E1298", {"start": v(-7.24, 56.2) * mm, "end": v(-7.4, 56.6) * mm});
            skLineSegment(sketch, "E1299", {"start": v(-7.4, 56.6) * mm, "end": v(-7.55, 56.99) * mm});
            skLineSegment(sketch, "E1300", {"start": v(-7.55, 56.99) * mm, "end": v(-7.68, 57.39) * mm});
            skLineSegment(sketch, "E1301", {"start": v(-7.68, 57.39) * mm, "end": v(-7.78, 57.8) * mm});
            skLineSegment(sketch, "E1302", {"start": v(-7.78, 57.8) * mm, "end": v(-7.87, 58.22) * mm});
            skLineSegment(sketch, "E1303", {"start": v(-7.87, 58.22) * mm, "end": v(-7.92, 58.65) * mm});
            skLineSegment(sketch, "E1304", {"start": v(-7.92, 58.65) * mm, "end": v(-7.96, 59.09) * mm});
            skLineSegment(sketch, "E1305", {"start": v(-7.96, 59.09) * mm, "end": v(-7.97, 59.53) * mm});
            skLineSegment(sketch, "E1306", {"start": v(-7.97, 59.53) * mm, "end": v(-7.96, 59.93) * mm});
            skLineSegment(sketch, "E1307", {"start": v(-7.96, 59.93) * mm, "end": v(-7.93, 60.33) * mm});
            skLineSegment(sketch, "E1308", {"start": v(-7.93, 60.33) * mm, "end": v(-7.88, 60.73) * mm});
            skLineSegment(sketch, "E1309", {"start": v(-7.88, 60.73) * mm, "end": v(-7.81, 61.12) * mm});
            skLineSegment(sketch, "E1310", {"start": v(-7.81, 61.12) * mm, "end": v(-7.72, 61.5) * mm});
            skLineSegment(sketch, "E1311", {"start": v(-7.72, 61.5) * mm, "end": v(-7.62, 61.88) * mm});
            skLineSegment(sketch, "E1312", {"start": v(-7.62, 61.88) * mm, "end": v(-7.5, 62.24) * mm});
            skLineSegment(sketch, "E1313", {"start": v(-7.5, 62.24) * mm, "end": v(-7.35, 62.6) * mm});
            skLineSegment(sketch, "E1314", {"start": v(-7.35, 62.6) * mm, "end": v(-7.2, 62.95) * mm});
            skLineSegment(sketch, "E1315", {"start": v(-7.2, 62.95) * mm, "end": v(-7.02, 63.3) * mm});
            skLineSegment(sketch, "E1316", {"start": v(-7.02, 63.3) * mm, "end": v(-6.83, 63.62) * mm});
            skLineSegment(sketch, "E1317", {"start": v(-6.83, 63.62) * mm, "end": v(-6.62, 63.94) * mm});
            skLineSegment(sketch, "E1318", {"start": v(-6.62, 63.94) * mm, "end": v(-6.4, 64.25) * mm});
            skLineSegment(sketch, "E1319", {"start": v(-6.4, 64.25) * mm, "end": v(-6.17, 64.55) * mm});
            skLineSegment(sketch, "E1320", {"start": v(-6.17, 64.55) * mm, "end": v(-5.92, 64.84) * mm});
            skLineSegment(sketch, "E1321", {"start": v(-5.92, 64.84) * mm, "end": v(-5.66, 65.11) * mm});
            skLineSegment(sketch, "E1322", {"start": v(-5.66, 65.11) * mm, "end": v(-5.38, 65.38) * mm});
            skLineSegment(sketch, "E1323", {"start": v(-5.38, 65.38) * mm, "end": v(-5.1, 65.62) * mm});
            skLineSegment(sketch, "E1324", {"start": v(-5.1, 65.62) * mm, "end": v(-4.8, 65.86) * mm});
            skLineSegment(sketch, "E1325", {"start": v(-4.8, 65.86) * mm, "end": v(-4.49, 66.08) * mm});
            skLineSegment(sketch, "E1326", {"start": v(-4.49, 66.08) * mm, "end": v(-4.17, 66.28) * mm});
            skLineSegment(sketch, "E1327", {"start": v(-4.17, 66.28) * mm, "end": v(-3.84, 66.47) * mm});
            skLineSegment(sketch, "E1328", {"start": v(-3.84, 66.47) * mm, "end": v(-3.5, 66.65) * mm});
            skLineSegment(sketch, "E1329", {"start": v(-3.5, 66.65) * mm, "end": v(-3.15, 66.8) * mm});
            skLineSegment(sketch, "E1330", {"start": v(-3.15, 66.8) * mm, "end": v(-2.79, 66.95) * mm});
            skLineSegment(sketch, "E1331", {"start": v(-2.79, 66.95) * mm, "end": v(-2.42, 67.07) * mm});
            skLineSegment(sketch, "E1332", {"start": v(-2.42, 67.07) * mm, "end": v(-2.05, 67.18) * mm});
            skLineSegment(sketch, "E1333", {"start": v(-2.05, 67.18) * mm, "end": v(-1.66, 67.27) * mm});
            skLineSegment(sketch, "E1334", {"start": v(-1.66, 67.27) * mm, "end": v(-1.28, 67.34) * mm});
            skLineSegment(sketch, "E1335", {"start": v(-1.28, 67.34) * mm, "end": v(-0.88, 67.39) * mm});
            skLineSegment(sketch, "E1336", {"start": v(-0.88, 67.39) * mm, "end": v(-0.48, 67.42) * mm});
            skLineSegment(sketch, "E1337", {"start": v(-0.48, 67.42) * mm, "end": v(-0.07, 67.43) * mm});
            skLineSegment(sketch, "E1338", {"start": v(-0.07, 63.62) * mm, "end": v(0.14, 63.61) * mm});
            skLineSegment(sketch, "E1339", {"start": v(0.14, 63.61) * mm, "end": v(0.35, 63.6) * mm});
            skLineSegment(sketch, "E1340", {"start": v(0.35, 63.6) * mm, "end": v(0.55, 63.57) * mm});
            skLineSegment(sketch, "E1341", {"start": v(0.55, 63.57) * mm, "end": v(0.75, 63.53) * mm});
            skLineSegment(sketch, "E1342", {"start": v(0.75, 63.53) * mm, "end": v(0.95, 63.49) * mm});
            skLineSegment(sketch, "E1343", {"start": v(0.95, 63.49) * mm, "end": v(1.14, 63.43) * mm});
            skLineSegment(sketch, "E1344", {"start": v(1.14, 63.43) * mm, "end": v(1.33, 63.37) * mm});
            skLineSegment(sketch, "E1345", {"start": v(1.33, 63.37) * mm, "end": v(1.52, 63.3) * mm});
            skLineSegment(sketch, "E1346", {"start": v(1.52, 63.3) * mm, "end": v(1.7, 63.21) * mm});
            skLineSegment(sketch, "E1347", {"start": v(1.7, 63.21) * mm, "end": v(1.88, 63.12) * mm});
            skLineSegment(sketch, "E1348", {"start": v(1.88, 63.12) * mm, "end": v(2.05, 63.03) * mm});
            skLineSegment(sketch, "E1349", {"start": v(2.05, 63.03) * mm, "end": v(2.21, 62.92) * mm});
            skLineSegment(sketch, "E1350", {"start": v(2.21, 62.92) * mm, "end": v(2.38, 62.8) * mm});
            skLineSegment(sketch, "E1351", {"start": v(2.38, 62.8) * mm, "end": v(2.53, 62.68) * mm});
            skLineSegment(sketch, "E1352", {"start": v(2.53, 62.68) * mm, "end": v(2.68, 62.55) * mm});
            skLineSegment(sketch, "E1353", {"start": v(2.68, 62.55) * mm, "end": v(2.82, 62.42) * mm});
            skLineSegment(sketch, "E1354", {"start": v(2.82, 62.42) * mm, "end": v(2.96, 62.28) * mm});
            skLineSegment(sketch, "E1355", {"start": v(2.96, 62.28) * mm, "end": v(3.08, 62.13) * mm});
            skLineSegment(sketch, "E1356", {"start": v(3.08, 62.13) * mm, "end": v(3.2, 61.97) * mm});
            skLineSegment(sketch, "E1357", {"start": v(3.2, 61.97) * mm, "end": v(3.32, 61.81) * mm});
            skLineSegment(sketch, "E1358", {"start": v(3.32, 61.81) * mm, "end": v(3.43, 61.65) * mm});
            skLineSegment(sketch, "E1359", {"start": v(3.43, 61.65) * mm, "end": v(3.52, 61.48) * mm});
            skLineSegment(sketch, "E1360", {"start": v(3.52, 61.48) * mm, "end": v(3.61, 61.3) * mm});
            skLineSegment(sketch, "E1361", {"start": v(3.61, 61.3) * mm, "end": v(3.7, 61.12) * mm});
            skLineSegment(sketch, "E1362", {"start": v(3.7, 61.12) * mm, "end": v(3.77, 60.93) * mm});
            skLineSegment(sketch, "E1363", {"start": v(3.77, 60.93) * mm, "end": v(3.83, 60.74) * mm});
            skLineSegment(sketch, "E1364", {"start": v(3.83, 60.74) * mm, "end": v(3.89, 60.55) * mm});
            skLineSegment(sketch, "E1365", {"start": v(3.89, 60.55) * mm, "end": v(3.94, 60.35) * mm});
            skLineSegment(sketch, "E1366", {"start": v(3.94, 60.35) * mm, "end": v(3.97, 60.15) * mm});
            skLineSegment(sketch, "E1367", {"start": v(3.97, 60.15) * mm, "end": v(4, 59.95) * mm});
            skLineSegment(sketch, "E1368", {"start": v(4, 59.95) * mm, "end": v(4.01, 59.74) * mm});
            skLineSegment(sketch, "E1369", {"start": v(4.01, 59.74) * mm, "end": v(4.02, 59.53) * mm});
            skLineSegment(sketch, "E1370", {"start": v(4.02, 59.53) * mm, "end": v(4.01, 59.32) * mm});
            skLineSegment(sketch, "E1371", {"start": v(4.01, 59.32) * mm, "end": v(4, 59.1) * mm});
            skLineSegment(sketch, "E1372", {"start": v(4, 59.1) * mm, "end": v(3.97, 58.9) * mm});
            skLineSegment(sketch, "E1373", {"start": v(3.97, 58.9) * mm, "end": v(3.94, 58.7) * mm});
            skLineSegment(sketch, "E1374", {"start": v(3.94, 58.7) * mm, "end": v(3.89, 58.5) * mm});
            skLineSegment(sketch, "E1375", {"start": v(3.89, 58.5) * mm, "end": v(3.83, 58.31) * mm});
            skLineSegment(sketch, "E1376", {"start": v(3.83, 58.31) * mm, "end": v(3.77, 58.12) * mm});
            skLineSegment(sketch, "E1377", {"start": v(3.77, 58.12) * mm, "end": v(3.7, 57.93) * mm});
            skLineSegment(sketch, "E1378", {"start": v(3.7, 57.93) * mm, "end": v(3.61, 57.75) * mm});
            skLineSegment(sketch, "E1379", {"start": v(3.61, 57.75) * mm, "end": v(3.52, 57.58) * mm});
            skLineSegment(sketch, "E1380", {"start": v(3.52, 57.58) * mm, "end": v(3.43, 57.4) * mm});
            skLineSegment(sketch, "E1381", {"start": v(3.43, 57.4) * mm, "end": v(3.32, 57.24) * mm});
            skLineSegment(sketch, "E1382", {"start": v(3.32, 57.24) * mm, "end": v(3.2, 57.08) * mm});
            skLineSegment(sketch, "E1383", {"start": v(3.2, 57.08) * mm, "end": v(3.08, 56.93) * mm});
            skLineSegment(sketch, "E1384", {"start": v(3.08, 56.93) * mm, "end": v(2.96, 56.78) * mm});
            skLineSegment(sketch, "E1385", {"start": v(2.96, 56.78) * mm, "end": v(2.82, 56.63) * mm});
            skLineSegment(sketch, "E1386", {"start": v(2.82, 56.63) * mm, "end": v(2.68, 56.5) * mm});
            skLineSegment(sketch, "E1387", {"start": v(2.68, 56.5) * mm, "end": v(2.53, 56.37) * mm});
            skLineSegment(sketch, "E1388", {"start": v(2.53, 56.37) * mm, "end": v(2.38, 56.25) * mm});
            skLineSegment(sketch, "E1389", {"start": v(2.38, 56.25) * mm, "end": v(2.21, 56.14) * mm});
            skLineSegment(sketch, "E1390", {"start": v(2.21, 56.14) * mm, "end": v(2.05, 56.03) * mm});
            skLineSegment(sketch, "E1391", {"start": v(2.05, 56.03) * mm, "end": v(1.88, 55.93) * mm});
            skLineSegment(sketch, "E1392", {"start": v(1.88, 55.93) * mm, "end": v(1.7, 55.84) * mm});
            skLineSegment(sketch, "E1393", {"start": v(1.7, 55.84) * mm, "end": v(1.52, 55.76) * mm});
            skLineSegment(sketch, "E1394", {"start": v(1.52, 55.76) * mm, "end": v(1.33, 55.68) * mm});
            skLineSegment(sketch, "E1395", {"start": v(1.33, 55.68) * mm, "end": v(1.14, 55.62) * mm});
            skLineSegment(sketch, "E1396", {"start": v(1.14, 55.62) * mm, "end": v(0.95, 55.57) * mm});
            skLineSegment(sketch, "E1397", {"start": v(0.95, 55.57) * mm, "end": v(0.75, 55.52) * mm});
            skLineSegment(sketch, "E1398", {"start": v(0.75, 55.52) * mm, "end": v(0.55, 55.48) * mm});
            skLineSegment(sketch, "E1399", {"start": v(0.55, 55.48) * mm, "end": v(0.35, 55.46) * mm});
            skLineSegment(sketch, "E1400", {"start": v(0.35, 55.46) * mm, "end": v(0.14, 55.44) * mm});
            skLineSegment(sketch, "E1401", {"start": v(0.14, 55.44) * mm, "end": v(-0.07, 55.44) * mm});
            skLineSegment(sketch, "E1402", {"start": v(-0.07, 55.44) * mm, "end": v(-0.28, 55.44) * mm});
            skLineSegment(sketch, "E1403", {"start": v(-0.28, 55.44) * mm, "end": v(-0.5, 55.46) * mm});
            skLineSegment(sketch, "E1404", {"start": v(-0.5, 55.46) * mm, "end": v(-0.7, 55.48) * mm});
            skLineSegment(sketch, "E1405", {"start": v(-0.7, 55.48) * mm, "end": v(-0.9, 55.52) * mm});
            skLineSegment(sketch, "E1406", {"start": v(-0.9, 55.52) * mm, "end": v(-1.1, 55.57) * mm});
            skLineSegment(sketch, "E1407", {"start": v(-1.1, 55.57) * mm, "end": v(-1.29, 55.62) * mm});
            skLineSegment(sketch, "E1408", {"start": v(-1.29, 55.62) * mm, "end": v(-1.48, 55.68) * mm});
            skLineSegment(sketch, "E1409", {"start": v(-1.48, 55.68) * mm, "end": v(-1.66, 55.76) * mm});
            skLineSegment(sketch, "E1410", {"start": v(-1.66, 55.76) * mm, "end": v(-1.85, 55.84) * mm});
            skLineSegment(sketch, "E1411", {"start": v(-1.85, 55.84) * mm, "end": v(-2.02, 55.93) * mm});
            skLineSegment(sketch, "E1412", {"start": v(-2.02, 55.93) * mm, "end": v(-2.2, 56.03) * mm});
            skLineSegment(sketch, "E1413", {"start": v(-2.2, 56.03) * mm, "end": v(-2.36, 56.14) * mm});
            skLineSegment(sketch, "E1414", {"start": v(-2.36, 56.14) * mm, "end": v(-2.52, 56.25) * mm});
            skLineSegment(sketch, "E1415", {"start": v(-2.52, 56.25) * mm, "end": v(-2.67, 56.37) * mm});
            skLineSegment(sketch, "E1416", {"start": v(-2.67, 56.37) * mm, "end": v(-2.82, 56.5) * mm});
            skLineSegment(sketch, "E1417", {"start": v(-2.82, 56.5) * mm, "end": v(-2.96, 56.63) * mm});
            skLineSegment(sketch, "E1418", {"start": v(-2.96, 56.63) * mm, "end": v(-3.1, 56.78) * mm});
            skLineSegment(sketch, "E1419", {"start": v(-3.1, 56.78) * mm, "end": v(-3.23, 56.93) * mm});
            skLineSegment(sketch, "E1420", {"start": v(-3.23, 56.93) * mm, "end": v(-3.35, 57.08) * mm});
            skLineSegment(sketch, "E1421", {"start": v(-3.35, 57.08) * mm, "end": v(-3.46, 57.24) * mm});
            skLineSegment(sketch, "E1422", {"start": v(-3.46, 57.24) * mm, "end": v(-3.57, 57.4) * mm});
            skLineSegment(sketch, "E1423", {"start": v(-3.57, 57.4) * mm, "end": v(-3.67, 57.58) * mm});
            skLineSegment(sketch, "E1424", {"start": v(-3.67, 57.58) * mm, "end": v(-3.76, 57.75) * mm});
            skLineSegment(sketch, "E1425", {"start": v(-3.76, 57.75) * mm, "end": v(-3.84, 57.93) * mm});
            skLineSegment(sketch, "E1426", {"start": v(-3.84, 57.93) * mm, "end": v(-3.91, 58.12) * mm});
            skLineSegment(sketch, "E1427", {"start": v(-3.91, 58.12) * mm, "end": v(-3.98, 58.31) * mm});
            skLineSegment(sketch, "E1428", {"start": v(-3.98, 58.31) * mm, "end": v(-4.03, 58.5) * mm});
            skLineSegment(sketch, "E1429", {"start": v(-4.03, 58.5) * mm, "end": v(-4.08, 58.7) * mm});
            skLineSegment(sketch, "E1430", {"start": v(-4.08, 58.7) * mm, "end": v(-4.12, 58.9) * mm});
            skLineSegment(sketch, "E1431", {"start": v(-4.12, 58.9) * mm, "end": v(-4.14, 59.1) * mm});
            skLineSegment(sketch, "E1432", {"start": v(-4.14, 59.1) * mm, "end": v(-4.16, 59.32) * mm});
            skLineSegment(sketch, "E1433", {"start": v(-4.16, 59.32) * mm, "end": v(-4.16, 59.53) * mm});
            skLineSegment(sketch, "E1434", {"start": v(-4.16, 59.53) * mm, "end": v(-4.16, 59.74) * mm});
            skLineSegment(sketch, "E1435", {"start": v(-4.16, 59.74) * mm, "end": v(-4.14, 59.95) * mm});
            skLineSegment(sketch, "E1436", {"start": v(-4.14, 59.95) * mm, "end": v(-4.12, 60.15) * mm});
            skLineSegment(sketch, "E1437", {"start": v(-4.12, 60.15) * mm, "end": v(-4.08, 60.35) * mm});
            skLineSegment(sketch, "E1438", {"start": v(-4.08, 60.35) * mm, "end": v(-4.03, 60.55) * mm});
            skLineSegment(sketch, "E1439", {"start": v(-4.03, 60.55) * mm, "end": v(-3.98, 60.74) * mm});
            skLineSegment(sketch, "E1440", {"start": v(-3.98, 60.74) * mm, "end": v(-3.91, 60.93) * mm});
            skLineSegment(sketch, "E1441", {"start": v(-3.91, 60.93) * mm, "end": v(-3.84, 61.12) * mm});
            skLineSegment(sketch, "E1442", {"start": v(-3.84, 61.12) * mm, "end": v(-3.76, 61.3) * mm});
            skLineSegment(sketch, "E1443", {"start": v(-3.76, 61.3) * mm, "end": v(-3.67, 61.48) * mm});
            skLineSegment(sketch, "E1444", {"start": v(-3.67, 61.48) * mm, "end": v(-3.57, 61.65) * mm});
            skLineSegment(sketch, "E1445", {"start": v(-3.57, 61.65) * mm, "end": v(-3.46, 61.81) * mm});
            skLineSegment(sketch, "E1446", {"start": v(-3.46, 61.81) * mm, "end": v(-3.35, 61.97) * mm});
            skLineSegment(sketch, "E1447", {"start": v(-3.35, 61.97) * mm, "end": v(-3.23, 62.13) * mm});
            skLineSegment(sketch, "E1448", {"start": v(-3.23, 62.13) * mm, "end": v(-3.1, 62.28) * mm});
            skLineSegment(sketch, "E1449", {"start": v(-3.1, 62.28) * mm, "end": v(-2.96, 62.42) * mm});
            skLineSegment(sketch, "E1450", {"start": v(-2.96, 62.42) * mm, "end": v(-2.82, 62.55) * mm});
            skLineSegment(sketch, "E1451", {"start": v(-2.82, 62.55) * mm, "end": v(-2.67, 62.68) * mm});
            skLineSegment(sketch, "E1452", {"start": v(-2.67, 62.68) * mm, "end": v(-2.52, 62.8) * mm});
            skLineSegment(sketch, "E1453", {"start": v(-2.52, 62.8) * mm, "end": v(-2.36, 62.92) * mm});
            skLineSegment(sketch, "E1454", {"start": v(-2.36, 62.92) * mm, "end": v(-2.2, 63.03) * mm});
            skLineSegment(sketch, "E1455", {"start": v(-2.2, 63.03) * mm, "end": v(-2.02, 63.12) * mm});
            skLineSegment(sketch, "E1456", {"start": v(-2.02, 63.12) * mm, "end": v(-1.85, 63.21) * mm});
            skLineSegment(sketch, "E1457", {"start": v(-1.85, 63.21) * mm, "end": v(-1.66, 63.3) * mm});
            skLineSegment(sketch, "E1458", {"start": v(-1.66, 63.3) * mm, "end": v(-1.48, 63.37) * mm});
            skLineSegment(sketch, "E1459", {"start": v(-1.48, 63.37) * mm, "end": v(-1.29, 63.43) * mm});
            skLineSegment(sketch, "E1460", {"start": v(-1.29, 63.43) * mm, "end": v(-1.1, 63.49) * mm});
            skLineSegment(sketch, "E1461", {"start": v(-1.1, 63.49) * mm, "end": v(-0.9, 63.53) * mm});
            skLineSegment(sketch, "E1462", {"start": v(-0.9, 63.53) * mm, "end": v(-0.7, 63.57) * mm});
            skLineSegment(sketch, "E1463", {"start": v(-0.7, 63.57) * mm, "end": v(-0.5, 63.6) * mm});
            skLineSegment(sketch, "E1464", {"start": v(-0.5, 63.6) * mm, "end": v(-0.28, 63.61) * mm});
            skLineSegment(sketch, "E1465", {"start": v(-0.28, 63.61) * mm, "end": v(-0.07, 63.62) * mm});
            skLineSegment(sketch, "E1466", {"start": v(-9.63, 27.14) * mm, "end": v(-9.85, 26.84) * mm});
            skLineSegment(sketch, "E1467", {"start": v(-9.85, 26.84) * mm, "end": v(-10.07, 26.57) * mm});
            skLineSegment(sketch, "E1468", {"start": v(-10.07, 26.57) * mm, "end": v(-10.3, 26.3) * mm});
            skLineSegment(sketch, "E1469", {"start": v(-10.3, 26.3) * mm, "end": v(-10.54, 26.06) * mm});
            skLineSegment(sketch, "E1470", {"start": v(-10.54, 26.06) * mm, "end": v(-10.79, 25.84) * mm});
            skLineSegment(sketch, "E1471", {"start": v(-10.79, 25.84) * mm, "end": v(-11.04, 25.62) * mm});
            skLineSegment(sketch, "E1472", {"start": v(-11.04, 25.62) * mm, "end": v(-11.3, 25.43) * mm});
            skLineSegment(sketch, "E1473", {"start": v(-11.3, 25.43) * mm, "end": v(-11.57, 25.24) * mm});
            skLineSegment(sketch, "E1474", {"start": v(-11.57, 25.24) * mm, "end": v(-11.84, 25.07) * mm});
            skLineSegment(sketch, "E1475", {"start": v(-11.84, 25.07) * mm, "end": v(-12.12, 24.91) * mm});
            skLineSegment(sketch, "E1476", {"start": v(-12.12, 24.91) * mm, "end": v(-12.4, 24.77) * mm});
            skLineSegment(sketch, "E1477", {"start": v(-12.4, 24.77) * mm, "end": v(-12.7, 24.63) * mm});
            skLineSegment(sketch, "E1478", {"start": v(-12.7, 24.63) * mm, "end": v(-13, 24.5) * mm});
            skLineSegment(sketch, "E1479", {"start": v(-13, 24.5) * mm, "end": v(-13.3, 24.38) * mm});
            skLineSegment(sketch, "E1480", {"start": v(-13.3, 24.38) * mm, "end": v(-13.61, 24.27) * mm});
            skLineSegment(sketch, "E1481", {"start": v(-13.61, 24.27) * mm, "end": v(-13.93, 24.17) * mm});
            skLineSegment(sketch, "E1482", {"start": v(-13.93, 24.17) * mm, "end": v(-14.57, 23.99) * mm});
            skLineSegment(sketch, "E1483", {"start": v(-14.57, 23.99) * mm, "end": v(-15.24, 23.82) * mm});
            skLineSegment(sketch, "E1484", {"start": v(-15.24, 23.82) * mm, "end": v(-15.92, 23.68) * mm});
            skLineSegment(sketch, "E1485", {"start": v(-15.92, 23.68) * mm, "end": v(-16.62, 23.54) * mm});
            skLineSegment(sketch, "E1486", {"start": v(-16.62, 23.54) * mm, "end": v(-18.06, 23.26) * mm});
            skLineSegment(sketch, "E1487", {"start": v(-18.06, 23.26) * mm, "end": v(-18.8, 23.1) * mm});
            skLineSegment(sketch, "E1488", {"start": v(-18.8, 23.1) * mm, "end": v(-19.55, 22.94) * mm});
            skLineSegment(sketch, "E1489", {"start": v(-19.55, 22.94) * mm, "end": v(-20.3, 22.75) * mm});
            skLineSegment(sketch, "E1490", {"start": v(-20.3, 22.75) * mm, "end": v(-21.07, 22.53) * mm});
            skLineSegment(sketch, "E1491", {"start": v(-21.07, 22.53) * mm, "end": v(-21.46, 22.41) * mm});
            skLineSegment(sketch, "E1492", {"start": v(-21.46, 22.41) * mm, "end": v(-21.84, 22.28) * mm});
            skLineSegment(sketch, "E1493", {"start": v(-21.84, 22.28) * mm, "end": v(-22.23, 22.14) * mm});
            skLineSegment(sketch, "E1494", {"start": v(-22.23, 22.14) * mm, "end": v(-22.62, 22) * mm});
            skLineSegment(sketch, "E1495", {"start": v(-22.62, 22) * mm, "end": v(-23, 21.83) * mm});
            skLineSegment(sketch, "E1496", {"start": v(-23, 21.83) * mm, "end": v(-23.4, 21.66) * mm});
            skLineSegment(sketch, "E1497", {"start": v(-23.4, 21.66) * mm, "end": v(-23.78, 21.47) * mm});
            skLineSegment(sketch, "E1498", {"start": v(-23.78, 21.47) * mm, "end": v(-24.17, 21.26) * mm});
            skLineSegment(sketch, "E1499", {"start": v(-24.17, 21.26) * mm, "end": v(-24.56, 21.05) * mm});
            skLineSegment(sketch, "E1500", {"start": v(-24.56, 21.05) * mm, "end": v(-24.95, 20.82) * mm});
            skLineSegment(sketch, "E1501", {"start": v(-24.95, 20.82) * mm, "end": v(-25.34, 20.57) * mm});
            skLineSegment(sketch, "E1502", {"start": v(-25.34, 20.57) * mm, "end": v(-25.73, 20.3) * mm});
            skLineSegment(sketch, "E1503", {"start": v(-25.73, 20.3) * mm, "end": v(-26.12, 20.02) * mm});
            skLineSegment(sketch, "E1504", {"start": v(-26.12, 20.02) * mm, "end": v(-26.5, 19.72) * mm});
            skLineSegment(sketch, "E1505", {"start": v(-26.5, 19.72) * mm, "end": v(-26.89, 19.4) * mm});
            skLineSegment(sketch, "E1506", {"start": v(-26.89, 19.4) * mm, "end": v(-27.27, 19.06) * mm});
            skLineSegment(sketch, "E1507", {"start": v(-27.27, 19.06) * mm, "end": v(-27.65, 18.7) * mm});
            skLineSegment(sketch, "E1508", {"start": v(-27.65, 18.7) * mm, "end": v(-28.03, 18.31) * mm});
            skLineSegment(sketch, "E1509", {"start": v(-28.03, 18.31) * mm, "end": v(-28.4, 17.9) * mm});
            skLineSegment(sketch, "E1510", {"start": v(-28.4, 17.9) * mm, "end": v(-28.78, 17.48) * mm});
            skLineSegment(sketch, "E1511", {"start": v(-28.78, 17.48) * mm, "end": v(-29.16, 17.02) * mm});
            skLineSegment(sketch, "E1512", {"start": v(-29.16, 17.02) * mm, "end": v(-29.53, 16.55) * mm});
            skLineSegment(sketch, "E1513", {"start": v(-29.53, 16.55) * mm, "end": v(-29.9, 16.04) * mm});
            skLineSegment(sketch, "E1514", {"start": v(-29.9, 16.04) * mm, "end": v(-30.26, 15.52) * mm});
            skLineSegment(sketch, "E1515", {"start": v(-30.26, 15.52) * mm, "end": v(-30.62, 14.96) * mm});
            skLineSegment(sketch, "E1516", {"start": v(-30.62, 14.96) * mm, "end": v(-30.98, 14.38) * mm});
            skLineSegment(sketch, "E1517", {"start": v(-30.98, 14.38) * mm, "end": v(-31.34, 13.77) * mm});
            skLineSegment(sketch, "E1518", {"start": v(-31.34, 13.77) * mm, "end": v(-31.69, 13.12) * mm});
            skLineSegment(sketch, "E1519", {"start": v(-31.69, 13.12) * mm, "end": v(-32.53, 11.52) * mm});
            skLineSegment(sketch, "E1520", {"start": v(-32.53, 11.52) * mm, "end": v(-33.33, 10) * mm});
            skLineSegment(sketch, "E1521", {"start": v(-33.33, 10) * mm, "end": v(-34.1, 8.53) * mm});
            skLineSegment(sketch, "E1522", {"start": v(-34.1, 8.53) * mm, "end": v(-34.5, 7.82) * mm});
            skLineSegment(sketch, "E1523", {"start": v(-34.5, 7.82) * mm, "end": v(-34.89, 7.13) * mm});
            skLineSegment(sketch, "E1524", {"start": v(-34.89, 7.13) * mm, "end": v(-35.29, 6.44) * mm});
            skLineSegment(sketch, "E1525", {"start": v(-35.29, 6.44) * mm, "end": v(-35.7, 5.77) * mm});
            skLineSegment(sketch, "E1526", {"start": v(-35.7, 5.77) * mm, "end": v(-36.13, 5.1) * mm});
            skLineSegment(sketch, "E1527", {"start": v(-36.13, 5.1) * mm, "end": v(-36.57, 4.44) * mm});
            skLineSegment(sketch, "E1528", {"start": v(-36.57, 4.44) * mm, "end": v(-37.04, 3.8) * mm});
            skLineSegment(sketch, "E1529", {"start": v(-37.04, 3.8) * mm, "end": v(-37.53, 3.14) * mm});
            skLineSegment(sketch, "E1530", {"start": v(-37.53, 3.14) * mm, "end": v(-38.04, 2.5) * mm});
            skLineSegment(sketch, "E1531", {"start": v(-38.04, 2.5) * mm, "end": v(-38.6, 1.86) * mm});
            skLineSegment(sketch, "E1532", {"start": v(-38.6, 1.86) * mm, "end": v(-39.28, 1.1) * mm});
            skLineSegment(sketch, "E1533", {"start": v(-39.28, 1.1) * mm, "end": v(-39.9, 0.43) * mm});
            skLineSegment(sketch, "E1534", {"start": v(-39.9, 0.43) * mm, "end": v(-40.47, -0.16) * mm});
            skLineSegment(sketch, "E1535", {"start": v(-40.47, -0.16) * mm, "end": v(-41, -0.67) * mm});
            skLineSegment(sketch, "E1536", {"start": v(-41, -0.67) * mm, "end": v(-41.48, -1.1) * mm});
            skLineSegment(sketch, "E1537", {"start": v(-41.48, -1.1) * mm, "end": v(-41.93, -1.48) * mm});
            skLineSegment(sketch, "E1538", {"start": v(-41.93, -1.48) * mm, "end": v(-42.34, -1.8) * mm});
            skLineSegment(sketch, "E1539", {"start": v(-42.34, -1.8) * mm, "end": v(-42.74, -2.06) * mm});
            skLineSegment(sketch, "E1540", {"start": v(-42.74, -2.06) * mm, "end": v(-43.11, -2.29) * mm});
            skLineSegment(sketch, "E1541", {"start": v(-43.11, -2.29) * mm, "end": v(-43.48, -2.47) * mm});
            skLineSegment(sketch, "E1542", {"start": v(-43.48, -2.47) * mm, "end": v(-43.84, -2.63) * mm});
            skLineSegment(sketch, "E1543", {"start": v(-43.84, -2.63) * mm, "end": v(-44.2, -2.76) * mm});
            skLineSegment(sketch, "E1544", {"start": v(-44.2, -2.76) * mm, "end": v(-44.56, -2.88) * mm});
            skLineSegment(sketch, "E1545", {"start": v(-44.56, -2.88) * mm, "end": v(-44.94, -2.98) * mm});
            skLineSegment(sketch, "E1546", {"start": v(-44.94, -2.98) * mm, "end": v(-45.75, -3.2) * mm});
            skLineSegment(sketch, "E1547", {"start": v(-45.75, -3.2) * mm, "end": v(-45.71, -2.34) * mm});
            skLineSegment(sketch, "E1548", {"start": v(-45.71, -2.34) * mm, "end": v(-45.66, -1.5) * mm});
            skLineSegment(sketch, "E1549", {"start": v(-45.66, -1.5) * mm, "end": v(-45.58, -0.64) * mm});
            skLineSegment(sketch, "E1550", {"start": v(-45.58, -0.64) * mm, "end": v(-45.5, 0.2) * mm});
            skLineSegment(sketch, "E1551", {"start": v(-45.5, 0.2) * mm, "end": v(-45.4, 1.04) * mm});
            skLineSegment(sketch, "E1552", {"start": v(-45.4, 1.04) * mm, "end": v(-45.28, 1.87) * mm});
            skLineSegment(sketch, "E1553", {"start": v(-45.28, 1.87) * mm, "end": v(-45.14, 2.7) * mm});
            skLineSegment(sketch, "E1554", {"start": v(-45.14, 2.7) * mm, "end": v(-45, 3.52) * mm});
            skLineSegment(sketch, "E1555", {"start": v(-45, 3.52) * mm, "end": v(-44.84, 4.34) * mm});
            skLineSegment(sketch, "E1556", {"start": v(-44.84, 4.34) * mm, "end": v(-44.66, 5.15) * mm});
            skLineSegment(sketch, "E1557", {"start": v(-44.66, 5.15) * mm, "end": v(-44.47, 5.96) * mm});
            skLineSegment(sketch, "E1558", {"start": v(-44.47, 5.96) * mm, "end": v(-44.26, 6.76) * mm});
            skLineSegment(sketch, "E1559", {"start": v(-44.26, 6.76) * mm, "end": v(-44.05, 7.56) * mm});
            skLineSegment(sketch, "E1560", {"start": v(-44.05, 7.56) * mm, "end": v(-43.81, 8.35) * mm});
            skLineSegment(sketch, "E1561", {"start": v(-43.81, 8.35) * mm, "end": v(-43.57, 9.13) * mm});
            skLineSegment(sketch, "E1562", {"start": v(-43.57, 9.13) * mm, "end": v(-43.3, 9.91) * mm});
            skLineSegment(sketch, "E1563", {"start": v(-43.3, 9.91) * mm, "end": v(-43.03, 10.68) * mm});
            skLineSegment(sketch, "E1564", {"start": v(-43.03, 10.68) * mm, "end": v(-42.75, 11.45) * mm});
            skLineSegment(sketch, "E1565", {"start": v(-42.75, 11.45) * mm, "end": v(-42.44, 12.2) * mm});
            skLineSegment(sketch, "E1566", {"start": v(-42.44, 12.2) * mm, "end": v(-42.13, 12.96) * mm});
            skLineSegment(sketch, "E1567", {"start": v(-42.13, 12.96) * mm, "end": v(-41.8, 13.7) * mm});
            skLineSegment(sketch, "E1568", {"start": v(-41.8, 13.7) * mm, "end": v(-41.47, 14.44) * mm});
            skLineSegment(sketch, "E1569", {"start": v(-41.47, 14.44) * mm, "end": v(-41.11, 15.17) * mm});
            skLineSegment(sketch, "E1570", {"start": v(-41.11, 15.17) * mm, "end": v(-40.75, 15.9) * mm});
            skLineSegment(sketch, "E1571", {"start": v(-40.75, 15.9) * mm, "end": v(-40.37, 16.61) * mm});
            skLineSegment(sketch, "E1572", {"start": v(-40.37, 16.61) * mm, "end": v(-39.98, 17.32) * mm});
            skLineSegment(sketch, "E1573", {"start": v(-39.98, 17.32) * mm, "end": v(-39.58, 18.02) * mm});
            skLineSegment(sketch, "E1574", {"start": v(-39.58, 18.02) * mm, "end": v(-39.17, 18.72) * mm});
            skLineSegment(sketch, "E1575", {"start": v(-39.17, 18.72) * mm, "end": v(-38.75, 19.4) * mm});
            skLineSegment(sketch, "E1576", {"start": v(-38.75, 19.4) * mm, "end": v(-38.3, 20.08) * mm});
            skLineSegment(sketch, "E1577", {"start": v(-38.3, 20.08) * mm, "end": v(-37.86, 20.75) * mm});
            skLineSegment(sketch, "E1578", {"start": v(-37.86, 20.75) * mm, "end": v(-37.4, 21.4) * mm});
            skLineSegment(sketch, "E1579", {"start": v(-37.4, 21.4) * mm, "end": v(-36.93, 22.06) * mm});
            skLineSegment(sketch, "E1580", {"start": v(-36.93, 22.06) * mm, "end": v(-36.45, 22.7) * mm});
            skLineSegment(sketch, "E1581", {"start": v(-36.45, 22.7) * mm, "end": v(-35.96, 23.34) * mm});
            skLineSegment(sketch, "E1582", {"start": v(-35.96, 23.34) * mm, "end": v(-35.45, 23.96) * mm});
            skLineSegment(sketch, "E1583", {"start": v(-35.45, 23.96) * mm, "end": v(-34.94, 24.58) * mm});
            skLineSegment(sketch, "E1584", {"start": v(-34.94, 24.58) * mm, "end": v(-34.42, 25.19) * mm});
            skLineSegment(sketch, "E1585", {"start": v(-34.42, 25.19) * mm, "end": v(-33.88, 25.79) * mm});
            skLineSegment(sketch, "E1586", {"start": v(-33.88, 25.79) * mm, "end": v(-33.34, 26.37) * mm});
            skLineSegment(sketch, "E1587", {"start": v(-33.34, 26.37) * mm, "end": v(-32.78, 26.95) * mm});
            skLineSegment(sketch, "E1588", {"start": v(-32.78, 26.95) * mm, "end": v(-32.21, 27.52) * mm});
            skLineSegment(sketch, "E1589", {"start": v(-32.21, 27.52) * mm, "end": v(-31.64, 28.08) * mm});
            skLineSegment(sketch, "E1590", {"start": v(-31.64, 28.08) * mm, "end": v(-31.05, 28.63) * mm});
            skLineSegment(sketch, "E1591", {"start": v(-31.05, 28.63) * mm, "end": v(-30.46, 29.17) * mm});
            skLineSegment(sketch, "E1592", {"start": v(-30.46, 29.17) * mm, "end": v(-29.86, 29.7) * mm});
            skLineSegment(sketch, "E1593", {"start": v(-29.86, 29.7) * mm, "end": v(-29.24, 30.21) * mm});
            skLineSegment(sketch, "E1594", {"start": v(-29.24, 30.21) * mm, "end": v(-28.62, 30.72) * mm});
            skLineSegment(sketch, "E1595", {"start": v(-28.62, 30.72) * mm, "end": v(-27.99, 31.22) * mm});
            skLineSegment(sketch, "E1596", {"start": v(-27.99, 31.22) * mm, "end": v(-27.35, 31.7) * mm});
            skLineSegment(sketch, "E1597", {"start": v(-27.35, 31.7) * mm, "end": v(-26.7, 32.18) * mm});
            skLineSegment(sketch, "E1598", {"start": v(-26.7, 32.18) * mm, "end": v(-26.04, 32.64) * mm});
            skLineSegment(sketch, "E1599", {"start": v(-26.04, 32.64) * mm, "end": v(-25.38, 33.1) * mm});
            skLineSegment(sketch, "E1600", {"start": v(-25.38, 33.1) * mm, "end": v(-24.7, 33.53) * mm});
            skLineSegment(sketch, "E1601", {"start": v(-24.7, 33.53) * mm, "end": v(-24.02, 33.96) * mm});
            skLineSegment(sketch, "E1602", {"start": v(-24.02, 33.96) * mm, "end": v(-23.33, 34.38) * mm});
            skLineSegment(sketch, "E1603", {"start": v(-23.33, 34.38) * mm, "end": v(-22.63, 34.78) * mm});
            skLineSegment(sketch, "E1604", {"start": v(-22.63, 34.78) * mm, "end": v(-21.92, 35.18) * mm});
            skLineSegment(sketch, "E1605", {"start": v(-21.92, 35.18) * mm, "end": v(-21.2, 35.56) * mm});
            skLineSegment(sketch, "E1606", {"start": v(-21.2, 35.56) * mm, "end": v(-20.49, 35.93) * mm});
            skLineSegment(sketch, "E1607", {"start": v(-20.49, 35.93) * mm, "end": v(-19.76, 36.28) * mm});
            skLineSegment(sketch, "E1608", {"start": v(-19.76, 36.28) * mm, "end": v(-19.02, 36.63) * mm});
            skLineSegment(sketch, "E1609", {"start": v(-19.02, 36.63) * mm, "end": v(-18.28, 36.96) * mm});
            skLineSegment(sketch, "E1610", {"start": v(-18.28, 36.96) * mm, "end": v(-17.53, 37.28) * mm});
            skLineSegment(sketch, "E1611", {"start": v(-17.53, 37.28) * mm, "end": v(-17.3, 36.84) * mm});
            skLineSegment(sketch, "E1612", {"start": v(-17.3, 36.84) * mm, "end": v(-17.06, 36.4) * mm});
            skLineSegment(sketch, "E1613", {"start": v(-17.06, 36.4) * mm, "end": v(-16.8, 35.97) * mm});
            skLineSegment(sketch, "E1614", {"start": v(-16.8, 35.97) * mm, "end": v(-16.55, 35.54) * mm});
            skLineSegment(sketch, "E1615", {"start": v(-16.55, 35.54) * mm, "end": v(-16.02, 34.7) * mm});
            skLineSegment(sketch, "E1616", {"start": v(-16.02, 34.7) * mm, "end": v(-15.47, 33.87) * mm});
            skLineSegment(sketch, "E1617", {"start": v(-15.47, 33.87) * mm, "end": v(-14.9, 33.08) * mm});
            skLineSegment(sketch, "E1618", {"start": v(-14.9, 33.08) * mm, "end": v(-14.33, 32.31) * mm});
            skLineSegment(sketch, "E1619", {"start": v(-14.33, 32.31) * mm, "end": v(-13.75, 31.58) * mm});
            skLineSegment(sketch, "E1620", {"start": v(-13.75, 31.58) * mm, "end": v(-13.18, 30.89) * mm});
            skLineSegment(sketch, "E1621", {"start": v(-13.18, 30.89) * mm, "end": v(-12.63, 30.23) * mm});
            skLineSegment(sketch, "E1622", {"start": v(-12.63, 30.23) * mm, "end": v(-12.09, 29.63) * mm});
            skLineSegment(sketch, "E1623", {"start": v(-12.09, 29.63) * mm, "end": v(-11.58, 29.07) * mm});
            skLineSegment(sketch, "E1624", {"start": v(-11.58, 29.07) * mm, "end": v(-11.1, 28.56) * mm});
            skLineSegment(sketch, "E1625", {"start": v(-11.1, 28.56) * mm, "end": v(-10.66, 28.11) * mm});
            skLineSegment(sketch, "E1626", {"start": v(-10.66, 28.11) * mm, "end": v(-10.26, 27.72) * mm});
            skLineSegment(sketch, "E1627", {"start": v(-10.26, 27.72) * mm, "end": v(-9.92, 27.4) * mm});
            skLineSegment(sketch, "E1628", {"start": v(-9.92, 27.4) * mm, "end": v(-9.63, 27.14) * mm});
            skLineSegment(sketch, "E1629", {"start": v(-45.53, -9.89) * mm, "end": v(-44.88, -10.28) * mm});
            skLineSegment(sketch, "E1630", {"start": v(-44.88, -10.28) * mm, "end": v(-44.2, -10.67) * mm});
            skLineSegment(sketch, "E1631", {"start": v(-44.2, -10.67) * mm, "end": v(-43.53, -11.05) * mm});
            skLineSegment(sketch, "E1632", {"start": v(-43.53, -11.05) * mm, "end": v(-42.84, -11.42) * mm});
            skLineSegment(sketch, "E1633", {"start": v(-42.84, -11.42) * mm, "end": v(-42.15, -11.78) * mm});
            skLineSegment(sketch, "E1634", {"start": v(-42.15, -11.78) * mm, "end": v(-41.45, -12.12) * mm});
            skLineSegment(sketch, "E1635", {"start": v(-41.45, -12.12) * mm, "end": v(-40.09, -12.78) * mm});
            skLineSegment(sketch, "E1636", {"start": v(-40.09, -12.78) * mm, "end": v(-38.77, -13.38) * mm});
            skLineSegment(sketch, "E1637", {"start": v(-38.77, -13.38) * mm, "end": v(-37.55, -13.92) * mm});
            skLineSegment(sketch, "E1638", {"start": v(-37.55, -13.92) * mm, "end": v(-36.45, -14.38) * mm});
            skLineSegment(sketch, "E1639", {"start": v(-36.45, -14.38) * mm, "end": v(-35.5, -14.77) * mm});
            skLineSegment(sketch, "E1640", {"start": v(-35.5, -14.77) * mm, "end": v(-35.51, -15.77) * mm});
            skLineSegment(sketch, "E1641", {"start": v(-35.51, -15.77) * mm, "end": v(-35.5, -16.73) * mm});
            skLineSegment(sketch, "E1642", {"start": v(-35.5, -16.73) * mm, "end": v(-35.47, -17.66) * mm});
            skLineSegment(sketch, "E1643", {"start": v(-35.47, -17.66) * mm, "end": v(-35.45, -18.1) * mm});
            skLineSegment(sketch, "E1644", {"start": v(-35.45, -18.1) * mm, "end": v(-35.42, -18.54) * mm});
            skLineSegment(sketch, "E1645", {"start": v(-35.42, -18.54) * mm, "end": v(-35.38, -18.97) * mm});
            skLineSegment(sketch, "E1646", {"start": v(-35.38, -18.97) * mm, "end": v(-35.33, -19.38) * mm});
            skLineSegment(sketch, "E1647", {"start": v(-35.33, -19.38) * mm, "end": v(-35.27, -19.8) * mm});
            skLineSegment(sketch, "E1648", {"start": v(-35.27, -19.8) * mm, "end": v(-35.2, -20.2) * mm});
            skLineSegment(sketch, "E1649", {"start": v(-35.2, -20.2) * mm, "end": v(-35.13, -20.58) * mm});
            skLineSegment(sketch, "E1650", {"start": v(-35.13, -20.58) * mm, "end": v(-35.05, -20.96) * mm});
            skLineSegment(sketch, "E1651", {"start": v(-35.05, -20.96) * mm, "end": v(-34.95, -21.33) * mm});
            skLineSegment(sketch, "E1652", {"start": v(-34.95, -21.33) * mm, "end": v(-34.85, -21.7) * mm});
            skLineSegment(sketch, "E1653", {"start": v(-34.85, -21.7) * mm, "end": v(-34.73, -22.04) * mm});
            skLineSegment(sketch, "E1654", {"start": v(-34.73, -22.04) * mm, "end": v(-34.6, -22.38) * mm});
            skLineSegment(sketch, "E1655", {"start": v(-34.6, -22.38) * mm, "end": v(-34.45, -22.72) * mm});
            skLineSegment(sketch, "E1656", {"start": v(-34.45, -22.72) * mm, "end": v(-34.3, -23.04) * mm});
            skLineSegment(sketch, "E1657", {"start": v(-34.3, -23.04) * mm, "end": v(-34.13, -23.36) * mm});
            skLineSegment(sketch, "E1658", {"start": v(-34.13, -23.36) * mm, "end": v(-33.94, -23.66) * mm});
            skLineSegment(sketch, "E1659", {"start": v(-33.94, -23.66) * mm, "end": v(-33.75, -23.96) * mm});
            skLineSegment(sketch, "E1660", {"start": v(-33.75, -23.96) * mm, "end": v(-33.53, -24.24) * mm});
            skLineSegment(sketch, "E1661", {"start": v(-33.53, -24.24) * mm, "end": v(-33.3, -24.52) * mm});
            skLineSegment(sketch, "E1662", {"start": v(-33.3, -24.52) * mm, "end": v(-33.05, -24.79) * mm});
            skLineSegment(sketch, "E1663", {"start": v(-33.05, -24.79) * mm, "end": v(-32.8, -25.05) * mm});
            skLineSegment(sketch, "E1664", {"start": v(-32.8, -25.05) * mm, "end": v(-32.51, -25.3) * mm});
            skLineSegment(sketch, "E1665", {"start": v(-32.51, -25.3) * mm, "end": v(-32.21, -25.54) * mm});
            skLineSegment(sketch, "E1666", {"start": v(-32.21, -25.54) * mm, "end": v(-31.9, -25.77) * mm});
            skLineSegment(sketch, "E1667", {"start": v(-31.9, -25.77) * mm, "end": v(-31.56, -26) * mm});
            skLineSegment(sketch, "E1668", {"start": v(-31.56, -26) * mm, "end": v(-31.2, -26.21) * mm});
            skLineSegment(sketch, "E1669", {"start": v(-31.2, -26.21) * mm, "end": v(-30.68, -26.5) * mm});
            skLineSegment(sketch, "E1670", {"start": v(-30.68, -26.5) * mm, "end": v(-30.17, -26.75) * mm});
            skLineSegment(sketch, "E1671", {"start": v(-30.17, -26.75) * mm, "end": v(-29.67, -26.96) * mm});
            skLineSegment(sketch, "E1672", {"start": v(-29.67, -26.96) * mm, "end": v(-29.19, -27.13) * mm});
            skLineSegment(sketch, "E1673", {"start": v(-29.19, -27.13) * mm, "end": v(-28.72, -27.27) * mm});
            skLineSegment(sketch, "E1674", {"start": v(-28.72, -27.27) * mm, "end": v(-28.26, -27.37) * mm});
            skLineSegment(sketch, "E1675", {"start": v(-28.26, -27.37) * mm, "end": v(-27.8, -27.45) * mm});
            skLineSegment(sketch, "E1676", {"start": v(-27.8, -27.45) * mm, "end": v(-27.37, -27.5) * mm});
            skLineSegment(sketch, "E1677", {"start": v(-27.37, -27.5) * mm, "end": v(-26.94, -27.52) * mm});
            skLineSegment(sketch, "E1678", {"start": v(-26.94, -27.52) * mm, "end": v(-26.53, -27.5) * mm});
            skLineSegment(sketch, "E1679", {"start": v(-26.53, -27.5) * mm, "end": v(-26.12, -27.48) * mm});
            skLineSegment(sketch, "E1680", {"start": v(-26.12, -27.48) * mm, "end": v(-25.72, -27.42) * mm});
            skLineSegment(sketch, "E1681", {"start": v(-25.72, -27.42) * mm, "end": v(-25.33, -27.35) * mm});
            skLineSegment(sketch, "E1682", {"start": v(-25.33, -27.35) * mm, "end": v(-24.95, -27.25) * mm});
            skLineSegment(sketch, "E1683", {"start": v(-24.95, -27.25) * mm, "end": v(-24.57, -27.14) * mm});
            skLineSegment(sketch, "E1684", {"start": v(-24.57, -27.14) * mm, "end": v(-24.2, -27.01) * mm});
            skLineSegment(sketch, "E1685", {"start": v(-24.2, -27.01) * mm, "end": v(-23.84, -26.87) * mm});
            skLineSegment(sketch, "E1686", {"start": v(-23.84, -26.87) * mm, "end": v(-23.49, -26.72) * mm});
            skLineSegment(sketch, "E1687", {"start": v(-23.49, -26.72) * mm, "end": v(-23.14, -26.55) * mm});
            skLineSegment(sketch, "E1688", {"start": v(-23.14, -26.55) * mm, "end": v(-22.8, -26.38) * mm});
            skLineSegment(sketch, "E1689", {"start": v(-22.8, -26.38) * mm, "end": v(-22.12, -26) * mm});
            skLineSegment(sketch, "E1690", {"start": v(-22.12, -26) * mm, "end": v(-21.46, -25.61) * mm});
            skLineSegment(sketch, "E1691", {"start": v(-21.46, -25.61) * mm, "end": v(-20.8, -25.22) * mm});
            skLineSegment(sketch, "E1692", {"start": v(-20.8, -25.22) * mm, "end": v(-20.16, -24.83) * mm});
            skLineSegment(sketch, "E1693", {"start": v(-20.16, -24.83) * mm, "end": v(-19.53, -24.47) * mm});
            skLineSegment(sketch, "E1694", {"start": v(-19.53, -24.47) * mm, "end": v(-19.2, -24.3) * mm});
            skLineSegment(sketch, "E1695", {"start": v(-19.2, -24.3) * mm, "end": v(-18.89, -24.14) * mm});
            skLineSegment(sketch, "E1696", {"start": v(-18.89, -24.14) * mm, "end": v(-18.47, -24.31) * mm});
            skLineSegment(sketch, "E1697", {"start": v(-18.47, -24.31) * mm, "end": v(-18.03, -24.5) * mm});
            skLineSegment(sketch, "E1698", {"start": v(-18.03, -24.5) * mm, "end": v(-17.58, -24.72) * mm});
            skLineSegment(sketch, "E1699", {"start": v(-17.58, -24.72) * mm, "end": v(-17.1, -24.95) * mm});
            skLineSegment(sketch, "E1700", {"start": v(-17.1, -24.95) * mm, "end": v(-16.63, -25.2) * mm});
            skLineSegment(sketch, "E1701", {"start": v(-16.63, -25.2) * mm, "end": v(-16.14, -25.48) * mm});
            skLineSegment(sketch, "E1702", {"start": v(-16.14, -25.48) * mm, "end": v(-15.12, -26.07) * mm});
            skLineSegment(sketch, "E1703", {"start": v(-15.12, -26.07) * mm, "end": v(-13, -27.33) * mm});
            skLineSegment(sketch, "E1704", {"start": v(-13, -27.33) * mm, "end": v(-11.9, -27.98) * mm});
            skLineSegment(sketch, "E1705", {"start": v(-11.9, -27.98) * mm, "end": v(-10.8, -28.61) * mm});
            skLineSegment(sketch, "E1706", {"start": v(-10.8, -28.61) * mm, "end": v(-10.24, -28.92) * mm});
            skLineSegment(sketch, "E1707", {"start": v(-10.24, -28.92) * mm, "end": v(-9.69, -29.22) * mm});
            skLineSegment(sketch, "E1708", {"start": v(-9.69, -29.22) * mm, "end": v(-9.13, -29.5) * mm});
            skLineSegment(sketch, "E1709", {"start": v(-9.13, -29.5) * mm, "end": v(-8.58, -29.77) * mm});
            skLineSegment(sketch, "E1710", {"start": v(-8.58, -29.77) * mm, "end": v(-8.04, -30.02) * mm});
            skLineSegment(sketch, "E1711", {"start": v(-8.04, -30.02) * mm, "end": v(-7.5, -30.25) * mm});
            skLineSegment(sketch, "E1712", {"start": v(-7.5, -30.25) * mm, "end": v(-6.96, -30.46) * mm});
            skLineSegment(sketch, "E1713", {"start": v(-6.96, -30.46) * mm, "end": v(-6.43, -30.65) * mm});
            skLineSegment(sketch, "E1714", {"start": v(-6.43, -30.65) * mm, "end": v(-5.9, -30.8) * mm});
            skLineSegment(sketch, "E1715", {"start": v(-5.9, -30.8) * mm, "end": v(-5.4, -30.94) * mm});
            skLineSegment(sketch, "E1716", {"start": v(-5.4, -30.94) * mm, "end": v(-4.9, -31.04) * mm});
            skLineSegment(sketch, "E1717", {"start": v(-4.9, -31.04) * mm, "end": v(-4.64, -31.08) * mm});
            skLineSegment(sketch, "E1718", {"start": v(-4.64, -31.08) * mm, "end": v(-4.4, -31.11) * mm});
            skLineSegment(sketch, "E1719", {"start": v(-4.4, -31.11) * mm, "end": v(-4.16, -31.13) * mm});
            skLineSegment(sketch, "E1720", {"start": v(-4.16, -31.13) * mm, "end": v(-3.92, -31.15) * mm});
            skLineSegment(sketch, "E1721", {"start": v(-3.92, -31.15) * mm, "end": v(-3.68, -31.15) * mm});
            skLineSegment(sketch, "E1722", {"start": v(-3.68, -31.15) * mm, "end": v(-3.45, -31.14) * mm});
            skLineSegment(sketch, "E1723", {"start": v(-3.45, -31.14) * mm, "end": v(-3.22, -31.13) * mm});
            skLineSegment(sketch, "E1724", {"start": v(-3.22, -31.13) * mm, "end": v(-3, -31.1) * mm});
            skLineSegment(sketch, "E1725", {"start": v(-3, -31.1) * mm, "end": v(-2.77, -31.07) * mm});
            skLineSegment(sketch, "E1726", {"start": v(-2.77, -31.07) * mm, "end": v(-2.56, -31.02) * mm});
            skLineSegment(sketch, "E1727", {"start": v(-2.56, -31.02) * mm, "end": v(-2.57, -30.92) * mm});
            skLineSegment(sketch, "E1728", {"start": v(-2.57, -30.92) * mm, "end": v(-2.6, -30.75) * mm});
            skLineSegment(sketch, "E1729", {"start": v(-2.6, -30.75) * mm, "end": v(-2.73, -30.24) * mm});
            skLineSegment(sketch, "E1730", {"start": v(-2.73, -30.24) * mm, "end": v(-2.91, -29.5) * mm});
            skLineSegment(sketch, "E1731", {"start": v(-2.91, -29.5) * mm, "end": v(-3.13, -28.57) * mm});
            skLineSegment(sketch, "E1732", {"start": v(-3.13, -28.57) * mm, "end": v(-3.24, -28.03) * mm});
            skLineSegment(sketch, "E1733", {"start": v(-3.24, -28.03) * mm, "end": v(-3.36, -27.46) * mm});
            skLineSegment(sketch, "E1734", {"start": v(-3.36, -27.46) * mm, "end": v(-3.47, -26.84) * mm});
            skLineSegment(sketch, "E1735", {"start": v(-3.47, -26.84) * mm, "end": v(-3.57, -26.2) * mm});
            skLineSegment(sketch, "E1736", {"start": v(-3.57, -26.2) * mm, "end": v(-3.67, -25.52) * mm});
            skLineSegment(sketch, "E1737", {"start": v(-3.67, -25.52) * mm, "end": v(-3.75, -24.81) * mm});
            skLineSegment(sketch, "E1738", {"start": v(-3.75, -24.81) * mm, "end": v(-3.82, -24.08) * mm});
            skLineSegment(sketch, "E1739", {"start": v(-3.82, -24.08) * mm, "end": v(-3.87, -23.32) * mm});
            skLineSegment(sketch, "E1740", {"start": v(-3.87, -23.32) * mm, "end": v(-3.9, -22.55) * mm});
            skLineSegment(sketch, "E1741", {"start": v(-3.9, -22.55) * mm, "end": v(-3.91, -21.76) * mm});
            skLineSegment(sketch, "E1742", {"start": v(-3.91, -21.76) * mm, "end": v(-3.9, -20.95) * mm});
            skLineSegment(sketch, "E1743", {"start": v(-3.9, -20.95) * mm, "end": v(-3.87, -20.55) * mm});
            skLineSegment(sketch, "E1744", {"start": v(-3.87, -20.55) * mm, "end": v(-3.84, -20.14) * mm});
            skLineSegment(sketch, "E1745", {"start": v(-3.84, -20.14) * mm, "end": v(-3.8, -19.73) * mm});
            skLineSegment(sketch, "E1746", {"start": v(-3.8, -19.73) * mm, "end": v(-3.76, -19.32) * mm});
            skLineSegment(sketch, "E1747", {"start": v(-3.76, -19.32) * mm, "end": v(-3.71, -18.9) * mm});
            skLineSegment(sketch, "E1748", {"start": v(-3.71, -18.9) * mm, "end": v(-3.65, -18.49) * mm});
            skLineSegment(sketch, "E1749", {"start": v(-3.65, -18.49) * mm, "end": v(-3.58, -18.08) * mm});
            skLineSegment(sketch, "E1750", {"start": v(-3.58, -18.08) * mm, "end": v(-3.5, -17.66) * mm});
            skLineSegment(sketch, "E1751", {"start": v(-3.5, -17.66) * mm, "end": v(-3.4, -17.25) * mm});
            skLineSegment(sketch, "E1752", {"start": v(-3.4, -17.25) * mm, "end": v(-3.3, -16.84) * mm});
            skLineSegment(sketch, "E1753", {"start": v(-3.3, -16.84) * mm, "end": v(-3.19, -16.42) * mm});
            skLineSegment(sketch, "E1754", {"start": v(-3.19, -16.42) * mm, "end": v(-3.06, -16.01) * mm});
            skLineSegment(sketch, "E1755", {"start": v(-3.06, -16.01) * mm, "end": v(-2.93, -15.6) * mm});
            skLineSegment(sketch, "E1756", {"start": v(-2.93, -15.6) * mm, "end": v(-2.78, -15.2) * mm});
            skLineSegment(sketch, "E1757", {"start": v(-2.78, -15.2) * mm, "end": v(-2.62, -14.8) * mm});
            skLineSegment(sketch, "E1758", {"start": v(-2.62, -14.8) * mm, "end": v(-2.44, -14.4) * mm});
            skLineSegment(sketch, "E1759", {"start": v(-2.44, -14.4) * mm, "end": v(-2.25, -14) * mm});
            skLineSegment(sketch, "E1760", {"start": v(-2.25, -14) * mm, "end": v(-2.05, -13.6) * mm});
            skLineSegment(sketch, "E1761", {"start": v(-2.05, -13.6) * mm, "end": v(-1.84, -13.22) * mm});
            skLineSegment(sketch, "E1762", {"start": v(-1.84, -13.22) * mm, "end": v(-1.61, -12.83) * mm});
            skLineSegment(sketch, "E1763", {"start": v(-1.61, -12.83) * mm, "end": v(-1.37, -12.46) * mm});
            skLineSegment(sketch, "E1764", {"start": v(-1.37, -12.46) * mm, "end": v(-1.1, -12.08) * mm});
            skLineSegment(sketch, "E1765", {"start": v(-1.1, -12.08) * mm, "end": v(-0.84, -11.71) * mm});
            skLineSegment(sketch, "E1766", {"start": v(-0.84, -11.71) * mm, "end": v(-0.55, -11.35) * mm});
            skLineSegment(sketch, "E1767", {"start": v(-0.55, -11.35) * mm, "end": v(-0.24, -11) * mm});
            skLineSegment(sketch, "E1768", {"start": v(-0.24, -11) * mm, "end": v(0.08, -10.65) * mm});
            skLineSegment(sketch, "E1769", {"start": v(0.08, -10.65) * mm, "end": v(0.26, -10.84) * mm});
            skLineSegment(sketch, "E1770", {"start": v(0.26, -10.84) * mm, "end": v(0.44, -11.04) * mm});
            skLineSegment(sketch, "E1771", {"start": v(0.44, -11.04) * mm, "end": v(0.6, -11.25) * mm});
            skLineSegment(sketch, "E1772", {"start": v(0.6, -11.25) * mm, "end": v(0.78, -11.47) * mm});
            skLineSegment(sketch, "E1773", {"start": v(0.78, -11.47) * mm, "end": v(1.1, -11.93) * mm});
            skLineSegment(sketch, "E1774", {"start": v(1.1, -11.93) * mm, "end": v(1.4, -12.42) * mm});
            skLineSegment(sketch, "E1775", {"start": v(1.4, -12.42) * mm, "end": v(1.7, -12.94) * mm});
            skLineSegment(sketch, "E1776", {"start": v(1.7, -12.94) * mm, "end": v(1.98, -13.48) * mm});
            skLineSegment(sketch, "E1777", {"start": v(1.98, -13.48) * mm, "end": v(2.24, -14.05) * mm});
            skLineSegment(sketch, "E1778", {"start": v(2.24, -14.05) * mm, "end": v(2.5, -14.63) * mm});
            skLineSegment(sketch, "E1779", {"start": v(2.5, -14.63) * mm, "end": v(2.72, -15.22) * mm});
            skLineSegment(sketch, "E1780", {"start": v(2.72, -15.22) * mm, "end": v(2.94, -15.83) * mm});
            skLineSegment(sketch, "E1781", {"start": v(2.94, -15.83) * mm, "end": v(3.14, -16.45) * mm});
            skLineSegment(sketch, "E1782", {"start": v(3.14, -16.45) * mm, "end": v(3.33, -17.07) * mm});
            skLineSegment(sketch, "E1783", {"start": v(3.33, -17.07) * mm, "end": v(3.5, -17.7) * mm});
            skLineSegment(sketch, "E1784", {"start": v(3.5, -17.7) * mm, "end": v(3.65, -18.33) * mm});
            skLineSegment(sketch, "E1785", {"start": v(3.65, -18.33) * mm, "end": v(3.8, -18.95) * mm});
            skLineSegment(sketch, "E1786", {"start": v(3.8, -18.95) * mm, "end": v(3.92, -19.57) * mm});
            skLineSegment(sketch, "E1787", {"start": v(3.92, -19.57) * mm, "end": v(4.03, -20.21) * mm});
            skLineSegment(sketch, "E1788", {"start": v(4.03, -20.21) * mm, "end": v(4.12, -20.82) * mm});
            skLineSegment(sketch, "E1789", {"start": v(4.12, -20.82) * mm, "end": v(4.2, -21.39) * mm});
            skLineSegment(sketch, "E1790", {"start": v(4.2, -21.39) * mm, "end": v(4.25, -21.92) * mm});
            skLineSegment(sketch, "E1791", {"start": v(4.25, -21.92) * mm, "end": v(4.28, -22.43) * mm});
            skLineSegment(sketch, "E1792", {"start": v(4.28, -22.43) * mm, "end": v(4.3, -22.9) * mm});
            skLineSegment(sketch, "E1793", {"start": v(4.3, -22.9) * mm, "end": v(4.3, -23.35) * mm});
            skLineSegment(sketch, "E1794", {"start": v(4.3, -23.35) * mm, "end": v(4.28, -23.77) * mm});
            skLineSegment(sketch, "E1795", {"start": v(4.28, -23.77) * mm, "end": v(4.25, -24.17) * mm});
            skLineSegment(sketch, "E1796", {"start": v(4.25, -24.17) * mm, "end": v(4.21, -24.55) * mm});
            skLineSegment(sketch, "E1797", {"start": v(4.21, -24.55) * mm, "end": v(4.16, -24.9) * mm});
            skLineSegment(sketch, "E1798", {"start": v(4.16, -24.9) * mm, "end": v(4.1, -25.24) * mm});
            skLineSegment(sketch, "E1799", {"start": v(4.1, -25.24) * mm, "end": v(4.03, -25.56) * mm});
            skLineSegment(sketch, "E1800", {"start": v(4.03, -25.56) * mm, "end": v(3.95, -25.87) * mm});
            skLineSegment(sketch, "E1801", {"start": v(3.95, -25.87) * mm, "end": v(3.78, -26.45) * mm});
            skLineSegment(sketch, "E1802", {"start": v(3.78, -26.45) * mm, "end": v(3.6, -27) * mm});
            skLineSegment(sketch, "E1803", {"start": v(3.6, -27) * mm, "end": v(3.4, -27.51) * mm});
            skLineSegment(sketch, "E1804", {"start": v(3.4, -27.51) * mm, "end": v(3.22, -28.03) * mm});
            skLineSegment(sketch, "E1805", {"start": v(3.22, -28.03) * mm, "end": v(3.05, -28.55) * mm});
            skLineSegment(sketch, "E1806", {"start": v(3.05, -28.55) * mm, "end": v(2.97, -28.82) * mm});
            skLineSegment(sketch, "E1807", {"start": v(2.97, -28.82) * mm, "end": v(2.9, -29.1) * mm});
            skLineSegment(sketch, "E1808", {"start": v(2.9, -29.1) * mm, "end": v(2.84, -29.38) * mm});
            skLineSegment(sketch, "E1809", {"start": v(2.84, -29.38) * mm, "end": v(2.8, -29.68) * mm});
            skLineSegment(sketch, "E1810", {"start": v(2.8, -29.68) * mm, "end": v(2.76, -29.99) * mm});
            skLineSegment(sketch, "E1811", {"start": v(2.76, -29.99) * mm, "end": v(2.73, -30.31) * mm});
            skLineSegment(sketch, "E1812", {"start": v(2.73, -30.31) * mm, "end": v(2.72, -30.66) * mm});
            skLineSegment(sketch, "E1813", {"start": v(2.72, -30.66) * mm, "end": v(2.72, -31.02) * mm});
            skLineSegment(sketch, "E1814", {"start": v(2.72, -31.02) * mm, "end": v(2.94, -31.07) * mm});
            skLineSegment(sketch, "E1815", {"start": v(2.94, -31.07) * mm, "end": v(3.16, -31.1) * mm});
            skLineSegment(sketch, "E1816", {"start": v(3.16, -31.1) * mm, "end": v(3.38, -31.13) * mm});
            skLineSegment(sketch, "E1817", {"start": v(3.38, -31.13) * mm, "end": v(3.61, -31.14) * mm});
            skLineSegment(sketch, "E1818", {"start": v(3.61, -31.14) * mm, "end": v(3.84, -31.15) * mm});
            skLineSegment(sketch, "E1819", {"start": v(3.84, -31.15) * mm, "end": v(4.08, -31.15) * mm});
            skLineSegment(sketch, "E1820", {"start": v(4.08, -31.15) * mm, "end": v(4.32, -31.13) * mm});
            skLineSegment(sketch, "E1821", {"start": v(4.32, -31.13) * mm, "end": v(4.56, -31.11) * mm});
            skLineSegment(sketch, "E1822", {"start": v(4.56, -31.11) * mm, "end": v(4.8, -31.08) * mm});
            skLineSegment(sketch, "E1823", {"start": v(4.8, -31.08) * mm, "end": v(5.05, -31.04) * mm});
            skLineSegment(sketch, "E1824", {"start": v(5.05, -31.04) * mm, "end": v(5.56, -30.94) * mm});
            skLineSegment(sketch, "E1825", {"start": v(5.56, -30.94) * mm, "end": v(6.07, -30.8) * mm});
            skLineSegment(sketch, "E1826", {"start": v(6.07, -30.8) * mm, "end": v(6.6, -30.65) * mm});
            skLineSegment(sketch, "E1827", {"start": v(6.6, -30.65) * mm, "end": v(7.12, -30.46) * mm});
            skLineSegment(sketch, "E1828", {"start": v(7.12, -30.46) * mm, "end": v(7.66, -30.25) * mm});
            skLineSegment(sketch, "E1829", {"start": v(7.66, -30.25) * mm, "end": v(8.2, -30.02) * mm});
            skLineSegment(sketch, "E1830", {"start": v(8.2, -30.02) * mm, "end": v(8.75, -29.77) * mm});
            skLineSegment(sketch, "E1831", {"start": v(8.75, -29.77) * mm, "end": v(9.3, -29.5) * mm});
            skLineSegment(sketch, "E1832", {"start": v(9.3, -29.5) * mm, "end": v(9.85, -29.21) * mm});
            skLineSegment(sketch, "E1833", {"start": v(9.85, -29.21) * mm, "end": v(10.4, -28.92) * mm});
            skLineSegment(sketch, "E1834", {"start": v(10.4, -28.92) * mm, "end": v(10.96, -28.61) * mm});
            skLineSegment(sketch, "E1835", {"start": v(10.96, -28.61) * mm, "end": v(12.06, -27.98) * mm});
            skLineSegment(sketch, "E1836", {"start": v(12.06, -27.98) * mm, "end": v(13.16, -27.33) * mm});
            skLineSegment(sketch, "E1837", {"start": v(13.16, -27.33) * mm, "end": v(14.23, -26.69) * mm});
            skLineSegment(sketch, "E1838", {"start": v(14.23, -26.69) * mm, "end": v(15.28, -26.07) * mm});
            skLineSegment(sketch, "E1839", {"start": v(15.28, -26.07) * mm, "end": v(16.3, -25.48) * mm});
            skLineSegment(sketch, "E1840", {"start": v(16.3, -25.48) * mm, "end": v(16.79, -25.21) * mm});
            skLineSegment(sketch, "E1841", {"start": v(16.79, -25.21) * mm, "end": v(17.27, -24.96) * mm});
            skLineSegment(sketch, "E1842", {"start": v(17.27, -24.96) * mm, "end": v(17.74, -24.72) * mm});
            skLineSegment(sketch, "E1843", {"start": v(17.74, -24.72) * mm, "end": v(18.19, -24.5) * mm});
            skLineSegment(sketch, "E1844", {"start": v(18.19, -24.5) * mm, "end": v(18.63, -24.31) * mm});
            skLineSegment(sketch, "E1845", {"start": v(18.63, -24.31) * mm, "end": v(19.05, -24.15) * mm});
            skLineSegment(sketch, "E1846", {"start": v(19.05, -24.15) * mm, "end": v(19.36, -24.3) * mm});
            skLineSegment(sketch, "E1847", {"start": v(19.36, -24.3) * mm, "end": v(19.67, -24.46) * mm});
            skLineSegment(sketch, "E1848", {"start": v(19.67, -24.46) * mm, "end": v(20.28, -24.8) * mm});
            skLineSegment(sketch, "E1849", {"start": v(20.28, -24.8) * mm, "end": v(20.88, -25.18) * mm});
            skLineSegment(sketch, "E1850", {"start": v(20.88, -25.18) * mm, "end": v(21.49, -25.56) * mm});
            skLineSegment(sketch, "E1851", {"start": v(21.49, -25.56) * mm, "end": v(22.1, -25.93) * mm});
            skLineSegment(sketch, "E1852", {"start": v(22.1, -25.93) * mm, "end": v(22.72, -26.3) * mm});
            skLineSegment(sketch, "E1853", {"start": v(22.72, -26.3) * mm, "end": v(23.04, -26.47) * mm});
            skLineSegment(sketch, "E1854", {"start": v(23.04, -26.47) * mm, "end": v(23.36, -26.63) * mm});
            skLineSegment(sketch, "E1855", {"start": v(23.36, -26.63) * mm, "end": v(23.7, -26.78) * mm});
            skLineSegment(sketch, "E1856", {"start": v(23.7, -26.78) * mm, "end": v(24.02, -26.92) * mm});
            skLineSegment(sketch, "E1857", {"start": v(24.02, -26.92) * mm, "end": v(24.37, -27.05) * mm});
            skLineSegment(sketch, "E1858", {"start": v(24.37, -27.05) * mm, "end": v(24.71, -27.17) * mm});
            skLineSegment(sketch, "E1859", {"start": v(24.71, -27.17) * mm, "end": v(25.07, -27.27) * mm});
            skLineSegment(sketch, "E1860", {"start": v(25.07, -27.27) * mm, "end": v(25.44, -27.35) * mm});
            skLineSegment(sketch, "E1861", {"start": v(25.44, -27.35) * mm, "end": v(25.81, -27.41) * mm});
            skLineSegment(sketch, "E1862", {"start": v(25.81, -27.41) * mm, "end": v(26.2, -27.45) * mm});
            skLineSegment(sketch, "E1863", {"start": v(26.2, -27.45) * mm, "end": v(26.6, -27.47) * mm});
            skLineSegment(sketch, "E1864", {"start": v(26.6, -27.47) * mm, "end": v(27, -27.47) * mm});
            skLineSegment(sketch, "E1865", {"start": v(27, -27.47) * mm, "end": v(27.42, -27.44) * mm});
            skLineSegment(sketch, "E1866", {"start": v(27.42, -27.44) * mm, "end": v(27.85, -27.4) * mm});
            skLineSegment(sketch, "E1867", {"start": v(27.85, -27.4) * mm, "end": v(28.3, -27.3) * mm});
            skLineSegment(sketch, "E1868", {"start": v(28.3, -27.3) * mm, "end": v(28.75, -27.2) * mm});
            skLineSegment(sketch, "E1869", {"start": v(28.75, -27.2) * mm, "end": v(29.23, -27.06) * mm});
            skLineSegment(sketch, "E1870", {"start": v(29.23, -27.06) * mm, "end": v(29.71, -26.88) * mm});
            skLineSegment(sketch, "E1871", {"start": v(29.71, -26.88) * mm, "end": v(30.22, -26.67) * mm});
            skLineSegment(sketch, "E1872", {"start": v(30.22, -26.67) * mm, "end": v(30.74, -26.43) * mm});
            skLineSegment(sketch, "E1873", {"start": v(30.74, -26.43) * mm, "end": v(31.15, -26.22) * mm});
            skLineSegment(sketch, "E1874", {"start": v(31.15, -26.22) * mm, "end": v(31.53, -26) * mm});
            skLineSegment(sketch, "E1875", {"start": v(31.53, -26) * mm, "end": v(31.9, -25.78) * mm});
            skLineSegment(sketch, "E1876", {"start": v(31.9, -25.78) * mm, "end": v(32.23, -25.56) * mm});
            skLineSegment(sketch, "E1877", {"start": v(32.23, -25.56) * mm, "end": v(32.55, -25.32) * mm});
            skLineSegment(sketch, "E1878", {"start": v(32.55, -25.32) * mm, "end": v(32.85, -25.07) * mm});
            skLineSegment(sketch, "E1879", {"start": v(32.85, -25.07) * mm, "end": v(33.14, -24.82) * mm});
            skLineSegment(sketch, "E1880", {"start": v(33.14, -24.82) * mm, "end": v(33.4, -24.56) * mm});
            skLineSegment(sketch, "E1881", {"start": v(33.4, -24.56) * mm, "end": v(33.65, -24.29) * mm});
            skLineSegment(sketch, "E1882", {"start": v(33.65, -24.29) * mm, "end": v(33.87, -24) * mm});
            skLineSegment(sketch, "E1883", {"start": v(33.87, -24) * mm, "end": v(34.08, -23.72) * mm});
            skLineSegment(sketch, "E1884", {"start": v(34.08, -23.72) * mm, "end": v(34.28, -23.42) * mm});
            skLineSegment(sketch, "E1885", {"start": v(34.28, -23.42) * mm, "end": v(34.46, -23.1) * mm});
            skLineSegment(sketch, "E1886", {"start": v(34.46, -23.1) * mm, "end": v(34.62, -22.79) * mm});
            skLineSegment(sketch, "E1887", {"start": v(34.62, -22.79) * mm, "end": v(34.77, -22.45) * mm});
            skLineSegment(sketch, "E1888", {"start": v(34.77, -22.45) * mm, "end": v(34.9, -22.11) * mm});
            skLineSegment(sketch, "E1889", {"start": v(34.9, -22.11) * mm, "end": v(35.03, -21.76) * mm});
            skLineSegment(sketch, "E1890", {"start": v(35.03, -21.76) * mm, "end": v(35.14, -21.39) * mm});
            skLineSegment(sketch, "E1891", {"start": v(35.14, -21.39) * mm, "end": v(35.24, -21) * mm});
            skLineSegment(sketch, "E1892", {"start": v(35.24, -21) * mm, "end": v(35.32, -20.61) * mm});
            skLineSegment(sketch, "E1893", {"start": v(35.32, -20.61) * mm, "end": v(35.4, -20.2) * mm});
            skLineSegment(sketch, "E1894", {"start": v(35.4, -20.2) * mm, "end": v(35.46, -19.79) * mm});
            skLineSegment(sketch, "E1895", {"start": v(35.46, -19.79) * mm, "end": v(35.52, -19.36) * mm});
            skLineSegment(sketch, "E1896", {"start": v(35.52, -19.36) * mm, "end": v(35.56, -18.9) * mm});
            skLineSegment(sketch, "E1897", {"start": v(35.56, -18.9) * mm, "end": v(35.6, -18.45) * mm});
            skLineSegment(sketch, "E1898", {"start": v(35.6, -18.45) * mm, "end": v(35.63, -17.97) * mm});
            skLineSegment(sketch, "E1899", {"start": v(35.63, -17.97) * mm, "end": v(35.66, -16.97) * mm});
            skLineSegment(sketch, "E1900", {"start": v(35.66, -16.97) * mm, "end": v(35.67, -15.9) * mm});
            skLineSegment(sketch, "E1901", {"start": v(35.67, -15.9) * mm, "end": v(35.66, -14.77) * mm});
            skLineSegment(sketch, "E1902", {"start": v(35.66, -14.77) * mm, "end": v(36.24, -14.53) * mm});
            skLineSegment(sketch, "E1903", {"start": v(36.24, -14.53) * mm, "end": v(36.8, -14.3) * mm});
            skLineSegment(sketch, "E1904", {"start": v(36.8, -14.3) * mm, "end": v(37.32, -14.06) * mm});
            skLineSegment(sketch, "E1905", {"start": v(37.32, -14.06) * mm, "end": v(37.83, -13.82) * mm});
            skLineSegment(sketch, "E1906", {"start": v(37.83, -13.82) * mm, "end": v(38.8, -13.35) * mm});
            skLineSegment(sketch, "E1907", {"start": v(38.8, -13.35) * mm, "end": v(39.71, -12.88) * mm});
            skLineSegment(sketch, "E1908", {"start": v(39.71, -12.88) * mm, "end": v(40.62, -12.38) * mm});
            skLineSegment(sketch, "E1909", {"start": v(40.62, -12.38) * mm, "end": v(41.53, -11.86) * mm});
            skLineSegment(sketch, "E1910", {"start": v(41.53, -11.86) * mm, "end": v(43.52, -10.73) * mm});
            skLineSegment(sketch, "E1911", {"start": v(43.52, -10.73) * mm, "end": v(44, -10.46) * mm});
            skLineSegment(sketch, "E1912", {"start": v(44, -10.46) * mm, "end": v(44.48, -10.2) * mm});
            skLineSegment(sketch, "E1913", {"start": v(44.48, -10.2) * mm, "end": v(45.4, -9.77) * mm});
            skLineSegment(sketch, "E1914", {"start": v(45.4, -9.77) * mm, "end": v(45.28, -10.84) * mm});
            skLineSegment(sketch, "E1915", {"start": v(45.28, -10.84) * mm, "end": v(45.13, -11.9) * mm});
            skLineSegment(sketch, "E1916", {"start": v(45.13, -11.9) * mm, "end": v(44.95, -12.97) * mm});
            skLineSegment(sketch, "E1917", {"start": v(44.95, -12.97) * mm, "end": v(44.76, -14.02) * mm});
            skLineSegment(sketch, "E1918", {"start": v(44.76, -14.02) * mm, "end": v(44.53, -15.06) * mm});
            skLineSegment(sketch, "E1919", {"start": v(44.53, -15.06) * mm, "end": v(44.29, -16.1) * mm});
            skLineSegment(sketch, "E1920", {"start": v(44.29, -16.1) * mm, "end": v(44.02, -17.12) * mm});
            skLineSegment(sketch, "E1921", {"start": v(44.02, -17.12) * mm, "end": v(43.73, -18.13) * mm});
            skLineSegment(sketch, "E1922", {"start": v(43.73, -18.13) * mm, "end": v(43.42, -19.14) * mm});
            skLineSegment(sketch, "E1923", {"start": v(43.42, -19.14) * mm, "end": v(43.08, -20.13) * mm});
            skLineSegment(sketch, "E1924", {"start": v(43.08, -20.13) * mm, "end": v(42.72, -21.11) * mm});
            skLineSegment(sketch, "E1925", {"start": v(42.72, -21.11) * mm, "end": v(42.34, -22.09) * mm});
            skLineSegment(sketch, "E1926", {"start": v(42.34, -22.09) * mm, "end": v(41.94, -23.05) * mm});
            skLineSegment(sketch, "E1927", {"start": v(41.94, -23.05) * mm, "end": v(41.52, -24) * mm});
            skLineSegment(sketch, "E1928", {"start": v(41.52, -24) * mm, "end": v(41.07, -24.94) * mm});
            skLineSegment(sketch, "E1929", {"start": v(41.07, -24.94) * mm, "end": v(40.61, -25.87) * mm});
            skLineSegment(sketch, "E1930", {"start": v(40.61, -25.87) * mm, "end": v(40.13, -26.79) * mm});
            skLineSegment(sketch, "E1931", {"start": v(40.13, -26.79) * mm, "end": v(39.62, -27.69) * mm});
            skLineSegment(sketch, "E1932", {"start": v(39.62, -27.69) * mm, "end": v(39.1, -28.58) * mm});
            skLineSegment(sketch, "E1933", {"start": v(39.1, -28.58) * mm, "end": v(38.56, -29.46) * mm});
            skLineSegment(sketch, "E1934", {"start": v(38.56, -29.46) * mm, "end": v(38, -30.32) * mm});
            skLineSegment(sketch, "E1935", {"start": v(38, -30.32) * mm, "end": v(37.41, -31.17) * mm});
            skLineSegment(sketch, "E1936", {"start": v(37.41, -31.17) * mm, "end": v(36.81, -32) * mm});
            skLineSegment(sketch, "E1937", {"start": v(36.81, -32) * mm, "end": v(36.2, -32.83) * mm});
            skLineSegment(sketch, "E1938", {"start": v(36.2, -32.83) * mm, "end": v(35.56, -33.64) * mm});
            skLineSegment(sketch, "E1939", {"start": v(35.56, -33.64) * mm, "end": v(34.9, -34.43) * mm});
            skLineSegment(sketch, "E1940", {"start": v(34.9, -34.43) * mm, "end": v(34.23, -35.21) * mm});
            skLineSegment(sketch, "E1941", {"start": v(34.23, -35.21) * mm, "end": v(33.55, -35.97) * mm});
            skLineSegment(sketch, "E1942", {"start": v(33.55, -35.97) * mm, "end": v(32.84, -36.72) * mm});
            skLineSegment(sketch, "E1943", {"start": v(32.84, -36.72) * mm, "end": v(32.12, -37.45) * mm});
            skLineSegment(sketch, "E1944", {"start": v(32.12, -37.45) * mm, "end": v(31.38, -38.17) * mm});
            skLineSegment(sketch, "E1945", {"start": v(31.38, -38.17) * mm, "end": v(30.63, -38.86) * mm});
            skLineSegment(sketch, "E1946", {"start": v(30.63, -38.86) * mm, "end": v(29.86, -39.55) * mm});
            skLineSegment(sketch, "E1947", {"start": v(29.86, -39.55) * mm, "end": v(29.08, -40.21) * mm});
            skLineSegment(sketch, "E1948", {"start": v(29.08, -40.21) * mm, "end": v(28.28, -40.86) * mm});
            skLineSegment(sketch, "E1949", {"start": v(28.28, -40.86) * mm, "end": v(27.47, -41.49) * mm});
            skLineSegment(sketch, "E1950", {"start": v(27.47, -41.49) * mm, "end": v(26.64, -42.1) * mm});
            skLineSegment(sketch, "E1951", {"start": v(26.64, -42.1) * mm, "end": v(25.8, -42.7) * mm});
            skLineSegment(sketch, "E1952", {"start": v(25.8, -42.7) * mm, "end": v(24.94, -43.27) * mm});
            skLineSegment(sketch, "E1953", {"start": v(24.94, -43.27) * mm, "end": v(24.07, -43.82) * mm});
            skLineSegment(sketch, "E1954", {"start": v(24.07, -43.82) * mm, "end": v(23.2, -44.36) * mm});
            skLineSegment(sketch, "E1955", {"start": v(23.2, -44.36) * mm, "end": v(22.3, -44.87) * mm});
            skLineSegment(sketch, "E1956", {"start": v(22.3, -44.87) * mm, "end": v(21.39, -45.37) * mm});
            skLineSegment(sketch, "E1957", {"start": v(21.39, -45.37) * mm, "end": v(20.47, -45.85) * mm});
            skLineSegment(sketch, "E1958", {"start": v(20.47, -45.85) * mm, "end": v(19.53, -46.3) * mm});
            skLineSegment(sketch, "E1959", {"start": v(19.53, -46.3) * mm, "end": v(18.6, -46.74) * mm});
            skLineSegment(sketch, "E1960", {"start": v(18.6, -46.74) * mm, "end": v(17.64, -47.15) * mm});
            skLineSegment(sketch, "E1961", {"start": v(17.64, -47.15) * mm, "end": v(16.67, -47.55) * mm});
            skLineSegment(sketch, "E1962", {"start": v(16.67, -47.55) * mm, "end": v(15.7, -47.92) * mm});
            skLineSegment(sketch, "E1963", {"start": v(15.7, -47.92) * mm, "end": v(14.7, -48.27) * mm});
            skLineSegment(sketch, "E1964", {"start": v(14.7, -48.27) * mm, "end": v(13.7, -48.6) * mm});
            skLineSegment(sketch, "E1965", {"start": v(13.7, -48.6) * mm, "end": v(12.7, -48.9) * mm});
            skLineSegment(sketch, "E1966", {"start": v(12.7, -48.9) * mm, "end": v(11.68, -49.18) * mm});
            skLineSegment(sketch, "E1967", {"start": v(11.68, -49.18) * mm, "end": v(10.65, -49.44) * mm});
            skLineSegment(sketch, "E1968", {"start": v(10.65, -49.44) * mm, "end": v(9.62, -49.68) * mm});
            skLineSegment(sketch, "E1969", {"start": v(9.62, -49.68) * mm, "end": v(8.57, -49.9) * mm});
            skLineSegment(sketch, "E1970", {"start": v(8.57, -49.9) * mm, "end": v(7.52, -50.08) * mm});
            skLineSegment(sketch, "E1971", {"start": v(7.52, -50.08) * mm, "end": v(6.45, -50.25) * mm});
            skLineSegment(sketch, "E1972", {"start": v(6.45, -50.25) * mm, "end": v(5.38, -50.39) * mm});
            skLineSegment(sketch, "E1973", {"start": v(5.38, -50.39) * mm, "end": v(4.3, -50.5) * mm});
            skLineSegment(sketch, "E1974", {"start": v(4.3, -50.5) * mm, "end": v(3.22, -50.6) * mm});
            skLineSegment(sketch, "E1975", {"start": v(3.22, -50.6) * mm, "end": v(2.13, -50.66) * mm});
            skLineSegment(sketch, "E1976", {"start": v(2.13, -50.66) * mm, "end": v(1.03, -50.7) * mm});
            skLineSegment(sketch, "E1977", {"start": v(1.03, -50.7) * mm, "end": v(-0.07, -50.7) * mm});
            skLineSegment(sketch, "E1978", {"start": v(-0.07, -50.7) * mm, "end": v(-1.18, -50.7) * mm});
            skLineSegment(sketch, "E1979", {"start": v(-1.18, -50.7) * mm, "end": v(-2.27, -50.66) * mm});
            skLineSegment(sketch, "E1980", {"start": v(-2.27, -50.66) * mm, "end": v(-3.36, -50.6) * mm});
            skLineSegment(sketch, "E1981", {"start": v(-3.36, -50.6) * mm, "end": v(-4.44, -50.5) * mm});
            skLineSegment(sketch, "E1982", {"start": v(-4.44, -50.5) * mm, "end": v(-5.52, -50.39) * mm});
            skLineSegment(sketch, "E1983", {"start": v(-5.52, -50.39) * mm, "end": v(-6.59, -50.25) * mm});
            skLineSegment(sketch, "E1984", {"start": v(-6.59, -50.25) * mm, "end": v(-7.65, -50.08) * mm});
            skLineSegment(sketch, "E1985", {"start": v(-7.65, -50.08) * mm, "end": v(-8.7, -49.9) * mm});
            skLineSegment(sketch, "E1986", {"start": v(-8.7, -49.9) * mm, "end": v(-9.74, -49.68) * mm});
            skLineSegment(sketch, "E1987", {"start": v(-9.74, -49.68) * mm, "end": v(-10.78, -49.45) * mm});
            skLineSegment(sketch, "E1988", {"start": v(-10.78, -49.45) * mm, "end": v(-11.8, -49.19) * mm});
            skLineSegment(sketch, "E1989", {"start": v(-11.8, -49.19) * mm, "end": v(-12.82, -48.9) * mm});
            skLineSegment(sketch, "E1990", {"start": v(-12.82, -48.9) * mm, "end": v(-13.83, -48.6) * mm});
            skLineSegment(sketch, "E1991", {"start": v(-13.83, -48.6) * mm, "end": v(-14.82, -48.28) * mm});
            skLineSegment(sketch, "E1992", {"start": v(-14.82, -48.28) * mm, "end": v(-15.8, -47.93) * mm});
            skLineSegment(sketch, "E1993", {"start": v(-15.8, -47.93) * mm, "end": v(-16.79, -47.56) * mm});
            skLineSegment(sketch, "E1994", {"start": v(-16.79, -47.56) * mm, "end": v(-17.75, -47.17) * mm});
            skLineSegment(sketch, "E1995", {"start": v(-17.75, -47.17) * mm, "end": v(-18.7, -46.75) * mm});
            skLineSegment(sketch, "E1996", {"start": v(-18.7, -46.75) * mm, "end": v(-19.65, -46.32) * mm});
            skLineSegment(sketch, "E1997", {"start": v(-19.65, -46.32) * mm, "end": v(-20.58, -45.86) * mm});
            skLineSegment(sketch, "E1998", {"start": v(-20.58, -45.86) * mm, "end": v(-21.5, -45.39) * mm});
            skLineSegment(sketch, "E1999", {"start": v(-21.5, -45.39) * mm, "end": v(-22.4, -44.9) * mm});
            skLineSegment(sketch, "E2000", {"start": v(-22.4, -44.9) * mm, "end": v(-23.3, -44.38) * mm});
            skLineSegment(sketch, "E2001", {"start": v(-23.3, -44.38) * mm, "end": v(-24.18, -43.84) * mm});
            skLineSegment(sketch, "E2002", {"start": v(-24.18, -43.84) * mm, "end": v(-25.05, -43.29) * mm});
            skLineSegment(sketch, "E2003", {"start": v(-25.05, -43.29) * mm, "end": v(-25.9, -42.72) * mm});
            skLineSegment(sketch, "E2004", {"start": v(-25.9, -42.72) * mm, "end": v(-26.74, -42.13) * mm});
            skLineSegment(sketch, "E2005", {"start": v(-26.74, -42.13) * mm, "end": v(-27.57, -41.52) * mm});
            skLineSegment(sketch, "E2006", {"start": v(-27.57, -41.52) * mm, "end": v(-28.38, -40.89) * mm});
            skLineSegment(sketch, "E2007", {"start": v(-28.38, -40.89) * mm, "end": v(-29.18, -40.24) * mm});
            skLineSegment(sketch, "E2008", {"start": v(-29.18, -40.24) * mm, "end": v(-29.97, -39.58) * mm});
            skLineSegment(sketch, "E2009", {"start": v(-29.97, -39.58) * mm, "end": v(-30.73, -38.9) * mm});
            skLineSegment(sketch, "E2010", {"start": v(-30.73, -38.9) * mm, "end": v(-31.49, -38.2) * mm});
            skLineSegment(sketch, "E2011", {"start": v(-31.49, -38.2) * mm, "end": v(-32.22, -37.5) * mm});
            skLineSegment(sketch, "E2012", {"start": v(-32.22, -37.5) * mm, "end": v(-32.94, -36.77) * mm});
            skLineSegment(sketch, "E2013", {"start": v(-32.94, -36.77) * mm, "end": v(-33.65, -36.02) * mm});
            skLineSegment(sketch, "E2014", {"start": v(-33.65, -36.02) * mm, "end": v(-34.33, -35.26) * mm});
            skLineSegment(sketch, "E2015", {"start": v(-34.33, -35.26) * mm, "end": v(-35, -34.48) * mm});
            skLineSegment(sketch, "E2016", {"start": v(-35, -34.48) * mm, "end": v(-35.66, -33.7) * mm});
            skLineSegment(sketch, "E2017", {"start": v(-35.66, -33.7) * mm, "end": v(-36.3, -32.89) * mm});
            skLineSegment(sketch, "E2018", {"start": v(-36.3, -32.89) * mm, "end": v(-36.91, -32.07) * mm});
            skLineSegment(sketch, "E2019", {"start": v(-36.91, -32.07) * mm, "end": v(-37.51, -31.23) * mm});
            skLineSegment(sketch, "E2020", {"start": v(-37.51, -31.23) * mm, "end": v(-38.1, -30.39) * mm});
            skLineSegment(sketch, "E2021", {"start": v(-38.1, -30.39) * mm, "end": v(-38.66, -29.52) * mm});
            skLineSegment(sketch, "E2022", {"start": v(-38.66, -29.52) * mm, "end": v(-39.2, -28.65) * mm});
            skLineSegment(sketch, "E2023", {"start": v(-39.2, -28.65) * mm, "end": v(-39.72, -27.76) * mm});
            skLineSegment(sketch, "E2024", {"start": v(-39.72, -27.76) * mm, "end": v(-40.23, -26.86) * mm});
            skLineSegment(sketch, "E2025", {"start": v(-40.23, -26.86) * mm, "end": v(-40.71, -25.95) * mm});
            skLineSegment(sketch, "E2026", {"start": v(-40.71, -25.95) * mm, "end": v(-41.18, -25.02) * mm});
            skLineSegment(sketch, "E2027", {"start": v(-41.18, -25.02) * mm, "end": v(-41.62, -24.08) * mm});
            skLineSegment(sketch, "E2028", {"start": v(-41.62, -24.08) * mm, "end": v(-42.05, -23.14) * mm});
            skLineSegment(sketch, "E2029", {"start": v(-42.05, -23.14) * mm, "end": v(-42.45, -22.18) * mm});
            skLineSegment(sketch, "E2030", {"start": v(-42.45, -22.18) * mm, "end": v(-42.83, -21.2) * mm});
            skLineSegment(sketch, "E2031", {"start": v(-42.83, -21.2) * mm, "end": v(-43.2, -20.22) * mm});
            skLineSegment(sketch, "E2032", {"start": v(-43.2, -20.22) * mm, "end": v(-43.53, -19.23) * mm});
            skLineSegment(sketch, "E2033", {"start": v(-43.53, -19.23) * mm, "end": v(-43.84, -18.23) * mm});
            skLineSegment(sketch, "E2034", {"start": v(-43.84, -18.23) * mm, "end": v(-44.14, -17.22) * mm});
            skLineSegment(sketch, "E2035", {"start": v(-44.14, -17.22) * mm, "end": v(-44.4, -16.2) * mm});
            skLineSegment(sketch, "E2036", {"start": v(-44.4, -16.2) * mm, "end": v(-44.65, -15.17) * mm});
            skLineSegment(sketch, "E2037", {"start": v(-44.65, -15.17) * mm, "end": v(-44.88, -14.13) * mm});
            skLineSegment(sketch, "E2038", {"start": v(-44.88, -14.13) * mm, "end": v(-45.08, -13.08) * mm});
            skLineSegment(sketch, "E2039", {"start": v(-45.08, -13.08) * mm, "end": v(-45.25, -12.02) * mm});
            skLineSegment(sketch, "E2040", {"start": v(-45.25, -12.02) * mm, "end": v(-45.4, -10.96) * mm});
            skLineSegment(sketch, "E2041", {"start": v(-45.4, -10.96) * mm, "end": v(-45.53, -9.89) * mm});
            skLineSegment(sketch, "E2042", {"start": v(45.6, -3.17) * mm, "end": v(44.91, -2.98) * mm});
            skLineSegment(sketch, "E2043", {"start": v(44.91, -2.98) * mm, "end": v(44.58, -2.87) * mm});
            skLineSegment(sketch, "E2044", {"start": v(44.58, -2.87) * mm, "end": v(44.26, -2.76) * mm});
            skLineSegment(sketch, "E2045", {"start": v(44.26, -2.76) * mm, "end": v(43.94, -2.63) * mm});
            skLineSegment(sketch, "E2046", {"start": v(43.94, -2.63) * mm, "end": v(43.6, -2.47) * mm});
            skLineSegment(sketch, "E2047", {"start": v(43.6, -2.47) * mm, "end": v(43.27, -2.29) * mm});
            skLineSegment(sketch, "E2048", {"start": v(43.27, -2.29) * mm, "end": v(42.93, -2.07) * mm});
            skLineSegment(sketch, "E2049", {"start": v(42.93, -2.07) * mm, "end": v(42.56, -1.82) * mm});
            skLineSegment(sketch, "E2050", {"start": v(42.56, -1.82) * mm, "end": v(42.17, -1.52) * mm});
            skLineSegment(sketch, "E2051", {"start": v(42.17, -1.52) * mm, "end": v(41.76, -1.17) * mm});
            skLineSegment(sketch, "E2052", {"start": v(41.76, -1.17) * mm, "end": v(41.31, -0.78) * mm});
            skLineSegment(sketch, "E2053", {"start": v(41.31, -0.78) * mm, "end": v(40.83, -0.32) * mm});
            skLineSegment(sketch, "E2054", {"start": v(40.83, -0.32) * mm, "end": v(40.31, 0.2) * mm});
            skLineSegment(sketch, "E2055", {"start": v(40.31, 0.2) * mm, "end": v(39.74, 0.79) * mm});
            skLineSegment(sketch, "E2056", {"start": v(39.74, 0.79) * mm, "end": v(39.13, 1.45) * mm});
            skLineSegment(sketch, "E2057", {"start": v(39.13, 1.45) * mm, "end": v(38.8, 1.8) * mm});
            skLineSegment(sketch, "E2058", {"start": v(38.8, 1.8) * mm, "end": v(38.5, 2.16) * mm});
            skLineSegment(sketch, "E2059", {"start": v(38.5, 2.16) * mm, "end": v(37.9, 2.87) * mm});
            skLineSegment(sketch, "E2060", {"start": v(37.9, 2.87) * mm, "end": v(37.36, 3.59) * mm});
            skLineSegment(sketch, "E2061", {"start": v(37.36, 3.59) * mm, "end": v(36.84, 4.3) * mm});
            skLineSegment(sketch, "E2062", {"start": v(36.84, 4.3) * mm, "end": v(36.35, 5.01) * mm});
            skLineSegment(sketch, "E2063", {"start": v(36.35, 5.01) * mm, "end": v(35.89, 5.73) * mm});
            skLineSegment(sketch, "E2064", {"start": v(35.89, 5.73) * mm, "end": v(35.45, 6.44) * mm});
            skLineSegment(sketch, "E2065", {"start": v(35.45, 6.44) * mm, "end": v(35.04, 7.14) * mm});
            skLineSegment(sketch, "E2066", {"start": v(35.04, 7.14) * mm, "end": v(34.64, 7.85) * mm});
            skLineSegment(sketch, "E2067", {"start": v(34.64, 7.85) * mm, "end": v(34.26, 8.55) * mm});
            skLineSegment(sketch, "E2068", {"start": v(34.26, 8.55) * mm, "end": v(33.53, 9.94) * mm});
            skLineSegment(sketch, "E2069", {"start": v(33.53, 9.94) * mm, "end": v(32.82, 11.3) * mm});
            skLineSegment(sketch, "E2070", {"start": v(32.82, 11.3) * mm, "end": v(32.46, 11.98) * mm});
            skLineSegment(sketch, "E2071", {"start": v(32.46, 11.98) * mm, "end": v(32.1, 12.65) * mm});
            skLineSegment(sketch, "E2072", {"start": v(32.1, 12.65) * mm, "end": v(31.73, 13.3) * mm});
            skLineSegment(sketch, "E2073", {"start": v(31.73, 13.3) * mm, "end": v(31.36, 13.96) * mm});
            skLineSegment(sketch, "E2074", {"start": v(31.36, 13.96) * mm, "end": v(30.96, 14.6) * mm});
            skLineSegment(sketch, "E2075", {"start": v(30.96, 14.6) * mm, "end": v(30.56, 15.23) * mm});
            skLineSegment(sketch, "E2076", {"start": v(30.56, 15.23) * mm, "end": v(30.13, 15.85) * mm});
            skLineSegment(sketch, "E2077", {"start": v(30.13, 15.85) * mm, "end": v(29.68, 16.46) * mm});
            skLineSegment(sketch, "E2078", {"start": v(29.68, 16.46) * mm, "end": v(29.2, 17.06) * mm});
            skLineSegment(sketch, "E2079", {"start": v(29.2, 17.06) * mm, "end": v(28.95, 17.36) * mm});
            skLineSegment(sketch, "E2080", {"start": v(28.95, 17.36) * mm, "end": v(28.69, 17.65) * mm});
            skLineSegment(sketch, "E2081", {"start": v(28.69, 17.65) * mm, "end": v(28.42, 17.94) * mm});
            skLineSegment(sketch, "E2082", {"start": v(28.42, 17.94) * mm, "end": v(28.15, 18.22) * mm});
            skLineSegment(sketch, "E2083", {"start": v(28.15, 18.22) * mm, "end": v(27.86, 18.5) * mm});
            skLineSegment(sketch, "E2084", {"start": v(27.86, 18.5) * mm, "end": v(27.57, 18.79) * mm});
            skLineSegment(sketch, "E2085", {"start": v(27.57, 18.79) * mm, "end": v(27.27, 19.06) * mm});
            skLineSegment(sketch, "E2086", {"start": v(27.27, 19.06) * mm, "end": v(26.95, 19.34) * mm});
            skLineSegment(sketch, "E2087", {"start": v(26.95, 19.34) * mm, "end": v(26.63, 19.6) * mm});
            skLineSegment(sketch, "E2088", {"start": v(26.63, 19.6) * mm, "end": v(26.3, 19.87) * mm});
            skLineSegment(sketch, "E2089", {"start": v(26.3, 19.87) * mm, "end": v(25.95, 20.13) * mm});
            skLineSegment(sketch, "E2090", {"start": v(25.95, 20.13) * mm, "end": v(25.59, 20.39) * mm});
            skLineSegment(sketch, "E2091", {"start": v(25.59, 20.39) * mm, "end": v(25.22, 20.64) * mm});
            skLineSegment(sketch, "E2092", {"start": v(25.22, 20.64) * mm, "end": v(24.84, 20.9) * mm});
            skLineSegment(sketch, "E2093", {"start": v(24.84, 20.9) * mm, "end": v(24.44, 21.14) * mm});
            skLineSegment(sketch, "E2094", {"start": v(24.44, 21.14) * mm, "end": v(24.03, 21.38) * mm});
            skLineSegment(sketch, "E2095", {"start": v(24.03, 21.38) * mm, "end": v(23.6, 21.62) * mm});
            skLineSegment(sketch, "E2096", {"start": v(23.6, 21.62) * mm, "end": v(23.17, 21.85) * mm});
            skLineSegment(sketch, "E2097", {"start": v(23.17, 21.85) * mm, "end": v(22.56, 22.15) * mm});
            skLineSegment(sketch, "E2098", {"start": v(22.56, 22.15) * mm, "end": v(21.98, 22.41) * mm});
            skLineSegment(sketch, "E2099", {"start": v(21.98, 22.41) * mm, "end": v(21.41, 22.64) * mm});
            skLineSegment(sketch, "E2100", {"start": v(21.41, 22.64) * mm, "end": v(20.87, 22.84) * mm});
            skLineSegment(sketch, "E2101", {"start": v(20.87, 22.84) * mm, "end": v(20.34, 23) * mm});
            skLineSegment(sketch, "E2102", {"start": v(20.34, 23) * mm, "end": v(19.83, 23.15) * mm});
            skLineSegment(sketch, "E2103", {"start": v(19.83, 23.15) * mm, "end": v(19.33, 23.27) * mm});
            skLineSegment(sketch, "E2104", {"start": v(19.33, 23.27) * mm, "end": v(18.85, 23.37) * mm});
            skLineSegment(sketch, "E2105", {"start": v(18.85, 23.37) * mm, "end": v(18.39, 23.45) * mm});
            skLineSegment(sketch, "E2106", {"start": v(18.39, 23.45) * mm, "end": v(17.93, 23.52) * mm});
            skLineSegment(sketch, "E2107", {"start": v(17.93, 23.52) * mm, "end": v(17.07, 23.62) * mm});
            skLineSegment(sketch, "E2108", {"start": v(17.07, 23.62) * mm, "end": v(16.24, 23.7) * mm});
            skLineSegment(sketch, "E2109", {"start": v(16.24, 23.7) * mm, "end": v(15.45, 23.79) * mm});
            skLineSegment(sketch, "E2110", {"start": v(15.45, 23.79) * mm, "end": v(15.07, 23.83) * mm});
            skLineSegment(sketch, "E2111", {"start": v(15.07, 23.83) * mm, "end": v(14.7, 23.89) * mm});
            skLineSegment(sketch, "E2112", {"start": v(14.7, 23.89) * mm, "end": v(14.33, 23.96) * mm});
            skLineSegment(sketch, "E2113", {"start": v(14.33, 23.96) * mm, "end": v(13.96, 24.04) * mm});
            skLineSegment(sketch, "E2114", {"start": v(13.96, 24.04) * mm, "end": v(13.6, 24.14) * mm});
            skLineSegment(sketch, "E2115", {"start": v(13.6, 24.14) * mm, "end": v(13.24, 24.26) * mm});
            skLineSegment(sketch, "E2116", {"start": v(13.24, 24.26) * mm, "end": v(12.89, 24.4) * mm});
            skLineSegment(sketch, "E2117", {"start": v(12.89, 24.4) * mm, "end": v(12.53, 24.57) * mm});
            skLineSegment(sketch, "E2118", {"start": v(12.53, 24.57) * mm, "end": v(12.18, 24.77) * mm});
            skLineSegment(sketch, "E2119", {"start": v(12.18, 24.77) * mm, "end": v(11.82, 25) * mm});
            skLineSegment(sketch, "E2120", {"start": v(11.82, 25) * mm, "end": v(11.47, 25.26) * mm});
            skLineSegment(sketch, "E2121", {"start": v(11.47, 25.26) * mm, "end": v(11.1, 25.56) * mm});
            skLineSegment(sketch, "E2122", {"start": v(11.1, 25.56) * mm, "end": v(10.75, 25.9) * mm});
            skLineSegment(sketch, "E2123", {"start": v(10.75, 25.9) * mm, "end": v(10.38, 26.28) * mm});
            skLineSegment(sketch, "E2124", {"start": v(10.38, 26.28) * mm, "end": v(10.01, 26.71) * mm});
            skLineSegment(sketch, "E2125", {"start": v(10.01, 26.71) * mm, "end": v(9.64, 27.2) * mm});
            skLineSegment(sketch, "E2126", {"start": v(9.64, 27.2) * mm, "end": v(10.3, 27.88) * mm});
            skLineSegment(sketch, "E2127", {"start": v(10.3, 27.88) * mm, "end": v(10.95, 28.57) * mm});
            skLineSegment(sketch, "E2128", {"start": v(10.95, 28.57) * mm, "end": v(11.57, 29.24) * mm});
            skLineSegment(sketch, "E2129", {"start": v(11.57, 29.24) * mm, "end": v(12.16, 29.91) * mm});
            skLineSegment(sketch, "E2130", {"start": v(12.16, 29.91) * mm, "end": v(12.73, 30.57) * mm});
            skLineSegment(sketch, "E2131", {"start": v(12.73, 30.57) * mm, "end": v(13.27, 31.23) * mm});
            skLineSegment(sketch, "E2132", {"start": v(13.27, 31.23) * mm, "end": v(13.79, 31.87) * mm});
            skLineSegment(sketch, "E2133", {"start": v(13.79, 31.87) * mm, "end": v(14.28, 32.5) * mm});
            skLineSegment(sketch, "E2134", {"start": v(14.28, 32.5) * mm, "end": v(14.75, 33.14) * mm});
            skLineSegment(sketch, "E2135", {"start": v(14.75, 33.14) * mm, "end": v(15.19, 33.76) * mm});
            skLineSegment(sketch, "E2136", {"start": v(15.19, 33.76) * mm, "end": v(15.6, 34.37) * mm});
            skLineSegment(sketch, "E2137", {"start": v(15.6, 34.37) * mm, "end": v(16, 34.97) * mm});
            skLineSegment(sketch, "E2138", {"start": v(16, 34.97) * mm, "end": v(16.37, 35.57) * mm});
            skLineSegment(sketch, "E2139", {"start": v(16.37, 35.57) * mm, "end": v(16.72, 36.15) * mm});
            skLineSegment(sketch, "E2140", {"start": v(16.72, 36.15) * mm, "end": v(17.05, 36.72) * mm});
            skLineSegment(sketch, "E2141", {"start": v(17.05, 36.72) * mm, "end": v(17.35, 37.29) * mm});
            skLineSegment(sketch, "E2142", {"start": v(17.35, 37.29) * mm, "end": v(18.1, 36.97) * mm});
            skLineSegment(sketch, "E2143", {"start": v(18.1, 36.97) * mm, "end": v(18.85, 36.64) * mm});
            skLineSegment(sketch, "E2144", {"start": v(18.85, 36.64) * mm, "end": v(19.58, 36.3) * mm});
            skLineSegment(sketch, "E2145", {"start": v(19.58, 36.3) * mm, "end": v(20.31, 35.94) * mm});
            skLineSegment(sketch, "E2146", {"start": v(20.31, 35.94) * mm, "end": v(21.03, 35.58) * mm});
            skLineSegment(sketch, "E2147", {"start": v(21.03, 35.58) * mm, "end": v(21.75, 35.2) * mm});
            skLineSegment(sketch, "E2148", {"start": v(21.75, 35.2) * mm, "end": v(22.45, 34.8) * mm});
            skLineSegment(sketch, "E2149", {"start": v(22.45, 34.8) * mm, "end": v(23.15, 34.4) * mm});
            skLineSegment(sketch, "E2150", {"start": v(23.15, 34.4) * mm, "end": v(23.84, 33.98) * mm});
            skLineSegment(sketch, "E2151", {"start": v(23.84, 33.98) * mm, "end": v(24.53, 33.55) * mm});
            skLineSegment(sketch, "E2152", {"start": v(24.53, 33.55) * mm, "end": v(25.2, 33.11) * mm});
            skLineSegment(sketch, "E2153", {"start": v(25.2, 33.11) * mm, "end": v(25.87, 32.66) * mm});
            skLineSegment(sketch, "E2154", {"start": v(25.87, 32.66) * mm, "end": v(26.53, 32.2) * mm});
            skLineSegment(sketch, "E2155", {"start": v(26.53, 32.2) * mm, "end": v(27.18, 31.72) * mm});
            skLineSegment(sketch, "E2156", {"start": v(27.18, 31.72) * mm, "end": v(27.82, 31.24) * mm});
            skLineSegment(sketch, "E2157", {"start": v(27.82, 31.24) * mm, "end": v(28.45, 30.74) * mm});
            skLineSegment(sketch, "E2158", {"start": v(28.45, 30.74) * mm, "end": v(29.07, 30.24) * mm});
            skLineSegment(sketch, "E2159", {"start": v(29.07, 30.24) * mm, "end": v(29.68, 29.72) * mm});
            skLineSegment(sketch, "E2160", {"start": v(29.68, 29.72) * mm, "end": v(30.29, 29.2) * mm});
            skLineSegment(sketch, "E2161", {"start": v(30.29, 29.2) * mm, "end": v(30.88, 28.65) * mm});
            skLineSegment(sketch, "E2162", {"start": v(30.88, 28.65) * mm, "end": v(31.47, 28.1) * mm});
            skLineSegment(sketch, "E2163", {"start": v(31.47, 28.1) * mm, "end": v(32.05, 27.54) * mm});
            skLineSegment(sketch, "E2164", {"start": v(32.05, 27.54) * mm, "end": v(32.61, 26.98) * mm});
            skLineSegment(sketch, "E2165", {"start": v(32.61, 26.98) * mm, "end": v(33.17, 26.4) * mm});
            skLineSegment(sketch, "E2166", {"start": v(33.17, 26.4) * mm, "end": v(33.71, 25.8) * mm});
            skLineSegment(sketch, "E2167", {"start": v(33.71, 25.8) * mm, "end": v(34.25, 25.21) * mm});
            skLineSegment(sketch, "E2168", {"start": v(34.25, 25.21) * mm, "end": v(34.77, 24.6) * mm});
            skLineSegment(sketch, "E2169", {"start": v(34.77, 24.6) * mm, "end": v(35.29, 23.99) * mm});
            skLineSegment(sketch, "E2170", {"start": v(35.29, 23.99) * mm, "end": v(35.8, 23.36) * mm});
            skLineSegment(sketch, "E2171", {"start": v(35.8, 23.36) * mm, "end": v(36.29, 22.73) * mm});
            skLineSegment(sketch, "E2172", {"start": v(36.29, 22.73) * mm, "end": v(36.77, 22.09) * mm});
            skLineSegment(sketch, "E2173", {"start": v(36.77, 22.09) * mm, "end": v(37.24, 21.43) * mm});
            skLineSegment(sketch, "E2174", {"start": v(37.24, 21.43) * mm, "end": v(37.7, 20.77) * mm});
            skLineSegment(sketch, "E2175", {"start": v(37.7, 20.77) * mm, "end": v(38.15, 20.1) * mm});
            skLineSegment(sketch, "E2176", {"start": v(38.15, 20.1) * mm, "end": v(38.58, 19.43) * mm});
            skLineSegment(sketch, "E2177", {"start": v(38.58, 19.43) * mm, "end": v(39, 18.74) * mm});
            skLineSegment(sketch, "E2178", {"start": v(39, 18.74) * mm, "end": v(39.42, 18.05) * mm});
            skLineSegment(sketch, "E2179", {"start": v(39.42, 18.05) * mm, "end": v(39.82, 17.35) * mm});
            skLineSegment(sketch, "E2180", {"start": v(39.82, 17.35) * mm, "end": v(40.21, 16.64) * mm});
            skLineSegment(sketch, "E2181", {"start": v(40.21, 16.64) * mm, "end": v(40.6, 15.92) * mm});
            skLineSegment(sketch, "E2182", {"start": v(40.6, 15.92) * mm, "end": v(40.96, 15.2) * mm});
            skLineSegment(sketch, "E2183", {"start": v(40.96, 15.2) * mm, "end": v(41.3, 14.47) * mm});
            skLineSegment(sketch, "E2184", {"start": v(41.3, 14.47) * mm, "end": v(41.65, 13.73) * mm});
            skLineSegment(sketch, "E2185", {"start": v(41.65, 13.73) * mm, "end": v(41.97, 12.99) * mm});
            skLineSegment(sketch, "E2186", {"start": v(41.97, 12.99) * mm, "end": v(42.29, 12.24) * mm});
            skLineSegment(sketch, "E2187", {"start": v(42.29, 12.24) * mm, "end": v(42.59, 11.48) * mm});
            skLineSegment(sketch, "E2188", {"start": v(42.59, 11.48) * mm, "end": v(42.88, 10.71) * mm});
            skLineSegment(sketch, "E2189", {"start": v(42.88, 10.71) * mm, "end": v(43.15, 9.94) * mm});
            skLineSegment(sketch, "E2190", {"start": v(43.15, 9.94) * mm, "end": v(43.41, 9.16) * mm});
            skLineSegment(sketch, "E2191", {"start": v(43.41, 9.16) * mm, "end": v(43.66, 8.38) * mm});
            skLineSegment(sketch, "E2192", {"start": v(43.66, 8.38) * mm, "end": v(43.9, 7.59) * mm});
            skLineSegment(sketch, "E2193", {"start": v(43.9, 7.59) * mm, "end": v(44.11, 6.8) * mm});
            skLineSegment(sketch, "E2194", {"start": v(44.11, 6.8) * mm, "end": v(44.32, 6) * mm});
            skLineSegment(sketch, "E2195", {"start": v(44.32, 6) * mm, "end": v(44.5, 5.18) * mm});
            skLineSegment(sketch, "E2196", {"start": v(44.5, 5.18) * mm, "end": v(44.69, 4.37) * mm});
            skLineSegment(sketch, "E2197", {"start": v(44.69, 4.37) * mm, "end": v(44.85, 3.55) * mm});
            skLineSegment(sketch, "E2198", {"start": v(44.85, 3.55) * mm, "end": v(45, 2.73) * mm});
            skLineSegment(sketch, "E2199", {"start": v(45, 2.73) * mm, "end": v(45.13, 1.9) * mm});
            skLineSegment(sketch, "E2200", {"start": v(45.13, 1.9) * mm, "end": v(45.25, 1.07) * mm});
            skLineSegment(sketch, "E2201", {"start": v(45.25, 1.07) * mm, "end": v(45.35, 0.23) * mm});
            skLineSegment(sketch, "E2202", {"start": v(45.35, 0.23) * mm, "end": v(45.44, -0.61) * mm});
            skLineSegment(sketch, "E2203", {"start": v(45.44, -0.61) * mm, "end": v(45.5, -1.46) * mm});
            skLineSegment(sketch, "E2204", {"start": v(45.5, -1.46) * mm, "end": v(45.57, -2.31) * mm});
            skLineSegment(sketch, "E2205", {"start": v(45.57, -2.31) * mm, "end": v(45.6, -3.17) * mm});
            skLineSegment(sketch, "E2206", {"start": v(1.7, 40.7) * mm, "end": v(1.7, 40.63) * mm});
            skLineSegment(sketch, "E2207", {"start": v(1.7, 40.63) * mm, "end": v(1.67, 40.5) * mm});
            skLineSegment(sketch, "E2208", {"start": v(1.67, 40.5) * mm, "end": v(1.52, 40.13) * mm});
            skLineSegment(sketch, "E2209", {"start": v(1.52, 40.13) * mm, "end": v(1.3, 39.6) * mm});
            skLineSegment(sketch, "E2210", {"start": v(1.3, 39.6) * mm, "end": v(1.04, 39.02) * mm});
            skLineSegment(sketch, "E2211", {"start": v(1.04, 39.02) * mm, "end": v(0.76, 38.42) * mm});
            skLineSegment(sketch, "E2212", {"start": v(0.76, 38.42) * mm, "end": v(0.49, 37.88) * mm});
            skLineSegment(sketch, "E2213", {"start": v(0.49, 37.88) * mm, "end": v(0.25, 37.45) * mm});
            skLineSegment(sketch, "E2214", {"start": v(0.25, 37.45) * mm, "end": v(0.16, 37.3) * mm});
            skLineSegment(sketch, "E2215", {"start": v(0.16, 37.3) * mm, "end": v(0.08, 37.21) * mm});
            skLineSegment(sketch, "E2216", {"start": v(0.08, 37.21) * mm, "end": v(0.02, 37.3) * mm});
            skLineSegment(sketch, "E2217", {"start": v(0.02, 37.3) * mm, "end": v(-0.04, 37.42) * mm});
            skLineSegment(sketch, "E2218", {"start": v(-0.04, 37.42) * mm, "end": v(-0.18, 37.78) * mm});
            skLineSegment(sketch, "E2219", {"start": v(-0.18, 37.78) * mm, "end": v(-0.33, 38.25) * mm});
            skLineSegment(sketch, "E2220", {"start": v(-0.33, 38.25) * mm, "end": v(-0.5, 38.78) * mm});
            skLineSegment(sketch, "E2221", {"start": v(-0.5, 38.78) * mm, "end": v(-0.7, 39.33) * mm});
            skLineSegment(sketch, "E2222", {"start": v(-0.7, 39.33) * mm, "end": v(-0.8, 39.6) * mm});
            skLineSegment(sketch, "E2223", {"start": v(-0.8, 39.6) * mm, "end": v(-0.92, 39.86) * mm});
            skLineSegment(sketch, "E2224", {"start": v(-0.92, 39.86) * mm, "end": v(-1.03, 40.1) * mm});
            skLineSegment(sketch, "E2225", {"start": v(-1.03, 40.1) * mm, "end": v(-1.14, 40.34) * mm});
            skLineSegment(sketch, "E2226", {"start": v(-1.14, 40.34) * mm, "end": v(-1.26, 40.54) * mm});
            skLineSegment(sketch, "E2227", {"start": v(-1.26, 40.54) * mm, "end": v(-1.39, 40.71) * mm});
            skLineSegment(sketch, "E2228", {"start": v(-1.39, 40.71) * mm, "end": v(-0.73, 40.73) * mm});
            skLineSegment(sketch, "E2229", {"start": v(-0.73, 40.73) * mm, "end": v(-0.07, 40.73) * mm});
            skLineSegment(sketch, "E2230", {"start": v(-0.07, 40.73) * mm, "end": v(0.82, 40.72) * mm});
            skLineSegment(sketch, "E2231", {"start": v(0.82, 40.72) * mm, "end": v(1.7, 40.7) * mm});
            skLineSegment(sketch, "E2232", {"start": v(-15.69, 43.37) * mm, "end": v(-15, 43.58) * mm});
            skLineSegment(sketch, "E2233", {"start": v(-15, 43.58) * mm, "end": v(-14.33, 43.78) * mm});
            skLineSegment(sketch, "E2234", {"start": v(-14.33, 43.78) * mm, "end": v(-13.64, 43.98) * mm});
            skLineSegment(sketch, "E2235", {"start": v(-13.64, 43.98) * mm, "end": v(-12.95, 44.16) * mm});
            skLineSegment(sketch, "E2236", {"start": v(-12.95, 44.16) * mm, "end": v(-12.26, 44.34) * mm});
            skLineSegment(sketch, "E2237", {"start": v(-12.26, 44.34) * mm, "end": v(-11.56, 44.5) * mm});
            skLineSegment(sketch, "E2238", {"start": v(-11.56, 44.5) * mm, "end": v(-10.86, 44.66) * mm});
            skLineSegment(sketch, "E2239", {"start": v(-10.86, 44.66) * mm, "end": v(-10.16, 44.8) * mm});
            skLineSegment(sketch, "E2240", {"start": v(-10.16, 44.8) * mm, "end": v(-10.52, 45.04) * mm});
            skLineSegment(sketch, "E2241", {"start": v(-10.52, 45.04) * mm, "end": v(-10.89, 45.26) * mm});
            skLineSegment(sketch, "E2242", {"start": v(-10.89, 45.26) * mm, "end": v(-11.25, 45.45) * mm});
            skLineSegment(sketch, "E2243", {"start": v(-11.25, 45.45) * mm, "end": v(-11.6, 45.62) * mm});
            skLineSegment(sketch, "E2244", {"start": v(-11.6, 45.62) * mm, "end": v(-11.94, 45.76) * mm});
            skLineSegment(sketch, "E2245", {"start": v(-11.94, 45.76) * mm, "end": v(-12.28, 45.87) * mm});
            skLineSegment(sketch, "E2246", {"start": v(-12.28, 45.87) * mm, "end": v(-12.6, 45.96) * mm});
            skLineSegment(sketch, "E2247", {"start": v(-12.6, 45.96) * mm, "end": v(-12.92, 46.03) * mm});
            skLineSegment(sketch, "E2248", {"start": v(-12.92, 46.03) * mm, "end": v(-13.23, 46.06) * mm});
            skLineSegment(sketch, "E2249", {"start": v(-13.23, 46.06) * mm, "end": v(-13.53, 46.07) * mm});
            skLineSegment(sketch, "E2250", {"start": v(-13.53, 46.07) * mm, "end": v(-13.67, 46.06) * mm});
            skLineSegment(sketch, "E2251", {"start": v(-13.67, 46.06) * mm, "end": v(-13.8, 46.05) * mm});
            skLineSegment(sketch, "E2252", {"start": v(-13.8, 46.05) * mm, "end": v(-13.94, 46.02) * mm});
            skLineSegment(sketch, "E2253", {"start": v(-13.94, 46.02) * mm, "end": v(-14.08, 46) * mm});
            skLineSegment(sketch, "E2254", {"start": v(-14.08, 46) * mm, "end": v(-14.2, 45.96) * mm});
            skLineSegment(sketch, "E2255", {"start": v(-14.2, 45.96) * mm, "end": v(-14.33, 45.9) * mm});
            skLineSegment(sketch, "E2256", {"start": v(-14.33, 45.9) * mm, "end": v(-14.45, 45.86) * mm});
            skLineSegment(sketch, "E2257", {"start": v(-14.45, 45.86) * mm, "end": v(-14.57, 45.8) * mm});
            skLineSegment(sketch, "E2258", {"start": v(-14.57, 45.8) * mm, "end": v(-14.68, 45.72) * mm});
            skLineSegment(sketch, "E2259", {"start": v(-14.68, 45.72) * mm, "end": v(-14.8, 45.65) * mm});
            skLineSegment(sketch, "E2260", {"start": v(-14.8, 45.65) * mm, "end": v(-14.9, 45.56) * mm});
            skLineSegment(sketch, "E2261", {"start": v(-14.9, 45.56) * mm, "end": v(-15, 45.47) * mm});
            skLineSegment(sketch, "E2262", {"start": v(-15, 45.47) * mm, "end": v(-15.08, 45.37) * mm});
            skLineSegment(sketch, "E2263", {"start": v(-15.08, 45.37) * mm, "end": v(-15.17, 45.27) * mm});
            skLineSegment(sketch, "E2264", {"start": v(-15.17, 45.27) * mm, "end": v(-15.24, 45.16) * mm});
            skLineSegment(sketch, "E2265", {"start": v(-15.24, 45.16) * mm, "end": v(-15.31, 45.05) * mm});
            skLineSegment(sketch, "E2266", {"start": v(-15.31, 45.05) * mm, "end": v(-15.38, 44.93) * mm});
            skLineSegment(sketch, "E2267", {"start": v(-15.38, 44.93) * mm, "end": v(-15.43, 44.81) * mm});
            skLineSegment(sketch, "E2268", {"start": v(-15.43, 44.81) * mm, "end": v(-15.53, 44.56) * mm});
            skLineSegment(sketch, "E2269", {"start": v(-15.53, 44.56) * mm, "end": v(-15.6, 44.28) * mm});
            skLineSegment(sketch, "E2270", {"start": v(-15.6, 44.28) * mm, "end": v(-15.65, 44) * mm});
            skLineSegment(sketch, "E2271", {"start": v(-15.65, 44) * mm, "end": v(-15.68, 43.69) * mm});
            skLineSegment(sketch, "E2272", {"start": v(-15.68, 43.69) * mm, "end": v(-15.69, 43.37) * mm});
            skLineSegment(sketch, "E2273", {"start": v(10.33, 44.74) * mm, "end": v(11.01, 44.6) * mm});
            skLineSegment(sketch, "E2274", {"start": v(11.01, 44.6) * mm, "end": v(11.7, 44.44) * mm});
            skLineSegment(sketch, "E2275", {"start": v(11.7, 44.44) * mm, "end": v(12.37, 44.28) * mm});
            skLineSegment(sketch, "E2276", {"start": v(12.37, 44.28) * mm, "end": v(13.04, 44.1) * mm});
            skLineSegment(sketch, "E2277", {"start": v(13.04, 44.1) * mm, "end": v(13.7, 43.92) * mm});
            skLineSegment(sketch, "E2278", {"start": v(13.7, 43.92) * mm, "end": v(14.37, 43.73) * mm});
            skLineSegment(sketch, "E2279", {"start": v(14.37, 43.73) * mm, "end": v(15.03, 43.53) * mm});
            skLineSegment(sketch, "E2280", {"start": v(15.03, 43.53) * mm, "end": v(15.69, 43.32) * mm});
            skLineSegment(sketch, "E2281", {"start": v(15.69, 43.32) * mm, "end": v(15.68, 43.6) * mm});
            skLineSegment(sketch, "E2282", {"start": v(15.68, 43.6) * mm, "end": v(15.66, 43.89) * mm});
            skLineSegment(sketch, "E2283", {"start": v(15.66, 43.89) * mm, "end": v(15.63, 44.17) * mm});
            skLineSegment(sketch, "E2284", {"start": v(15.63, 44.17) * mm, "end": v(15.6, 44.45) * mm});
            skLineSegment(sketch, "E2285", {"start": v(15.6, 44.45) * mm, "end": v(15.54, 44.72) * mm});
            skLineSegment(sketch, "E2286", {"start": v(15.54, 44.72) * mm, "end": v(15.48, 44.99) * mm});
            skLineSegment(sketch, "E2287", {"start": v(15.48, 44.99) * mm, "end": v(15.41, 45.25) * mm});
            skLineSegment(sketch, "E2288", {"start": v(15.41, 45.25) * mm, "end": v(15.33, 45.51) * mm});
            skLineSegment(sketch, "E2289", {"start": v(15.33, 45.51) * mm, "end": v(15.02, 45.65) * mm});
            skLineSegment(sketch, "E2290", {"start": v(15.02, 45.65) * mm, "end": v(14.79, 45.77) * mm});
            skLineSegment(sketch, "E2291", {"start": v(14.79, 45.77) * mm, "end": v(14.61, 45.87) * mm});
            skLineSegment(sketch, "E2292", {"start": v(14.61, 45.87) * mm, "end": v(14.48, 45.97) * mm});
            skLineSegment(sketch, "E2293", {"start": v(14.48, 45.97) * mm, "end": v(14.32, 46.1) * mm});
            skLineSegment(sketch, "E2294", {"start": v(14.32, 46.1) * mm, "end": v(14.26, 46.15) * mm});
            skLineSegment(sketch, "E2295", {"start": v(14.26, 46.15) * mm, "end": v(14.2, 46.18) * mm});
            skLineSegment(sketch, "E2296", {"start": v(14.2, 46.18) * mm, "end": v(14.14, 46.2) * mm});
            skLineSegment(sketch, "E2297", {"start": v(14.14, 46.2) * mm, "end": v(14.04, 46.19) * mm});
            skLineSegment(sketch, "E2298", {"start": v(14.04, 46.19) * mm, "end": v(13.74, 46.12) * mm});
            skLineSegment(sketch, "E2299", {"start": v(13.74, 46.12) * mm, "end": v(13.2, 45.97) * mm});
            skLineSegment(sketch, "E2300", {"start": v(13.2, 45.97) * mm, "end": v(12.34, 45.75) * mm});
            skLineSegment(sketch, "E2301", {"start": v(12.34, 45.75) * mm, "end": v(12.14, 45.69) * mm});
            skLineSegment(sketch, "E2302", {"start": v(12.14, 45.69) * mm, "end": v(11.92, 45.6) * mm});
            skLineSegment(sketch, "E2303", {"start": v(11.92, 45.6) * mm, "end": v(11.68, 45.5) * mm});
            skLineSegment(sketch, "E2304", {"start": v(11.68, 45.5) * mm, "end": v(11.43, 45.4) * mm});
            skLineSegment(sketch, "E2305", {"start": v(11.43, 45.4) * mm, "end": v(11.17, 45.26) * mm});
            skLineSegment(sketch, "E2306", {"start": v(11.17, 45.26) * mm, "end": v(10.9, 45.1) * mm});
            skLineSegment(sketch, "E2307", {"start": v(10.9, 45.1) * mm, "end": v(10.62, 44.93) * mm});
            skLineSegment(sketch, "E2308", {"start": v(10.62, 44.93) * mm, "end": v(10.33, 44.74) * mm});
            skLineSegment(sketch, "E2309", {"start": v(46.42, -25.48) * mm, "end": v(46.06, -26.27) * mm});
            skLineSegment(sketch, "E2310", {"start": v(46.06, -26.27) * mm, "end": v(45.7, -27.05) * mm});
            skLineSegment(sketch, "E2311", {"start": v(45.7, -27.05) * mm, "end": v(45.31, -27.82) * mm});
            skLineSegment(sketch, "E2312", {"start": v(45.31, -27.82) * mm, "end": v(44.92, -28.59) * mm});
            skLineSegment(sketch, "E2313", {"start": v(44.92, -28.59) * mm, "end": v(51.83, -29.77) * mm});
            skLineSegment(sketch, "E2314", {"start": v(51.83, -29.77) * mm, "end": v(46.42, -25.48) * mm});
            skLineSegment(sketch, "E2315", {"start": v(1.3, -55.77) * mm, "end": v(0.61, -55.78) * mm});
            skLineSegment(sketch, "E2316", {"start": v(0.61, -55.78) * mm, "end": v(-0.07, -55.79) * mm});
            skLineSegment(sketch, "E2317", {"start": v(-0.07, -55.79) * mm, "end": v(-0.76, -55.78) * mm});
            skLineSegment(sketch, "E2318", {"start": v(-0.76, -55.78) * mm, "end": v(-1.44, -55.77) * mm});
            skLineSegment(sketch, "E2319", {"start": v(-1.44, -55.77) * mm, "end": v(-2.12, -55.75) * mm});
            skLineSegment(sketch, "E2320", {"start": v(-2.12, -55.75) * mm, "end": v(-2.8, -55.72) * mm});
            skLineSegment(sketch, "E2321", {"start": v(-2.8, -55.72) * mm, "end": v(-2.92, -59.27) * mm});
            skLineSegment(sketch, "E2322", {"start": v(-2.92, -59.27) * mm, "end": v(1.17, -59.41) * mm});
            skLineSegment(sketch, "E2323", {"start": v(1.17, -59.41) * mm, "end": v(1.3, -55.77) * mm});
            skLineSegment(sketch, "E2324", {"start": v(-27.6, -47.69) * mm, "end": v(-28.46, -47.12) * mm});
            skLineSegment(sketch, "E2325", {"start": v(-28.46, -47.12) * mm, "end": v(-29.31, -46.53) * mm});
            skLineSegment(sketch, "E2326", {"start": v(-29.31, -46.53) * mm, "end": v(-30.15, -45.93) * mm});
            skLineSegment(sketch, "E2327", {"start": v(-30.15, -45.93) * mm, "end": v(-30.97, -45.31) * mm});
            skLineSegment(sketch, "E2328", {"start": v(-30.97, -45.31) * mm, "end": v(-31.28, -49.3) * mm});
            skLineSegment(sketch, "E2329", {"start": v(-31.28, -49.3) * mm, "end": v(-27.6, -47.69) * mm});
            skLineSegment(sketch, "E2330", {"start": v(5.82, 40.35) * mm, "end": v(6.93, 40.2) * mm});
            skLineSegment(sketch, "E2331", {"start": v(6.93, 40.2) * mm, "end": v(8.04, 40.01) * mm});
            skLineSegment(sketch, "E2332", {"start": v(8.04, 40.01) * mm, "end": v(9.14, 39.8) * mm});
            skLineSegment(sketch, "E2333", {"start": v(9.14, 39.8) * mm, "end": v(10.22, 39.57) * mm});
            skLineSegment(sketch, "E2334", {"start": v(10.22, 39.57) * mm, "end": v(11.3, 39.3) * mm});
            skLineSegment(sketch, "E2335", {"start": v(11.3, 39.3) * mm, "end": v(12.37, 39.02) * mm});
            skLineSegment(sketch, "E2336", {"start": v(12.37, 39.02) * mm, "end": v(13.42, 38.7) * mm});
            skLineSegment(sketch, "E2337", {"start": v(13.42, 38.7) * mm, "end": v(14.47, 38.37) * mm});
            skLineSegment(sketch, "E2338", {"start": v(14.47, 38.37) * mm, "end": v(14.26, 37.95) * mm});
            skLineSegment(sketch, "E2339", {"start": v(14.26, 37.95) * mm, "end": v(14.04, 37.53) * mm});
            skLineSegment(sketch, "E2340", {"start": v(14.04, 37.53) * mm, "end": v(13.8, 37.1) * mm});
            skLineSegment(sketch, "E2341", {"start": v(13.8, 37.1) * mm, "end": v(13.56, 36.69) * mm});
            skLineSegment(sketch, "E2342", {"start": v(13.56, 36.69) * mm, "end": v(13.3, 36.27) * mm});
            skLineSegment(sketch, "E2343", {"start": v(13.3, 36.27) * mm, "end": v(13.02, 35.86) * mm});
            skLineSegment(sketch, "E2344", {"start": v(13.02, 35.86) * mm, "end": v(12.73, 35.45) * mm});
            skLineSegment(sketch, "E2345", {"start": v(12.73, 35.45) * mm, "end": v(12.43, 35.05) * mm});
            skLineSegment(sketch, "E2346", {"start": v(12.43, 35.05) * mm, "end": v(12.12, 34.65) * mm});
            skLineSegment(sketch, "E2347", {"start": v(12.12, 34.65) * mm, "end": v(11.8, 34.25) * mm});
            skLineSegment(sketch, "E2348", {"start": v(11.8, 34.25) * mm, "end": v(11.46, 33.86) * mm});
            skLineSegment(sketch, "E2349", {"start": v(11.46, 33.86) * mm, "end": v(11.1, 33.48) * mm});
            skLineSegment(sketch, "E2350", {"start": v(11.1, 33.48) * mm, "end": v(10.75, 33.1) * mm});
            skLineSegment(sketch, "E2351", {"start": v(10.75, 33.1) * mm, "end": v(10.38, 32.73) * mm});
            skLineSegment(sketch, "E2352", {"start": v(10.38, 32.73) * mm, "end": v(10, 32.37) * mm});
            skLineSegment(sketch, "E2353", {"start": v(10, 32.37) * mm, "end": v(9.6, 32.01) * mm});
            skLineSegment(sketch, "E2354", {"start": v(9.6, 32.01) * mm, "end": v(9.2, 31.66) * mm});
            skLineSegment(sketch, "E2355", {"start": v(9.2, 31.66) * mm, "end": v(8.8, 31.33) * mm});
            skLineSegment(sketch, "E2356", {"start": v(8.8, 31.33) * mm, "end": v(8.37, 31) * mm});
            skLineSegment(sketch, "E2357", {"start": v(8.37, 31) * mm, "end": v(7.94, 30.68) * mm});
            skLineSegment(sketch, "E2358", {"start": v(7.94, 30.68) * mm, "end": v(7.5, 30.37) * mm});
            skLineSegment(sketch, "E2359", {"start": v(7.5, 30.37) * mm, "end": v(7.06, 30.08) * mm});
            skLineSegment(sketch, "E2360", {"start": v(7.06, 30.08) * mm, "end": v(6.6, 29.8) * mm});
            skLineSegment(sketch, "E2361", {"start": v(6.6, 29.8) * mm, "end": v(6.14, 29.52) * mm});
            skLineSegment(sketch, "E2362", {"start": v(6.14, 29.52) * mm, "end": v(5.67, 29.26) * mm});
            skLineSegment(sketch, "E2363", {"start": v(5.67, 29.26) * mm, "end": v(5.2, 29.02) * mm});
            skLineSegment(sketch, "E2364", {"start": v(5.2, 29.02) * mm, "end": v(4.7, 28.78) * mm});
            skLineSegment(sketch, "E2365", {"start": v(4.7, 28.78) * mm, "end": v(4.22, 28.57) * mm});
            skLineSegment(sketch, "E2366", {"start": v(4.22, 28.57) * mm, "end": v(3.72, 28.36) * mm});
            skLineSegment(sketch, "E2367", {"start": v(3.72, 28.36) * mm, "end": v(3.22, 28.17) * mm});
            skLineSegment(sketch, "E2368", {"start": v(3.22, 28.17) * mm, "end": v(2.71, 28) * mm});
            skLineSegment(sketch, "E2369", {"start": v(2.71, 28) * mm, "end": v(2.2, 27.84) * mm});
            skLineSegment(sketch, "E2370", {"start": v(2.2, 27.84) * mm, "end": v(2.15, 28.3) * mm});
            skLineSegment(sketch, "E2371", {"start": v(2.15, 28.3) * mm, "end": v(2.11, 28.77) * mm});
            skLineSegment(sketch, "E2372", {"start": v(2.11, 28.77) * mm, "end": v(2.09, 29.23) * mm});
            skLineSegment(sketch, "E2373", {"start": v(2.09, 29.23) * mm, "end": v(2.08, 29.68) * mm});
            skLineSegment(sketch, "E2374", {"start": v(2.08, 29.68) * mm, "end": v(2.08, 30.13) * mm});
            skLineSegment(sketch, "E2375", {"start": v(2.08, 30.13) * mm, "end": v(2.1, 30.58) * mm});
            skLineSegment(sketch, "E2376", {"start": v(2.1, 30.58) * mm, "end": v(2.13, 31.02) * mm});
            skLineSegment(sketch, "E2377", {"start": v(2.13, 31.02) * mm, "end": v(2.17, 31.45) * mm});
            skLineSegment(sketch, "E2378", {"start": v(2.17, 31.45) * mm, "end": v(2.22, 31.89) * mm});
            skLineSegment(sketch, "E2379", {"start": v(2.22, 31.89) * mm, "end": v(2.28, 32.31) * mm});
            skLineSegment(sketch, "E2380", {"start": v(2.28, 32.31) * mm, "end": v(2.36, 32.74) * mm});
            skLineSegment(sketch, "E2381", {"start": v(2.36, 32.74) * mm, "end": v(2.44, 33.16) * mm});
            skLineSegment(sketch, "E2382", {"start": v(2.44, 33.16) * mm, "end": v(2.54, 33.57) * mm});
            skLineSegment(sketch, "E2383", {"start": v(2.54, 33.57) * mm, "end": v(2.64, 33.98) * mm});
            skLineSegment(sketch, "E2384", {"start": v(2.64, 33.98) * mm, "end": v(2.76, 34.38) * mm});
            skLineSegment(sketch, "E2385", {"start": v(2.76, 34.38) * mm, "end": v(2.88, 34.78) * mm});
            skLineSegment(sketch, "E2386", {"start": v(2.88, 34.78) * mm, "end": v(3.02, 35.17) * mm});
            skLineSegment(sketch, "E2387", {"start": v(3.02, 35.17) * mm, "end": v(3.16, 35.56) * mm});
            skLineSegment(sketch, "E2388", {"start": v(3.16, 35.56) * mm, "end": v(3.3, 35.94) * mm});
            skLineSegment(sketch, "E2389", {"start": v(3.3, 35.94) * mm, "end": v(3.46, 36.32) * mm});
            skLineSegment(sketch, "E2390", {"start": v(3.46, 36.32) * mm, "end": v(3.63, 36.69) * mm});
            skLineSegment(sketch, "E2391", {"start": v(3.63, 36.69) * mm, "end": v(3.8, 37.05) * mm});
            skLineSegment(sketch, "E2392", {"start": v(3.8, 37.05) * mm, "end": v(3.98, 37.4) * mm});
            skLineSegment(sketch, "E2393", {"start": v(3.98, 37.4) * mm, "end": v(4.16, 37.76) * mm});
            skLineSegment(sketch, "E2394", {"start": v(4.16, 37.76) * mm, "end": v(4.35, 38.1) * mm});
            skLineSegment(sketch, "E2395", {"start": v(4.35, 38.1) * mm, "end": v(4.55, 38.45) * mm});
            skLineSegment(sketch, "E2396", {"start": v(4.55, 38.45) * mm, "end": v(4.96, 39.1) * mm});
            skLineSegment(sketch, "E2397", {"start": v(4.96, 39.1) * mm, "end": v(5.38, 39.75) * mm});
            skLineSegment(sketch, "E2398", {"start": v(5.38, 39.75) * mm, "end": v(5.82, 40.35) * mm});
            skLineSegment(sketch, "E2399", {"start": v(-14.17, 38.51) * mm, "end": v(-13.14, 38.83) * mm});
            skLineSegment(sketch, "E2400", {"start": v(-13.14, 38.83) * mm, "end": v(-12.1, 39.13) * mm});
            skLineSegment(sketch, "E2401", {"start": v(-12.1, 39.13) * mm, "end": v(-11.06, 39.4) * mm});
            skLineSegment(sketch, "E2402", {"start": v(-11.06, 39.4) * mm, "end": v(-10, 39.65) * mm});
            skLineSegment(sketch, "E2403", {"start": v(-10, 39.65) * mm, "end": v(-8.94, 39.87) * mm});
            skLineSegment(sketch, "E2404", {"start": v(-8.94, 39.87) * mm, "end": v(-7.86, 40.07) * mm});
            skLineSegment(sketch, "E2405", {"start": v(-7.86, 40.07) * mm, "end": v(-6.78, 40.24) * mm});
            skLineSegment(sketch, "E2406", {"start": v(-6.78, 40.24) * mm, "end": v(-5.69, 40.39) * mm});
            skLineSegment(sketch, "E2407", {"start": v(-5.69, 40.39) * mm, "end": v(-5.44, 40.05) * mm});
            skLineSegment(sketch, "E2408", {"start": v(-5.44, 40.05) * mm, "end": v(-5.2, 39.7) * mm});
            skLineSegment(sketch, "E2409", {"start": v(-5.2, 39.7) * mm, "end": v(-4.96, 39.35) * mm});
            skLineSegment(sketch, "E2410", {"start": v(-4.96, 39.35) * mm, "end": v(-4.73, 38.99) * mm});
            skLineSegment(sketch, "E2411", {"start": v(-4.73, 38.99) * mm, "end": v(-4.5, 38.62) * mm});
            skLineSegment(sketch, "E2412", {"start": v(-4.5, 38.62) * mm, "end": v(-4.28, 38.25) * mm});
            skLineSegment(sketch, "E2413", {"start": v(-4.28, 38.25) * mm, "end": v(-4.07, 37.88) * mm});
            skLineSegment(sketch, "E2414", {"start": v(-4.07, 37.88) * mm, "end": v(-3.87, 37.5) * mm});
            skLineSegment(sketch, "E2415", {"start": v(-3.87, 37.5) * mm, "end": v(-3.67, 37.11) * mm});
            skLineSegment(sketch, "E2416", {"start": v(-3.67, 37.11) * mm, "end": v(-3.48, 36.73) * mm});
            skLineSegment(sketch, "E2417", {"start": v(-3.48, 36.73) * mm, "end": v(-3.3, 36.33) * mm});
            skLineSegment(sketch, "E2418", {"start": v(-3.3, 36.33) * mm, "end": v(-3.12, 35.94) * mm});
            skLineSegment(sketch, "E2419", {"start": v(-3.12, 35.94) * mm, "end": v(-2.96, 35.54) * mm});
            skLineSegment(sketch, "E2420", {"start": v(-2.96, 35.54) * mm, "end": v(-2.8, 35.14) * mm});
            skLineSegment(sketch, "E2421", {"start": v(-2.8, 35.14) * mm, "end": v(-2.66, 34.73) * mm});
            skLineSegment(sketch, "E2422", {"start": v(-2.66, 34.73) * mm, "end": v(-2.52, 34.32) * mm});
            skLineSegment(sketch, "E2423", {"start": v(-2.52, 34.32) * mm, "end": v(-2.4, 33.91) * mm});
            skLineSegment(sketch, "E2424", {"start": v(-2.4, 33.91) * mm, "end": v(-2.28, 33.5) * mm});
            skLineSegment(sketch, "E2425", {"start": v(-2.28, 33.5) * mm, "end": v(-2.18, 33.09) * mm});
            skLineSegment(sketch, "E2426", {"start": v(-2.18, 33.09) * mm, "end": v(-2.09, 32.68) * mm});
            skLineSegment(sketch, "E2427", {"start": v(-2.09, 32.68) * mm, "end": v(-2.01, 32.26) * mm});
            skLineSegment(sketch, "E2428", {"start": v(-2.01, 32.26) * mm, "end": v(-1.94, 31.84) * mm});
            skLineSegment(sketch, "E2429", {"start": v(-1.94, 31.84) * mm, "end": v(-1.89, 31.43) * mm});
            skLineSegment(sketch, "E2430", {"start": v(-1.89, 31.43) * mm, "end": v(-1.85, 31.01) * mm});
            skLineSegment(sketch, "E2431", {"start": v(-1.85, 31.01) * mm, "end": v(-1.82, 30.6) * mm});
            skLineSegment(sketch, "E2432", {"start": v(-1.82, 30.6) * mm, "end": v(-1.8, 30.18) * mm});
            skLineSegment(sketch, "E2433", {"start": v(-1.8, 30.18) * mm, "end": v(-1.8, 29.77) * mm});
            skLineSegment(sketch, "E2434", {"start": v(-1.8, 29.77) * mm, "end": v(-1.82, 29.35) * mm});
            skLineSegment(sketch, "E2435", {"start": v(-1.82, 29.35) * mm, "end": v(-1.85, 28.94) * mm});
            skLineSegment(sketch, "E2436", {"start": v(-1.85, 28.94) * mm, "end": v(-1.9, 28.53) * mm});
            skLineSegment(sketch, "E2437", {"start": v(-1.9, 28.53) * mm, "end": v(-1.96, 28.12) * mm});
            skLineSegment(sketch, "E2438", {"start": v(-1.96, 28.12) * mm, "end": v(-2.04, 27.72) * mm});
            skLineSegment(sketch, "E2439", {"start": v(-2.04, 27.72) * mm, "end": v(-2.23, 27.72) * mm});
            skLineSegment(sketch, "E2440", {"start": v(-2.23, 27.72) * mm, "end": v(-2.42, 27.74) * mm});
            skLineSegment(sketch, "E2441", {"start": v(-2.42, 27.74) * mm, "end": v(-2.81, 27.8) * mm});
            skLineSegment(sketch, "E2442", {"start": v(-2.81, 27.8) * mm, "end": v(-3.21, 27.88) * mm});
            skLineSegment(sketch, "E2443", {"start": v(-3.21, 27.88) * mm, "end": v(-3.62, 28) * mm});
            skLineSegment(sketch, "E2444", {"start": v(-3.62, 28) * mm, "end": v(-4.03, 28.13) * mm});
            skLineSegment(sketch, "E2445", {"start": v(-4.03, 28.13) * mm, "end": v(-4.44, 28.3) * mm});
            skLineSegment(sketch, "E2446", {"start": v(-4.44, 28.3) * mm, "end": v(-4.86, 28.5) * mm});
            skLineSegment(sketch, "E2447", {"start": v(-4.86, 28.5) * mm, "end": v(-5.28, 28.72) * mm});
            skLineSegment(sketch, "E2448", {"start": v(-5.28, 28.72) * mm, "end": v(-5.7, 28.96) * mm});
            skLineSegment(sketch, "E2449", {"start": v(-5.7, 28.96) * mm, "end": v(-6.13, 29.23) * mm});
            skLineSegment(sketch, "E2450", {"start": v(-6.13, 29.23) * mm, "end": v(-6.55, 29.52) * mm});
            skLineSegment(sketch, "E2451", {"start": v(-6.55, 29.52) * mm, "end": v(-6.98, 29.83) * mm});
            skLineSegment(sketch, "E2452", {"start": v(-6.98, 29.83) * mm, "end": v(-7.4, 30.16) * mm});
            skLineSegment(sketch, "E2453", {"start": v(-7.4, 30.16) * mm, "end": v(-7.82, 30.5) * mm});
            skLineSegment(sketch, "E2454", {"start": v(-7.82, 30.5) * mm, "end": v(-8.24, 30.86) * mm});
            skLineSegment(sketch, "E2455", {"start": v(-8.24, 30.86) * mm, "end": v(-8.65, 31.24) * mm});
            skLineSegment(sketch, "E2456", {"start": v(-8.65, 31.24) * mm, "end": v(-9.06, 31.64) * mm});
            skLineSegment(sketch, "E2457", {"start": v(-9.06, 31.64) * mm, "end": v(-9.47, 32.04) * mm});
            skLineSegment(sketch, "E2458", {"start": v(-9.47, 32.04) * mm, "end": v(-9.87, 32.46) * mm});
            skLineSegment(sketch, "E2459", {"start": v(-9.87, 32.46) * mm, "end": v(-10.26, 32.9) * mm});
            skLineSegment(sketch, "E2460", {"start": v(-10.26, 32.9) * mm, "end": v(-10.64, 33.33) * mm});
            skLineSegment(sketch, "E2461", {"start": v(-10.64, 33.33) * mm, "end": v(-11.02, 33.78) * mm});
            skLineSegment(sketch, "E2462", {"start": v(-11.02, 33.78) * mm, "end": v(-11.39, 34.24) * mm});
            skLineSegment(sketch, "E2463", {"start": v(-11.39, 34.24) * mm, "end": v(-11.75, 34.7) * mm});
            skLineSegment(sketch, "E2464", {"start": v(-11.75, 34.7) * mm, "end": v(-12.1, 35.17) * mm});
            skLineSegment(sketch, "E2465", {"start": v(-12.1, 35.17) * mm, "end": v(-12.43, 35.65) * mm});
            skLineSegment(sketch, "E2466", {"start": v(-12.43, 35.65) * mm, "end": v(-12.76, 36.12) * mm});
            skLineSegment(sketch, "E2467", {"start": v(-12.76, 36.12) * mm, "end": v(-13.07, 36.6) * mm});
            skLineSegment(sketch, "E2468", {"start": v(-13.07, 36.6) * mm, "end": v(-13.37, 37.08) * mm});
            skLineSegment(sketch, "E2469", {"start": v(-13.37, 37.08) * mm, "end": v(-13.65, 37.56) * mm});
            skLineSegment(sketch, "E2470", {"start": v(-13.65, 37.56) * mm, "end": v(-13.92, 38.04) * mm});
            skLineSegment(sketch, "E2471", {"start": v(-13.92, 38.04) * mm, "end": v(-14.17, 38.51) * mm});
            skLineSegment(sketch, "E2472", {"start": v(56.97, -13.46) * mm, "end": v(52.44, -13.95) * mm});
            skLineSegment(sketch, "E2473", {"start": v(52.44, -13.95) * mm, "end": v(56.48, -16.07) * mm});
            skLineSegment(sketch, "E2474", {"start": v(56.48, -16.07) * mm, "end": v(56.97, -13.46) * mm});
            skLineSegment(sketch, "E2475", {"start": v(11.62, -58.78) * mm, "end": v(13.17, -58.42) * mm});
            skLineSegment(sketch, "E2476", {"start": v(13.17, -58.42) * mm, "end": v(13.32, -58.37) * mm});
            skLineSegment(sketch, "E2477", {"start": v(13.32, -58.37) * mm, "end": v(13.52, -58.3) * mm});
            skLineSegment(sketch, "E2478", {"start": v(13.52, -58.3) * mm, "end": v(13.78, -58.18) * mm});
            skLineSegment(sketch, "E2479", {"start": v(13.78, -58.18) * mm, "end": v(14.1, -58.04) * mm});
            skLineSegment(sketch, "E2480", {"start": v(14.1, -58.04) * mm, "end": v(14.18, -58) * mm});
            skLineSegment(sketch, "E2481", {"start": v(14.18, -58) * mm, "end": v(14.26, -57.95) * mm});
            skLineSegment(sketch, "E2482", {"start": v(14.26, -57.95) * mm, "end": v(14.33, -57.9) * mm});
            skLineSegment(sketch, "E2483", {"start": v(14.33, -57.9) * mm, "end": v(14.4, -57.83) * mm});
            skLineSegment(sketch, "E2484", {"start": v(14.4, -57.83) * mm, "end": v(14.46, -57.76) * mm});
            skLineSegment(sketch, "E2485", {"start": v(14.46, -57.76) * mm, "end": v(14.51, -57.7) * mm});
            skLineSegment(sketch, "E2486", {"start": v(14.51, -57.7) * mm, "end": v(14.56, -57.61) * mm});
            skLineSegment(sketch, "E2487", {"start": v(14.56, -57.61) * mm, "end": v(14.6, -57.53) * mm});
            skLineSegment(sketch, "E2488", {"start": v(14.6, -57.53) * mm, "end": v(14.64, -57.44) * mm});
            skLineSegment(sketch, "E2489", {"start": v(14.64, -57.44) * mm, "end": v(14.67, -57.35) * mm});
            skLineSegment(sketch, "E2490", {"start": v(14.67, -57.35) * mm, "end": v(14.69, -57.26) * mm});
            skLineSegment(sketch, "E2491", {"start": v(14.69, -57.26) * mm, "end": v(14.7, -57.17) * mm});
            skLineSegment(sketch, "E2492", {"start": v(14.7, -57.17) * mm, "end": v(14.7, -57.07) * mm});
            skLineSegment(sketch, "E2493", {"start": v(14.7, -57.07) * mm, "end": v(14.7, -56.98) * mm});
            skLineSegment(sketch, "E2494", {"start": v(14.7, -56.98) * mm, "end": v(14.68, -56.79) * mm});
            skLineSegment(sketch, "E2495", {"start": v(14.68, -56.79) * mm, "end": v(14.64, -56.65) * mm});
            skLineSegment(sketch, "E2496", {"start": v(14.64, -56.65) * mm, "end": v(14.6, -56.52) * mm});
            skLineSegment(sketch, "E2497", {"start": v(14.6, -56.52) * mm, "end": v(14.53, -56.4) * mm});
            skLineSegment(sketch, "E2498", {"start": v(14.53, -56.4) * mm, "end": v(14.47, -56.3) * mm});
            skLineSegment(sketch, "E2499", {"start": v(14.47, -56.3) * mm, "end": v(14.4, -56.2) * mm});
            skLineSegment(sketch, "E2500", {"start": v(14.4, -56.2) * mm, "end": v(14.3, -56.12) * mm});
            skLineSegment(sketch, "E2501", {"start": v(14.3, -56.12) * mm, "end": v(14.21, -56.05) * mm});
            skLineSegment(sketch, "E2502", {"start": v(14.21, -56.05) * mm, "end": v(14.1, -56) * mm});
            skLineSegment(sketch, "E2503", {"start": v(14.1, -56) * mm, "end": v(14, -55.94) * mm});
            skLineSegment(sketch, "E2504", {"start": v(14, -55.94) * mm, "end": v(13.86, -55.9) * mm});
            skLineSegment(sketch, "E2505", {"start": v(13.86, -55.9) * mm, "end": v(13.7, -55.89) * mm});
            skLineSegment(sketch, "E2506", {"start": v(13.7, -55.89) * mm, "end": v(13.53, -55.88) * mm});
            skLineSegment(sketch, "E2507", {"start": v(13.53, -55.88) * mm, "end": v(13.35, -55.89) * mm});
            skLineSegment(sketch, "E2508", {"start": v(13.35, -55.89) * mm, "end": v(13.14, -55.9) * mm});
            skLineSegment(sketch, "E2509", {"start": v(13.14, -55.9) * mm, "end": v(12.92, -55.95) * mm});
            skLineSegment(sketch, "E2510", {"start": v(12.92, -55.95) * mm, "end": v(12.67, -56) * mm});
            skLineSegment(sketch, "E2511", {"start": v(12.67, -56) * mm, "end": v(11.07, -56.37) * mm});
            skLineSegment(sketch, "E2512", {"start": v(11.07, -56.37) * mm, "end": v(11.62, -58.78) * mm});
            skLineSegment(sketch, "E2513", {"start": v(-42.56, -40) * mm, "end": v(-41.52, -41.19) * mm});
            skLineSegment(sketch, "E2514", {"start": v(-41.52, -41.19) * mm, "end": v(-41.4, -41.3) * mm});
            skLineSegment(sketch, "E2515", {"start": v(-41.4, -41.3) * mm, "end": v(-41.24, -41.44) * mm});
            skLineSegment(sketch, "E2516", {"start": v(-41.24, -41.44) * mm, "end": v(-41.02, -41.62) * mm});
            skLineSegment(sketch, "E2517", {"start": v(-41.02, -41.62) * mm, "end": v(-40.74, -41.83) * mm});
            skLineSegment(sketch, "E2518", {"start": v(-40.74, -41.83) * mm, "end": v(-40.67, -41.88) * mm});
            skLineSegment(sketch, "E2519", {"start": v(-40.67, -41.88) * mm, "end": v(-40.59, -41.93) * mm});
            skLineSegment(sketch, "E2520", {"start": v(-40.59, -41.93) * mm, "end": v(-40.5, -41.97) * mm});
            skLineSegment(sketch, "E2521", {"start": v(-40.5, -41.97) * mm, "end": v(-40.42, -42) * mm});
            skLineSegment(sketch, "E2522", {"start": v(-40.42, -42) * mm, "end": v(-40.33, -42.02) * mm});
            skLineSegment(sketch, "E2523", {"start": v(-40.33, -42.02) * mm, "end": v(-40.24, -42.03) * mm});
            skLineSegment(sketch, "E2524", {"start": v(-40.24, -42.03) * mm, "end": v(-40.15, -42.04) * mm});
            skLineSegment(sketch, "E2525", {"start": v(-40.15, -42.04) * mm, "end": v(-40.06, -42.03) * mm});
            skLineSegment(sketch, "E2526", {"start": v(-40.06, -42.03) * mm, "end": v(-39.96, -42.02) * mm});
            skLineSegment(sketch, "E2527", {"start": v(-39.96, -42.02) * mm, "end": v(-39.87, -42) * mm});
            skLineSegment(sketch, "E2528", {"start": v(-39.87, -42) * mm, "end": v(-39.78, -41.98) * mm});
            skLineSegment(sketch, "E2529", {"start": v(-39.78, -41.98) * mm, "end": v(-39.69, -41.95) * mm});
            skLineSegment(sketch, "E2530", {"start": v(-39.69, -41.95) * mm, "end": v(-39.6, -41.91) * mm});
            skLineSegment(sketch, "E2531", {"start": v(-39.6, -41.91) * mm, "end": v(-39.52, -41.86) * mm});
            skLineSegment(sketch, "E2532", {"start": v(-39.52, -41.86) * mm, "end": v(-39.37, -41.75) * mm});
            skLineSegment(sketch, "E2533", {"start": v(-39.37, -41.75) * mm, "end": v(-39.26, -41.65) * mm});
            skLineSegment(sketch, "E2534", {"start": v(-39.26, -41.65) * mm, "end": v(-39.17, -41.55) * mm});
            skLineSegment(sketch, "E2535", {"start": v(-39.17, -41.55) * mm, "end": v(-39.1, -41.44) * mm});
            skLineSegment(sketch, "E2536", {"start": v(-39.1, -41.44) * mm, "end": v(-39.04, -41.34) * mm});
            skLineSegment(sketch, "E2537", {"start": v(-39.04, -41.34) * mm, "end": v(-38.99, -41.23) * mm});
            skLineSegment(sketch, "E2538", {"start": v(-38.99, -41.23) * mm, "end": v(-38.96, -41.11) * mm});
            skLineSegment(sketch, "E2539", {"start": v(-38.96, -41.11) * mm, "end": v(-38.94, -41) * mm});
            skLineSegment(sketch, "E2540", {"start": v(-38.94, -41) * mm, "end": v(-38.93, -40.87) * mm});
            skLineSegment(sketch, "E2541", {"start": v(-38.93, -40.87) * mm, "end": v(-38.94, -40.75) * mm});
            skLineSegment(sketch, "E2542", {"start": v(-38.94, -40.75) * mm, "end": v(-38.98, -40.61) * mm});
            skLineSegment(sketch, "E2543", {"start": v(-38.98, -40.61) * mm, "end": v(-39.03, -40.47) * mm});
            skLineSegment(sketch, "E2544", {"start": v(-39.03, -40.47) * mm, "end": v(-39.1, -40.31) * mm});
            skLineSegment(sketch, "E2545", {"start": v(-39.1, -40.31) * mm, "end": v(-39.2, -40.15) * mm});
            skLineSegment(sketch, "E2546", {"start": v(-39.2, -40.15) * mm, "end": v(-39.32, -39.98) * mm});
            skLineSegment(sketch, "E2547", {"start": v(-39.32, -39.98) * mm, "end": v(-39.46, -39.8) * mm});
            skLineSegment(sketch, "E2548", {"start": v(-39.46, -39.8) * mm, "end": v(-39.61, -39.61) * mm});
            skLineSegment(sketch, "E2549", {"start": v(-39.61, -39.61) * mm, "end": v(-40.7, -38.37) * mm});
            skLineSegment(sketch, "E2550", {"start": v(-40.7, -38.37) * mm, "end": v(-42.56, -40) * mm});
            skLineSegment(sketch, "E2551", {"start": v(-49.88, -28.46) * mm, "end": v(-49.18, -29.88) * mm});
            skLineSegment(sketch, "E2552", {"start": v(-49.18, -29.88) * mm, "end": v(-49.1, -30.02) * mm});
            skLineSegment(sketch, "E2553", {"start": v(-49.1, -30.02) * mm, "end": v(-48.98, -30.2) * mm});
            skLineSegment(sketch, "E2554", {"start": v(-48.98, -30.2) * mm, "end": v(-48.8, -30.43) * mm});
            skLineSegment(sketch, "E2555", {"start": v(-48.8, -30.43) * mm, "end": v(-48.6, -30.7) * mm});
            skLineSegment(sketch, "E2556", {"start": v(-48.6, -30.7) * mm, "end": v(-48.53, -30.77) * mm});
            skLineSegment(sketch, "E2557", {"start": v(-48.53, -30.77) * mm, "end": v(-48.47, -30.84) * mm});
            skLineSegment(sketch, "E2558", {"start": v(-48.47, -30.84) * mm, "end": v(-48.4, -30.9) * mm});
            skLineSegment(sketch, "E2559", {"start": v(-48.4, -30.9) * mm, "end": v(-48.32, -30.95) * mm});
            skLineSegment(sketch, "E2560", {"start": v(-48.32, -30.95) * mm, "end": v(-48.25, -30.99) * mm});
            skLineSegment(sketch, "E2561", {"start": v(-48.25, -30.99) * mm, "end": v(-48.16, -31.03) * mm});
            skLineSegment(sketch, "E2562", {"start": v(-48.16, -31.03) * mm, "end": v(-48.07, -31.05) * mm});
            skLineSegment(sketch, "E2563", {"start": v(-48.07, -31.05) * mm, "end": v(-47.98, -31.08) * mm});
            skLineSegment(sketch, "E2564", {"start": v(-47.98, -31.08) * mm, "end": v(-47.89, -31.1) * mm});
            skLineSegment(sketch, "E2565", {"start": v(-47.89, -31.1) * mm, "end": v(-47.8, -31.1) * mm});
            skLineSegment(sketch, "E2566", {"start": v(-47.8, -31.1) * mm, "end": v(-47.7, -31.1) * mm});
            skLineSegment(sketch, "E2567", {"start": v(-47.7, -31.1) * mm, "end": v(-47.6, -31.09) * mm});
            skLineSegment(sketch, "E2568", {"start": v(-47.6, -31.09) * mm, "end": v(-47.51, -31.07) * mm});
            skLineSegment(sketch, "E2569", {"start": v(-47.51, -31.07) * mm, "end": v(-47.42, -31.05) * mm});
            skLineSegment(sketch, "E2570", {"start": v(-47.42, -31.05) * mm, "end": v(-47.24, -30.98) * mm});
            skLineSegment(sketch, "E2571", {"start": v(-47.24, -30.98) * mm, "end": v(-47.12, -30.9) * mm});
            skLineSegment(sketch, "E2572", {"start": v(-47.12, -30.9) * mm, "end": v(-47, -30.83) * mm});
            skLineSegment(sketch, "E2573", {"start": v(-47, -30.83) * mm, "end": v(-46.9, -30.75) * mm});
            skLineSegment(sketch, "E2574", {"start": v(-46.9, -30.75) * mm, "end": v(-46.82, -30.66) * mm});
            skLineSegment(sketch, "E2575", {"start": v(-46.82, -30.66) * mm, "end": v(-46.74, -30.57) * mm});
            skLineSegment(sketch, "E2576", {"start": v(-46.74, -30.57) * mm, "end": v(-46.68, -30.47) * mm});
            skLineSegment(sketch, "E2577", {"start": v(-46.68, -30.47) * mm, "end": v(-46.63, -30.36) * mm});
            skLineSegment(sketch, "E2578", {"start": v(-46.63, -30.36) * mm, "end": v(-46.6, -30.24) * mm});
            skLineSegment(sketch, "E2579", {"start": v(-46.6, -30.24) * mm, "end": v(-46.58, -30.12) * mm});
            skLineSegment(sketch, "E2580", {"start": v(-46.58, -30.12) * mm, "end": v(-46.57, -29.98) * mm});
            skLineSegment(sketch, "E2581", {"start": v(-46.57, -29.98) * mm, "end": v(-46.59, -29.82) * mm});
            skLineSegment(sketch, "E2582", {"start": v(-46.59, -29.82) * mm, "end": v(-46.62, -29.66) * mm});
            skLineSegment(sketch, "E2583", {"start": v(-46.62, -29.66) * mm, "end": v(-46.67, -29.48) * mm});
            skLineSegment(sketch, "E2584", {"start": v(-46.67, -29.48) * mm, "end": v(-46.74, -29.28) * mm});
            skLineSegment(sketch, "E2585", {"start": v(-46.74, -29.28) * mm, "end": v(-46.83, -29.07) * mm});
            skLineSegment(sketch, "E2586", {"start": v(-46.83, -29.07) * mm, "end": v(-46.93, -28.85) * mm});
            skLineSegment(sketch, "E2587", {"start": v(-46.93, -28.85) * mm, "end": v(-47.66, -27.37) * mm});
            skLineSegment(sketch, "E2588", {"start": v(-47.66, -27.37) * mm, "end": v(-49.88, -28.46) * mm});
            skLineSegment(sketch, "E2589", {"start": v(22.89, -22.77) * mm, "end": v(23.35, -22.92) * mm});
            skLineSegment(sketch, "E2590", {"start": v(23.35, -22.92) * mm, "end": v(23.81, -23.06) * mm});
            skLineSegment(sketch, "E2591", {"start": v(23.81, -23.06) * mm, "end": v(24.27, -23.18) * mm});
            skLineSegment(sketch, "E2592", {"start": v(24.27, -23.18) * mm, "end": v(24.72, -23.29) * mm});
            skLineSegment(sketch, "E2593", {"start": v(24.72, -23.29) * mm, "end": v(25.16, -23.37) * mm});
            skLineSegment(sketch, "E2594", {"start": v(25.16, -23.37) * mm, "end": v(25.59, -23.44) * mm});
            skLineSegment(sketch, "E2595", {"start": v(25.59, -23.44) * mm, "end": v(26.01, -23.5) * mm});
            skLineSegment(sketch, "E2596", {"start": v(26.01, -23.5) * mm, "end": v(26.43, -23.53) * mm});
            skLineSegment(sketch, "E2597", {"start": v(26.43, -23.53) * mm, "end": v(26.84, -23.54) * mm});
            skLineSegment(sketch, "E2598", {"start": v(26.84, -23.54) * mm, "end": v(27.23, -23.54) * mm});
            skLineSegment(sketch, "E2599", {"start": v(27.23, -23.54) * mm, "end": v(27.62, -23.5) * mm});
            skLineSegment(sketch, "E2600", {"start": v(27.62, -23.5) * mm, "end": v(28, -23.46) * mm});
            skLineSegment(sketch, "E2601", {"start": v(28, -23.46) * mm, "end": v(28.36, -23.4) * mm});
            skLineSegment(sketch, "E2602", {"start": v(28.36, -23.4) * mm, "end": v(28.71, -23.3) * mm});
            skLineSegment(sketch, "E2603", {"start": v(28.71, -23.3) * mm, "end": v(29.05, -23.19) * mm});
            skLineSegment(sketch, "E2604", {"start": v(29.05, -23.19) * mm, "end": v(29.37, -23.05) * mm});
            skLineSegment(sketch, "E2605", {"start": v(29.37, -23.05) * mm, "end": v(29.69, -22.9) * mm});
            skLineSegment(sketch, "E2606", {"start": v(29.69, -22.9) * mm, "end": v(29.98, -22.7) * mm});
            skLineSegment(sketch, "E2607", {"start": v(29.98, -22.7) * mm, "end": v(30.26, -22.5) * mm});
            skLineSegment(sketch, "E2608", {"start": v(30.26, -22.5) * mm, "end": v(30.53, -22.26) * mm});
            skLineSegment(sketch, "E2609", {"start": v(30.53, -22.26) * mm, "end": v(30.78, -22) * mm});
            skLineSegment(sketch, "E2610", {"start": v(30.78, -22) * mm, "end": v(31.01, -21.71) * mm});
            skLineSegment(sketch, "E2611", {"start": v(31.01, -21.71) * mm, "end": v(31.23, -21.4) * mm});
            skLineSegment(sketch, "E2612", {"start": v(31.23, -21.4) * mm, "end": v(31.42, -21.06) * mm});
            skLineSegment(sketch, "E2613", {"start": v(31.42, -21.06) * mm, "end": v(31.6, -20.69) * mm});
            skLineSegment(sketch, "E2614", {"start": v(31.6, -20.69) * mm, "end": v(31.76, -20.29) * mm});
            skLineSegment(sketch, "E2615", {"start": v(31.76, -20.29) * mm, "end": v(31.9, -19.86) * mm});
            skLineSegment(sketch, "E2616", {"start": v(31.9, -19.86) * mm, "end": v(32.02, -19.4) * mm});
            skLineSegment(sketch, "E2617", {"start": v(32.02, -19.4) * mm, "end": v(32.12, -18.92) * mm});
            skLineSegment(sketch, "E2618", {"start": v(32.12, -18.92) * mm, "end": v(32.2, -18.4) * mm});
            skLineSegment(sketch, "E2619", {"start": v(32.2, -18.4) * mm, "end": v(32.26, -17.85) * mm});
            skLineSegment(sketch, "E2620", {"start": v(32.26, -17.85) * mm, "end": v(32.3, -17.27) * mm});
            skLineSegment(sketch, "E2621", {"start": v(32.3, -17.27) * mm, "end": v(25, -20.64) * mm});
            skLineSegment(sketch, "E2622", {"start": v(25, -20.64) * mm, "end": v(24.26, -21.11) * mm});
            skLineSegment(sketch, "E2623", {"start": v(24.26, -21.11) * mm, "end": v(23.79, -21.43) * mm});
            skLineSegment(sketch, "E2624", {"start": v(23.79, -21.43) * mm, "end": v(23.63, -21.54) * mm});
            skLineSegment(sketch, "E2625", {"start": v(23.63, -21.54) * mm, "end": v(23.51, -21.63) * mm});
            skLineSegment(sketch, "E2626", {"start": v(23.51, -21.63) * mm, "end": v(23.43, -21.71) * mm});
            skLineSegment(sketch, "E2627", {"start": v(23.43, -21.71) * mm, "end": v(23.38, -21.78) * mm});
            skLineSegment(sketch, "E2628", {"start": v(23.38, -21.78) * mm, "end": v(23.34, -21.85) * mm});
            skLineSegment(sketch, "E2629", {"start": v(23.34, -21.85) * mm, "end": v(23.31, -21.92) * mm});
            skLineSegment(sketch, "E2630", {"start": v(23.31, -21.92) * mm, "end": v(23.25, -22.1) * mm});
            skLineSegment(sketch, "E2631", {"start": v(23.25, -22.1) * mm, "end": v(23.2, -22.22) * mm});
            skLineSegment(sketch, "E2632", {"start": v(23.2, -22.22) * mm, "end": v(23.13, -22.37) * mm});
            skLineSegment(sketch, "E2633", {"start": v(23.13, -22.37) * mm, "end": v(23.03, -22.55) * mm});
            skLineSegment(sketch, "E2634", {"start": v(23.03, -22.55) * mm, "end": v(22.89, -22.77) * mm});
            skLineSegment(sketch, "E2635", {"start": v(-22.73, -22.77) * mm, "end": v(-22.89, -22.54) * mm});
            skLineSegment(sketch, "E2636", {"start": v(-22.89, -22.54) * mm, "end": v(-23.07, -22.32) * mm});
            skLineSegment(sketch, "E2637", {"start": v(-23.07, -22.32) * mm, "end": v(-23.26, -22.1) * mm});
            skLineSegment(sketch, "E2638", {"start": v(-23.26, -22.1) * mm, "end": v(-23.47, -21.87) * mm});
            skLineSegment(sketch, "E2639", {"start": v(-23.47, -21.87) * mm, "end": v(-23.7, -21.65) * mm});
            skLineSegment(sketch, "E2640", {"start": v(-23.7, -21.65) * mm, "end": v(-23.94, -21.43) * mm});
            skLineSegment(sketch, "E2641", {"start": v(-23.94, -21.43) * mm, "end": v(-24.2, -21.22) * mm});
            skLineSegment(sketch, "E2642", {"start": v(-24.2, -21.22) * mm, "end": v(-24.46, -21) * mm});
            skLineSegment(sketch, "E2643", {"start": v(-24.46, -21) * mm, "end": v(-24.74, -20.79) * mm});
            skLineSegment(sketch, "E2644", {"start": v(-24.74, -20.79) * mm, "end": v(-25.03, -20.58) * mm});
            skLineSegment(sketch, "E2645", {"start": v(-25.03, -20.58) * mm, "end": v(-25.63, -20.17) * mm});
            skLineSegment(sketch, "E2646", {"start": v(-25.63, -20.17) * mm, "end": v(-26.26, -19.77) * mm});
            skLineSegment(sketch, "E2647", {"start": v(-26.26, -19.77) * mm, "end": v(-26.92, -19.4) * mm});
            skLineSegment(sketch, "E2648", {"start": v(-26.92, -19.4) * mm, "end": v(-27.6, -19.04) * mm});
            skLineSegment(sketch, "E2649", {"start": v(-27.6, -19.04) * mm, "end": v(-28.27, -18.7) * mm});
            skLineSegment(sketch, "E2650", {"start": v(-28.27, -18.7) * mm, "end": v(-28.96, -18.39) * mm});
            skLineSegment(sketch, "E2651", {"start": v(-28.96, -18.39) * mm, "end": v(-29.63, -18.1) * mm});
            skLineSegment(sketch, "E2652", {"start": v(-29.63, -18.1) * mm, "end": v(-30.3, -17.84) * mm});
            skLineSegment(sketch, "E2653", {"start": v(-30.3, -17.84) * mm, "end": v(-30.94, -17.62) * mm});
            skLineSegment(sketch, "E2654", {"start": v(-30.94, -17.62) * mm, "end": v(-31.55, -17.42) * mm});
            skLineSegment(sketch, "E2655", {"start": v(-31.55, -17.42) * mm, "end": v(-32.13, -17.27) * mm});
            skLineSegment(sketch, "E2656", {"start": v(-32.13, -17.27) * mm, "end": v(-32.1, -17.85) * mm});
            skLineSegment(sketch, "E2657", {"start": v(-32.1, -17.85) * mm, "end": v(-32.04, -18.4) * mm});
            skLineSegment(sketch, "E2658", {"start": v(-32.04, -18.4) * mm, "end": v(-31.96, -18.91) * mm});
            skLineSegment(sketch, "E2659", {"start": v(-31.96, -18.91) * mm, "end": v(-31.86, -19.4) * mm});
            skLineSegment(sketch, "E2660", {"start": v(-31.86, -19.4) * mm, "end": v(-31.74, -19.86) * mm});
            skLineSegment(sketch, "E2661", {"start": v(-31.74, -19.86) * mm, "end": v(-31.6, -20.29) * mm});
            skLineSegment(sketch, "E2662", {"start": v(-31.6, -20.29) * mm, "end": v(-31.44, -20.68) * mm});
            skLineSegment(sketch, "E2663", {"start": v(-31.44, -20.68) * mm, "end": v(-31.26, -21.06) * mm});
            skLineSegment(sketch, "E2664", {"start": v(-31.26, -21.06) * mm, "end": v(-31.07, -21.4) * mm});
            skLineSegment(sketch, "E2665", {"start": v(-31.07, -21.4) * mm, "end": v(-30.85, -21.71) * mm});
            skLineSegment(sketch, "E2666", {"start": v(-30.85, -21.71) * mm, "end": v(-30.62, -22) * mm});
            skLineSegment(sketch, "E2667", {"start": v(-30.62, -22) * mm, "end": v(-30.37, -22.26) * mm});
            skLineSegment(sketch, "E2668", {"start": v(-30.37, -22.26) * mm, "end": v(-30.1, -22.5) * mm});
            skLineSegment(sketch, "E2669", {"start": v(-30.1, -22.5) * mm, "end": v(-29.82, -22.7) * mm});
            skLineSegment(sketch, "E2670", {"start": v(-29.82, -22.7) * mm, "end": v(-29.52, -22.9) * mm});
            skLineSegment(sketch, "E2671", {"start": v(-29.52, -22.9) * mm, "end": v(-29.21, -23.05) * mm});
            skLineSegment(sketch, "E2672", {"start": v(-29.21, -23.05) * mm, "end": v(-28.89, -23.19) * mm});
            skLineSegment(sketch, "E2673", {"start": v(-28.89, -23.19) * mm, "end": v(-28.55, -23.3) * mm});
            skLineSegment(sketch, "E2674", {"start": v(-28.55, -23.3) * mm, "end": v(-28.2, -23.4) * mm});
            skLineSegment(sketch, "E2675", {"start": v(-28.2, -23.4) * mm, "end": v(-27.83, -23.46) * mm});
            skLineSegment(sketch, "E2676", {"start": v(-27.83, -23.46) * mm, "end": v(-27.46, -23.51) * mm});
            skLineSegment(sketch, "E2677", {"start": v(-27.46, -23.51) * mm, "end": v(-27.07, -23.54) * mm});
            skLineSegment(sketch, "E2678", {"start": v(-27.07, -23.54) * mm, "end": v(-26.68, -23.55) * mm});
            skLineSegment(sketch, "E2679", {"start": v(-26.68, -23.55) * mm, "end": v(-26.27, -23.53) * mm});
            skLineSegment(sketch, "E2680", {"start": v(-26.27, -23.53) * mm, "end": v(-25.85, -23.5) * mm});
            skLineSegment(sketch, "E2681", {"start": v(-25.85, -23.5) * mm, "end": v(-25.43, -23.45) * mm});
            skLineSegment(sketch, "E2682", {"start": v(-25.43, -23.45) * mm, "end": v(-25, -23.38) * mm});
            skLineSegment(sketch, "E2683", {"start": v(-25, -23.38) * mm, "end": v(-24.55, -23.29) * mm});
            skLineSegment(sketch, "E2684", {"start": v(-24.55, -23.29) * mm, "end": v(-24.1, -23.18) * mm});
            skLineSegment(sketch, "E2685", {"start": v(-24.1, -23.18) * mm, "end": v(-23.65, -23.06) * mm});
            skLineSegment(sketch, "E2686", {"start": v(-23.65, -23.06) * mm, "end": v(-23.2, -22.92) * mm});
            skLineSegment(sketch, "E2687", {"start": v(-23.2, -22.92) * mm, "end": v(-22.73, -22.77) * mm});
            skLineSegment(sketch, "E2688", {"start": v(7.82, -19.53) * mm, "end": v(7.98, -25.74) * mm});
            skLineSegment(sketch, "E2689", {"start": v(7.98, -25.74) * mm, "end": v(8.35, -25.6) * mm});
            skLineSegment(sketch, "E2690", {"start": v(8.35, -25.6) * mm, "end": v(8.88, -25.36) * mm});
            skLineSegment(sketch, "E2691", {"start": v(8.88, -25.36) * mm, "end": v(9.54, -25.05) * mm});
            skLineSegment(sketch, "E2692", {"start": v(9.54, -25.05) * mm, "end": v(10.33, -24.67) * mm});
            skLineSegment(sketch, "E2693", {"start": v(10.33, -24.67) * mm, "end": v(12.25, -23.7) * mm});
            skLineSegment(sketch, "E2694", {"start": v(12.25, -23.7) * mm, "end": v(14.56, -22.5) * mm});
            skLineSegment(sketch, "E2695", {"start": v(14.56, -22.5) * mm, "end": v(17.19, -21.13) * mm});
            skLineSegment(sketch, "E2696", {"start": v(17.19, -21.13) * mm, "end": v(20.04, -19.6) * mm});
            skLineSegment(sketch, "E2697", {"start": v(20.04, -19.6) * mm, "end": v(23.04, -18) * mm});
            skLineSegment(sketch, "E2698", {"start": v(23.04, -18) * mm, "end": v(26.1, -16.33) * mm});
            skLineSegment(sketch, "E2699", {"start": v(26.1, -16.33) * mm, "end": v(29.15, -14.65) * mm});
            skLineSegment(sketch, "E2700", {"start": v(29.15, -14.65) * mm, "end": v(32.1, -13.02) * mm});
            skLineSegment(sketch, "E2701", {"start": v(32.1, -13.02) * mm, "end": v(34.87, -11.46) * mm});
            skLineSegment(sketch, "E2702", {"start": v(34.87, -11.46) * mm, "end": v(37.37, -10.03) * mm});
            skLineSegment(sketch, "E2703", {"start": v(37.37, -10.03) * mm, "end": v(39.54, -8.77) * mm});
            skLineSegment(sketch, "E2704", {"start": v(39.54, -8.77) * mm, "end": v(40.47, -8.22) * mm});
            skLineSegment(sketch, "E2705", {"start": v(40.47, -8.22) * mm, "end": v(41.28, -7.73) * mm});
            skLineSegment(sketch, "E2706", {"start": v(41.28, -7.73) * mm, "end": v(41.96, -7.3) * mm});
            skLineSegment(sketch, "E2707", {"start": v(41.96, -7.3) * mm, "end": v(42.51, -6.94) * mm});
            skLineSegment(sketch, "E2708", {"start": v(42.51, -6.94) * mm, "end": v(42.92, -6.66) * mm});
            skLineSegment(sketch, "E2709", {"start": v(42.92, -6.66) * mm, "end": v(43.06, -6.55) * mm});
            skLineSegment(sketch, "E2710", {"start": v(43.06, -6.55) * mm, "end": v(43.16, -6.46) * mm});
            skLineSegment(sketch, "E2711", {"start": v(43.16, -6.46) * mm, "end": v(38.17, -3.13) * mm});
            skLineSegment(sketch, "E2712", {"start": v(38.17, -3.13) * mm, "end": v(7.82, -19.53) * mm});
            skLineSegment(sketch, "E2713", {"start": v(-42.97, -6.5) * mm, "end": v(-42.87, -6.6) * mm});
            skLineSegment(sketch, "E2714", {"start": v(-42.87, -6.6) * mm, "end": v(-42.73, -6.7) * mm});
            skLineSegment(sketch, "E2715", {"start": v(-42.73, -6.7) * mm, "end": v(-42.33, -6.98) * mm});
            skLineSegment(sketch, "E2716", {"start": v(-42.33, -6.98) * mm, "end": v(-41.78, -7.33) * mm});
            skLineSegment(sketch, "E2717", {"start": v(-41.78, -7.33) * mm, "end": v(-41.1, -7.76) * mm});
            skLineSegment(sketch, "E2718", {"start": v(-41.1, -7.76) * mm, "end": v(-40.29, -8.25) * mm});
            skLineSegment(sketch, "E2719", {"start": v(-40.29, -8.25) * mm, "end": v(-39.36, -8.8) * mm});
            skLineSegment(sketch, "E2720", {"start": v(-39.36, -8.8) * mm, "end": v(-37.2, -10.05) * mm});
            skLineSegment(sketch, "E2721", {"start": v(-37.2, -10.05) * mm, "end": v(-34.7, -11.47) * mm});
            skLineSegment(sketch, "E2722", {"start": v(-34.7, -11.47) * mm, "end": v(-31.92, -13.03) * mm});
            skLineSegment(sketch, "E2723", {"start": v(-31.92, -13.03) * mm, "end": v(-28.97, -14.66) * mm});
            skLineSegment(sketch, "E2724", {"start": v(-28.97, -14.66) * mm, "end": v(-25.92, -16.33) * mm});
            skLineSegment(sketch, "E2725", {"start": v(-25.92, -16.33) * mm, "end": v(-22.86, -18) * mm});
            skLineSegment(sketch, "E2726", {"start": v(-22.86, -18) * mm, "end": v(-19.85, -19.61) * mm});
            skLineSegment(sketch, "E2727", {"start": v(-19.85, -19.61) * mm, "end": v(-17, -21.13) * mm});
            skLineSegment(sketch, "E2728", {"start": v(-17, -21.13) * mm, "end": v(-14.36, -22.51) * mm});
            skLineSegment(sketch, "E2729", {"start": v(-14.36, -22.51) * mm, "end": v(-12.03, -23.7) * mm});
            skLineSegment(sketch, "E2730", {"start": v(-12.03, -23.7) * mm, "end": v(-11.01, -24.22) * mm});
            skLineSegment(sketch, "E2731", {"start": v(-11.01, -24.22) * mm, "end": v(-10.1, -24.67) * mm});
            skLineSegment(sketch, "E2732", {"start": v(-10.1, -24.67) * mm, "end": v(-9.3, -25.05) * mm});
            skLineSegment(sketch, "E2733", {"start": v(-9.3, -25.05) * mm, "end": v(-8.63, -25.36) * mm});
            skLineSegment(sketch, "E2734", {"start": v(-8.63, -25.36) * mm, "end": v(-8.1, -25.6) * mm});
            skLineSegment(sketch, "E2735", {"start": v(-8.1, -25.6) * mm, "end": v(-7.72, -25.74) * mm});
            skLineSegment(sketch, "E2736", {"start": v(-7.72, -25.74) * mm, "end": v(-7.53, -19.29) * mm});
            skLineSegment(sketch, "E2737", {"start": v(-7.53, -19.29) * mm, "end": v(-38.03, -3.22) * mm});
            skLineSegment(sketch, "E2738", {"start": v(-38.03, -3.22) * mm, "end": v(-42.97, -6.5) * mm});
            skLineSegment(sketch, "E2739", {"start": v(2.47, 15.5) * mm, "end": v(2.6, 14.93) * mm});
            skLineSegment(sketch, "E2740", {"start": v(2.6, 14.93) * mm, "end": v(2.74, 14.38) * mm});
            skLineSegment(sketch, "E2741", {"start": v(2.74, 14.38) * mm, "end": v(2.9, 13.84) * mm});
            skLineSegment(sketch, "E2742", {"start": v(2.9, 13.84) * mm, "end": v(3.05, 13.3) * mm});
            skLineSegment(sketch, "E2743", {"start": v(3.05, 13.3) * mm, "end": v(3.38, 12.29) * mm});
            skLineSegment(sketch, "E2744", {"start": v(3.38, 12.29) * mm, "end": v(3.71, 11.3) * mm});
            skLineSegment(sketch, "E2745", {"start": v(3.71, 11.3) * mm, "end": v(4.05, 10.33) * mm});
            skLineSegment(sketch, "E2746", {"start": v(4.05, 10.33) * mm, "end": v(4.36, 9.37) * mm});
            skLineSegment(sketch, "E2747", {"start": v(4.36, 9.37) * mm, "end": v(4.51, 8.9) * mm});
            skLineSegment(sketch, "E2748", {"start": v(4.51, 8.9) * mm, "end": v(4.65, 8.42) * mm});
            skLineSegment(sketch, "E2749", {"start": v(4.65, 8.42) * mm, "end": v(4.79, 7.93) * mm});
            skLineSegment(sketch, "E2750", {"start": v(4.79, 7.93) * mm, "end": v(4.9, 7.45) * mm});
            skLineSegment(sketch, "E2751", {"start": v(4.9, 7.45) * mm, "end": v(5.01, 6.95) * mm});
            skLineSegment(sketch, "E2752", {"start": v(5.01, 6.95) * mm, "end": v(5.1, 6.45) * mm});
            skLineSegment(sketch, "E2753", {"start": v(5.1, 6.45) * mm, "end": v(5.18, 5.94) * mm});
            skLineSegment(sketch, "E2754", {"start": v(5.18, 5.94) * mm, "end": v(5.24, 5.43) * mm});
            skLineSegment(sketch, "E2755", {"start": v(5.24, 5.43) * mm, "end": v(5.28, 4.9) * mm});
            skLineSegment(sketch, "E2756", {"start": v(5.28, 4.9) * mm, "end": v(5.3, 4.35) * mm});
            skLineSegment(sketch, "E2757", {"start": v(5.3, 4.35) * mm, "end": v(5.3, 3.8) * mm});
            skLineSegment(sketch, "E2758", {"start": v(5.3, 3.8) * mm, "end": v(5.28, 3.22) * mm});
            skLineSegment(sketch, "E2759", {"start": v(5.28, 3.22) * mm, "end": v(5.23, 2.63) * mm});
            skLineSegment(sketch, "E2760", {"start": v(5.23, 2.63) * mm, "end": v(5.15, 2.02) * mm});
            skLineSegment(sketch, "E2761", {"start": v(5.15, 2.02) * mm, "end": v(5.05, 1.39) * mm});
            skLineSegment(sketch, "E2762", {"start": v(5.05, 1.39) * mm, "end": v(4.91, 0.73) * mm});
            skLineSegment(sketch, "E2763", {"start": v(4.91, 0.73) * mm, "end": v(4.75, 0.06) * mm});
            skLineSegment(sketch, "E2764", {"start": v(4.75, 0.06) * mm, "end": v(4.55, -0.64) * mm});
            skLineSegment(sketch, "E2765", {"start": v(4.55, -0.64) * mm, "end": v(4.32, -1.37) * mm});
            skLineSegment(sketch, "E2766", {"start": v(4.32, -1.37) * mm, "end": v(4.05, -2.12) * mm});
            skLineSegment(sketch, "E2767", {"start": v(4.05, -2.12) * mm, "end": v(3.8, -2.76) * mm});
            skLineSegment(sketch, "E2768", {"start": v(3.8, -2.76) * mm, "end": v(3.56, -3.36) * mm});
            skLineSegment(sketch, "E2769", {"start": v(3.56, -3.36) * mm, "end": v(3.33, -3.94) * mm});
            skLineSegment(sketch, "E2770", {"start": v(3.33, -3.94) * mm, "end": v(3.23, -4.22) * mm});
            skLineSegment(sketch, "E2771", {"start": v(3.23, -4.22) * mm, "end": v(3.14, -4.5) * mm});
            skLineSegment(sketch, "E2772", {"start": v(3.14, -4.5) * mm, "end": v(3.05, -4.79) * mm});
            skLineSegment(sketch, "E2773", {"start": v(3.05, -4.79) * mm, "end": v(2.98, -5.08) * mm});
            skLineSegment(sketch, "E2774", {"start": v(2.98, -5.08) * mm, "end": v(2.91, -5.37) * mm});
            skLineSegment(sketch, "E2775", {"start": v(2.91, -5.37) * mm, "end": v(2.87, -5.67) * mm});
            skLineSegment(sketch, "E2776", {"start": v(2.87, -5.67) * mm, "end": v(2.83, -5.98) * mm});
            skLineSegment(sketch, "E2777", {"start": v(2.83, -5.98) * mm, "end": v(2.82, -6.3) * mm});
            skLineSegment(sketch, "E2778", {"start": v(2.82, -6.3) * mm, "end": v(2.82, -6.63) * mm});
            skLineSegment(sketch, "E2779", {"start": v(2.82, -6.63) * mm, "end": v(2.84, -6.98) * mm});
            skLineSegment(sketch, "E2780", {"start": v(2.84, -6.98) * mm, "end": v(2.89, -7.34) * mm});
            skLineSegment(sketch, "E2781", {"start": v(2.89, -7.34) * mm, "end": v(2.95, -7.72) * mm});
            skLineSegment(sketch, "E2782", {"start": v(2.95, -7.72) * mm, "end": v(3.04, -8.12) * mm});
            skLineSegment(sketch, "E2783", {"start": v(3.04, -8.12) * mm, "end": v(3.16, -8.54) * mm});
            skLineSegment(sketch, "E2784", {"start": v(3.16, -8.54) * mm, "end": v(3.3, -8.98) * mm});
            skLineSegment(sketch, "E2785", {"start": v(3.3, -8.98) * mm, "end": v(3.47, -9.45) * mm});
            skLineSegment(sketch, "E2786", {"start": v(3.47, -9.45) * mm, "end": v(3.67, -9.95) * mm});
            skLineSegment(sketch, "E2787", {"start": v(3.67, -9.95) * mm, "end": v(3.9, -10.48) * mm});
            skLineSegment(sketch, "E2788", {"start": v(3.9, -10.48) * mm, "end": v(4.16, -11.04) * mm});
            skLineSegment(sketch, "E2789", {"start": v(4.16, -11.04) * mm, "end": v(4.46, -11.63) * mm});
            skLineSegment(sketch, "E2790", {"start": v(4.46, -11.63) * mm, "end": v(4.8, -12.25) * mm});
            skLineSegment(sketch, "E2791", {"start": v(4.8, -12.25) * mm, "end": v(5.16, -12.91) * mm});
            skLineSegment(sketch, "E2792", {"start": v(5.16, -12.91) * mm, "end": v(5.57, -13.6) * mm});
            skLineSegment(sketch, "E2793", {"start": v(5.57, -13.6) * mm, "end": v(6.02, -14.35) * mm});
            skLineSegment(sketch, "E2794", {"start": v(6.02, -14.35) * mm, "end": v(6.5, -15.13) * mm});
            skLineSegment(sketch, "E2795", {"start": v(6.5, -15.13) * mm, "end": v(7.03, -15.95) * mm});
            skLineSegment(sketch, "E2796", {"start": v(7.03, -15.95) * mm, "end": v(35.59, -0.57) * mm});
            skLineSegment(sketch, "E2797", {"start": v(35.59, -0.57) * mm, "end": v(35.24, 0.17) * mm});
            skLineSegment(sketch, "E2798", {"start": v(35.24, 0.17) * mm, "end": v(34.77, 1.1) * mm});
            skLineSegment(sketch, "E2799", {"start": v(34.77, 1.1) * mm, "end": v(34.2, 2.18) * mm});
            skLineSegment(sketch, "E2800", {"start": v(34.2, 2.18) * mm, "end": v(33.54, 3.38) * mm});
            skLineSegment(sketch, "E2801", {"start": v(33.54, 3.38) * mm, "end": v(32.81, 4.7) * mm});
            skLineSegment(sketch, "E2802", {"start": v(32.81, 4.7) * mm, "end": v(32.02, 6.07) * mm});
            skLineSegment(sketch, "E2803", {"start": v(32.02, 6.07) * mm, "end": v(31.19, 7.49) * mm});
            skLineSegment(sketch, "E2804", {"start": v(31.19, 7.49) * mm, "end": v(30.33, 8.91) * mm});
            skLineSegment(sketch, "E2805", {"start": v(30.33, 8.91) * mm, "end": v(29.45, 10.32) * mm});
            skLineSegment(sketch, "E2806", {"start": v(29.45, 10.32) * mm, "end": v(28.57, 11.68) * mm});
            skLineSegment(sketch, "E2807", {"start": v(28.57, 11.68) * mm, "end": v(28.14, 12.34) * mm});
            skLineSegment(sketch, "E2808", {"start": v(28.14, 12.34) * mm, "end": v(27.71, 12.97) * mm});
            skLineSegment(sketch, "E2809", {"start": v(27.71, 12.97) * mm, "end": v(27.3, 13.57) * mm});
            skLineSegment(sketch, "E2810", {"start": v(27.3, 13.57) * mm, "end": v(26.88, 14.15) * mm});
            skLineSegment(sketch, "E2811", {"start": v(26.88, 14.15) * mm, "end": v(26.48, 14.7) * mm});
            skLineSegment(sketch, "E2812", {"start": v(26.48, 14.7) * mm, "end": v(26.09, 15.2) * mm});
            skLineSegment(sketch, "E2813", {"start": v(26.09, 15.2) * mm, "end": v(25.71, 15.66) * mm});
            skLineSegment(sketch, "E2814", {"start": v(25.71, 15.66) * mm, "end": v(25.36, 16.08) * mm});
            skLineSegment(sketch, "E2815", {"start": v(25.36, 16.08) * mm, "end": v(25.02, 16.45) * mm});
            skLineSegment(sketch, "E2816", {"start": v(25.02, 16.45) * mm, "end": v(24.7, 16.77) * mm});
            skLineSegment(sketch, "E2817", {"start": v(24.7, 16.77) * mm, "end": v(24.4, 17.03) * mm});
            skLineSegment(sketch, "E2818", {"start": v(24.4, 17.03) * mm, "end": v(24.26, 17.14) * mm});
            skLineSegment(sketch, "E2819", {"start": v(24.26, 17.14) * mm, "end": v(24.12, 17.24) * mm});
            skLineSegment(sketch, "E2820", {"start": v(24.12, 17.24) * mm, "end": v(23.7, 17.51) * mm});
            skLineSegment(sketch, "E2821", {"start": v(23.7, 17.51) * mm, "end": v(23.29, 17.77) * mm});
            skLineSegment(sketch, "E2822", {"start": v(23.29, 17.77) * mm, "end": v(22.87, 18.02) * mm});
            skLineSegment(sketch, "E2823", {"start": v(22.87, 18.02) * mm, "end": v(22.46, 18.26) * mm});
            skLineSegment(sketch, "E2824", {"start": v(22.46, 18.26) * mm, "end": v(22.06, 18.48) * mm});
            skLineSegment(sketch, "E2825", {"start": v(22.06, 18.48) * mm, "end": v(21.66, 18.7) * mm});
            skLineSegment(sketch, "E2826", {"start": v(21.66, 18.7) * mm, "end": v(21.26, 18.9) * mm});
            skLineSegment(sketch, "E2827", {"start": v(21.26, 18.9) * mm, "end": v(20.87, 19.08) * mm});
            skLineSegment(sketch, "E2828", {"start": v(20.87, 19.08) * mm, "end": v(20.48, 19.25) * mm});
            skLineSegment(sketch, "E2829", {"start": v(20.48, 19.25) * mm, "end": v(20.1, 19.42) * mm});
            skLineSegment(sketch, "E2830", {"start": v(20.1, 19.42) * mm, "end": v(19.71, 19.57) * mm});
            skLineSegment(sketch, "E2831", {"start": v(19.71, 19.57) * mm, "end": v(19.34, 19.7) * mm});
            skLineSegment(sketch, "E2832", {"start": v(19.34, 19.7) * mm, "end": v(18.96, 19.84) * mm});
            skLineSegment(sketch, "E2833", {"start": v(18.96, 19.84) * mm, "end": v(18.6, 19.96) * mm});
            skLineSegment(sketch, "E2834", {"start": v(18.6, 19.96) * mm, "end": v(18.22, 20.07) * mm});
            skLineSegment(sketch, "E2835", {"start": v(18.22, 20.07) * mm, "end": v(17.86, 20.16) * mm});
            skLineSegment(sketch, "E2836", {"start": v(17.86, 20.16) * mm, "end": v(17.5, 20.25) * mm});
            skLineSegment(sketch, "E2837", {"start": v(17.5, 20.25) * mm, "end": v(17.14, 20.33) * mm});
            skLineSegment(sketch, "E2838", {"start": v(17.14, 20.33) * mm, "end": v(16.78, 20.4) * mm});
            skLineSegment(sketch, "E2839", {"start": v(16.78, 20.4) * mm, "end": v(16.43, 20.45) * mm});
            skLineSegment(sketch, "E2840", {"start": v(16.43, 20.45) * mm, "end": v(16.08, 20.5) * mm});
            skLineSegment(sketch, "E2841", {"start": v(16.08, 20.5) * mm, "end": v(15.73, 20.53) * mm});
            skLineSegment(sketch, "E2842", {"start": v(15.73, 20.53) * mm, "end": v(15.38, 20.56) * mm});
            skLineSegment(sketch, "E2843", {"start": v(15.38, 20.56) * mm, "end": v(15.04, 20.58) * mm});
            skLineSegment(sketch, "E2844", {"start": v(15.04, 20.58) * mm, "end": v(14.7, 20.58) * mm});
            skLineSegment(sketch, "E2845", {"start": v(14.7, 20.58) * mm, "end": v(14.36, 20.58) * mm});
            skLineSegment(sketch, "E2846", {"start": v(14.36, 20.58) * mm, "end": v(14.03, 20.57) * mm});
            skLineSegment(sketch, "E2847", {"start": v(14.03, 20.57) * mm, "end": v(13.7, 20.56) * mm});
            skLineSegment(sketch, "E2848", {"start": v(13.7, 20.56) * mm, "end": v(13.36, 20.53) * mm});
            skLineSegment(sketch, "E2849", {"start": v(13.36, 20.53) * mm, "end": v(13.04, 20.5) * mm});
            skLineSegment(sketch, "E2850", {"start": v(13.04, 20.5) * mm, "end": v(12.7, 20.45) * mm});
            skLineSegment(sketch, "E2851", {"start": v(12.7, 20.45) * mm, "end": v(12.38, 20.4) * mm});
            skLineSegment(sketch, "E2852", {"start": v(12.38, 20.4) * mm, "end": v(12.06, 20.34) * mm});
            skLineSegment(sketch, "E2853", {"start": v(12.06, 20.34) * mm, "end": v(11.74, 20.28) * mm});
            skLineSegment(sketch, "E2854", {"start": v(11.74, 20.28) * mm, "end": v(11.1, 20.12) * mm});
            skLineSegment(sketch, "E2855", {"start": v(11.1, 20.12) * mm, "end": v(10.47, 19.93) * mm});
            skLineSegment(sketch, "E2856", {"start": v(10.47, 19.93) * mm, "end": v(9.84, 19.72) * mm});
            skLineSegment(sketch, "E2857", {"start": v(9.84, 19.72) * mm, "end": v(9.22, 19.48) * mm});
            skLineSegment(sketch, "E2858", {"start": v(9.22, 19.48) * mm, "end": v(8.6, 19.22) * mm});
            skLineSegment(sketch, "E2859", {"start": v(8.6, 19.22) * mm, "end": v(7.98, 18.93) * mm});
            skLineSegment(sketch, "E2860", {"start": v(7.98, 18.93) * mm, "end": v(7.37, 18.62) * mm});
            skLineSegment(sketch, "E2861", {"start": v(7.37, 18.62) * mm, "end": v(6.75, 18.3) * mm});
            skLineSegment(sketch, "E2862", {"start": v(6.75, 18.3) * mm, "end": v(6.14, 17.94) * mm});
            skLineSegment(sketch, "E2863", {"start": v(6.14, 17.94) * mm, "end": v(5.53, 17.57) * mm});
            skLineSegment(sketch, "E2864", {"start": v(5.53, 17.57) * mm, "end": v(4.92, 17.19) * mm});
            skLineSegment(sketch, "E2865", {"start": v(4.92, 17.19) * mm, "end": v(4.31, 16.79) * mm});
            skLineSegment(sketch, "E2866", {"start": v(4.31, 16.79) * mm, "end": v(3.7, 16.37) * mm});
            skLineSegment(sketch, "E2867", {"start": v(3.7, 16.37) * mm, "end": v(3.09, 15.94) * mm});
            skLineSegment(sketch, "E2868", {"start": v(3.09, 15.94) * mm, "end": v(2.47, 15.5) * mm});
            skLineSegment(sketch, "E2869", {"start": v(-35.5, -0.68) * mm, "end": v(-6.87, -15.93) * mm});
            skLineSegment(sketch, "E2870", {"start": v(-6.87, -15.93) * mm, "end": v(-6.78, -15.8) * mm});
            skLineSegment(sketch, "E2871", {"start": v(-6.78, -15.8) * mm, "end": v(-6.65, -15.59) * mm});
            skLineSegment(sketch, "E2872", {"start": v(-6.65, -15.59) * mm, "end": v(-6.3, -14.97) * mm});
            skLineSegment(sketch, "E2873", {"start": v(-6.3, -14.97) * mm, "end": v(-5.84, -14.13) * mm});
            skLineSegment(sketch, "E2874", {"start": v(-5.84, -14.13) * mm, "end": v(-5.3, -13.09) * mm});
            skLineSegment(sketch, "E2875", {"start": v(-5.3, -13.09) * mm, "end": v(-4.7, -11.9) * mm});
            skLineSegment(sketch, "E2876", {"start": v(-4.7, -11.9) * mm, "end": v(-4.04, -10.58) * mm});
            skLineSegment(sketch, "E2877", {"start": v(-4.04, -10.58) * mm, "end": v(-2.65, -7.76) * mm});
            skLineSegment(sketch, "E2878", {"start": v(-2.65, -7.76) * mm, "end": v(-1.28, -4.9) * mm});
            skLineSegment(sketch, "E2879", {"start": v(-1.28, -4.9) * mm, "end": v(-0.65, -3.57) * mm});
            skLineSegment(sketch, "E2880", {"start": v(-0.65, -3.57) * mm, "end": v(-0.08, -2.34) * mm});
            skLineSegment(sketch, "E2881", {"start": v(-0.08, -2.34) * mm, "end": v(0.4, -1.26) * mm});
            skLineSegment(sketch, "E2882", {"start": v(0.4, -1.26) * mm, "end": v(0.8, -0.36) * mm});
            skLineSegment(sketch, "E2883", {"start": v(0.8, -0.36) * mm, "end": v(1.08, 0.32) * mm});
            skLineSegment(sketch, "E2884", {"start": v(1.08, 0.32) * mm, "end": v(1.17, 0.57) * mm});
            skLineSegment(sketch, "E2885", {"start": v(1.17, 0.57) * mm, "end": v(1.22, 0.75) * mm});
            skLineSegment(sketch, "E2886", {"start": v(1.22, 0.75) * mm, "end": v(1.31, 1.13) * mm});
            skLineSegment(sketch, "E2887", {"start": v(1.31, 1.13) * mm, "end": v(1.4, 1.51) * mm});
            skLineSegment(sketch, "E2888", {"start": v(1.4, 1.51) * mm, "end": v(1.46, 1.9) * mm});
            skLineSegment(sketch, "E2889", {"start": v(1.46, 1.9) * mm, "end": v(1.53, 2.27) * mm});
            skLineSegment(sketch, "E2890", {"start": v(1.53, 2.27) * mm, "end": v(1.58, 2.64) * mm});
            skLineSegment(sketch, "E2891", {"start": v(1.58, 2.64) * mm, "end": v(1.62, 3.01) * mm});
            skLineSegment(sketch, "E2892", {"start": v(1.62, 3.01) * mm, "end": v(1.66, 3.38) * mm});
            skLineSegment(sketch, "E2893", {"start": v(1.66, 3.38) * mm, "end": v(1.69, 3.75) * mm});
            skLineSegment(sketch, "E2894", {"start": v(1.69, 3.75) * mm, "end": v(1.7, 4.12) * mm});
            skLineSegment(sketch, "E2895", {"start": v(1.7, 4.12) * mm, "end": v(1.71, 4.48) * mm});
            skLineSegment(sketch, "E2896", {"start": v(1.71, 4.48) * mm, "end": v(1.71, 4.84) * mm});
            skLineSegment(sketch, "E2897", {"start": v(1.71, 4.84) * mm, "end": v(1.7, 5.2) * mm});
            skLineSegment(sketch, "E2898", {"start": v(1.7, 5.2) * mm, "end": v(1.69, 5.55) * mm});
            skLineSegment(sketch, "E2899", {"start": v(1.69, 5.55) * mm, "end": v(1.66, 5.9) * mm});
            skLineSegment(sketch, "E2900", {"start": v(1.66, 5.9) * mm, "end": v(1.63, 6.24) * mm});
            skLineSegment(sketch, "E2901", {"start": v(1.63, 6.24) * mm, "end": v(1.6, 6.59) * mm});
            skLineSegment(sketch, "E2902", {"start": v(1.6, 6.59) * mm, "end": v(1.55, 6.93) * mm});
            skLineSegment(sketch, "E2903", {"start": v(1.55, 6.93) * mm, "end": v(1.5, 7.27) * mm});
            skLineSegment(sketch, "E2904", {"start": v(1.5, 7.27) * mm, "end": v(1.36, 7.93) * mm});
            skLineSegment(sketch, "E2905", {"start": v(1.36, 7.93) * mm, "end": v(1.2, 8.58) * mm});
            skLineSegment(sketch, "E2906", {"start": v(1.2, 8.58) * mm, "end": v(1.02, 9.22) * mm});
            skLineSegment(sketch, "E2907", {"start": v(1.02, 9.22) * mm, "end": v(0.81, 9.85) * mm});
            skLineSegment(sketch, "E2908", {"start": v(0.81, 9.85) * mm, "end": v(0.58, 10.46) * mm});
            skLineSegment(sketch, "E2909", {"start": v(0.58, 10.46) * mm, "end": v(0.32, 11.05) * mm});
            skLineSegment(sketch, "E2910", {"start": v(0.32, 11.05) * mm, "end": v(0.04, 11.63) * mm});
            skLineSegment(sketch, "E2911", {"start": v(0.04, 11.63) * mm, "end": v(-0.25, 12.2) * mm});
            skLineSegment(sketch, "E2912", {"start": v(-0.25, 12.2) * mm, "end": v(-0.57, 12.74) * mm});
            skLineSegment(sketch, "E2913", {"start": v(-0.57, 12.74) * mm, "end": v(-0.9, 13.27) * mm});
            skLineSegment(sketch, "E2914", {"start": v(-0.9, 13.27) * mm, "end": v(-1.26, 13.78) * mm});
            skLineSegment(sketch, "E2915", {"start": v(-1.26, 13.78) * mm, "end": v(-1.63, 14.28) * mm});
            skLineSegment(sketch, "E2916", {"start": v(-1.63, 14.28) * mm, "end": v(-2, 14.75) * mm});
            skLineSegment(sketch, "E2917", {"start": v(-2, 14.75) * mm, "end": v(-2.4, 15.2) * mm});
            skLineSegment(sketch, "E2918", {"start": v(-2.4, 15.2) * mm, "end": v(-2.8, 15.65) * mm});
            skLineSegment(sketch, "E2919", {"start": v(-2.8, 15.65) * mm, "end": v(-3.23, 16.06) * mm});
            skLineSegment(sketch, "E2920", {"start": v(-3.23, 16.06) * mm, "end": v(-3.65, 16.46) * mm});
            skLineSegment(sketch, "E2921", {"start": v(-3.65, 16.46) * mm, "end": v(-4.09, 16.84) * mm});
            skLineSegment(sketch, "E2922", {"start": v(-4.09, 16.84) * mm, "end": v(-4.53, 17.19) * mm});
            skLineSegment(sketch, "E2923", {"start": v(-4.53, 17.19) * mm, "end": v(-4.98, 17.52) * mm});
            skLineSegment(sketch, "E2924", {"start": v(-4.98, 17.52) * mm, "end": v(-5.43, 17.83) * mm});
            skLineSegment(sketch, "E2925", {"start": v(-5.43, 17.83) * mm, "end": v(-5.89, 18.12) * mm});
            skLineSegment(sketch, "E2926", {"start": v(-5.89, 18.12) * mm, "end": v(-6.35, 18.39) * mm});
            skLineSegment(sketch, "E2927", {"start": v(-6.35, 18.39) * mm, "end": v(-6.66, 18.55) * mm});
            skLineSegment(sketch, "E2928", {"start": v(-6.66, 18.55) * mm, "end": v(-6.98, 18.71) * mm});
            skLineSegment(sketch, "E2929", {"start": v(-6.98, 18.71) * mm, "end": v(-7.3, 18.86) * mm});
            skLineSegment(sketch, "E2930", {"start": v(-7.3, 18.86) * mm, "end": v(-7.63, 19) * mm});
            skLineSegment(sketch, "E2931", {"start": v(-7.63, 19) * mm, "end": v(-7.95, 19.14) * mm});
            skLineSegment(sketch, "E2932", {"start": v(-7.95, 19.14) * mm, "end": v(-8.28, 19.27) * mm});
            skLineSegment(sketch, "E2933", {"start": v(-8.28, 19.27) * mm, "end": v(-8.6, 19.38) * mm});
            skLineSegment(sketch, "E2934", {"start": v(-8.6, 19.38) * mm, "end": v(-8.94, 19.5) * mm});
            skLineSegment(sketch, "E2935", {"start": v(-8.94, 19.5) * mm, "end": v(-9.27, 19.6) * mm});
            skLineSegment(sketch, "E2936", {"start": v(-9.27, 19.6) * mm, "end": v(-9.6, 19.69) * mm});
            skLineSegment(sketch, "E2937", {"start": v(-9.6, 19.69) * mm, "end": v(-9.94, 19.78) * mm});
            skLineSegment(sketch, "E2938", {"start": v(-9.94, 19.78) * mm, "end": v(-10.28, 19.85) * mm});
            skLineSegment(sketch, "E2939", {"start": v(-10.28, 19.85) * mm, "end": v(-10.95, 19.99) * mm});
            skLineSegment(sketch, "E2940", {"start": v(-10.95, 19.99) * mm, "end": v(-11.63, 20.1) * mm});
            skLineSegment(sketch, "E2941", {"start": v(-11.63, 20.1) * mm, "end": v(-12.31, 20.17) * mm});
            skLineSegment(sketch, "E2942", {"start": v(-12.31, 20.17) * mm, "end": v(-13, 20.22) * mm});
            skLineSegment(sketch, "E2943", {"start": v(-13, 20.22) * mm, "end": v(-13.68, 20.24) * mm});
            skLineSegment(sketch, "E2944", {"start": v(-13.68, 20.24) * mm, "end": v(-14.35, 20.23) * mm});
            skLineSegment(sketch, "E2945", {"start": v(-14.35, 20.23) * mm, "end": v(-15.03, 20.2) * mm});
            skLineSegment(sketch, "E2946", {"start": v(-15.03, 20.2) * mm, "end": v(-15.7, 20.14) * mm});
            skLineSegment(sketch, "E2947", {"start": v(-15.7, 20.14) * mm, "end": v(-16.37, 20.06) * mm});
            skLineSegment(sketch, "E2948", {"start": v(-16.37, 20.06) * mm, "end": v(-17.03, 19.96) * mm});
            skLineSegment(sketch, "E2949", {"start": v(-17.03, 19.96) * mm, "end": v(-17.68, 19.83) * mm});
            skLineSegment(sketch, "E2950", {"start": v(-17.68, 19.83) * mm, "end": v(-18.32, 19.68) * mm});
            skLineSegment(sketch, "E2951", {"start": v(-18.32, 19.68) * mm, "end": v(-18.95, 19.52) * mm});
            skLineSegment(sketch, "E2952", {"start": v(-18.95, 19.52) * mm, "end": v(-19.57, 19.33) * mm});
            skLineSegment(sketch, "E2953", {"start": v(-19.57, 19.33) * mm, "end": v(-20.18, 19.12) * mm});
            skLineSegment(sketch, "E2954", {"start": v(-20.18, 19.12) * mm, "end": v(-20.77, 18.9) * mm});
            skLineSegment(sketch, "E2955", {"start": v(-20.77, 18.9) * mm, "end": v(-21.35, 18.65) * mm});
            skLineSegment(sketch, "E2956", {"start": v(-21.35, 18.65) * mm, "end": v(-21.91, 18.39) * mm});
            skLineSegment(sketch, "E2957", {"start": v(-21.91, 18.39) * mm, "end": v(-22.45, 18.11) * mm});
            skLineSegment(sketch, "E2958", {"start": v(-22.45, 18.11) * mm, "end": v(-22.98, 17.82) * mm});
            skLineSegment(sketch, "E2959", {"start": v(-22.98, 17.82) * mm, "end": v(-23.49, 17.51) * mm});
            skLineSegment(sketch, "E2960", {"start": v(-23.49, 17.51) * mm, "end": v(-23.97, 17.2) * mm});
            skLineSegment(sketch, "E2961", {"start": v(-23.97, 17.2) * mm, "end": v(-24.43, 16.86) * mm});
            skLineSegment(sketch, "E2962", {"start": v(-24.43, 16.86) * mm, "end": v(-24.87, 16.52) * mm});
            skLineSegment(sketch, "E2963", {"start": v(-24.87, 16.52) * mm, "end": v(-25.28, 16.16) * mm});
            skLineSegment(sketch, "E2964", {"start": v(-25.28, 16.16) * mm, "end": v(-25.67, 15.8) * mm});
            skLineSegment(sketch, "E2965", {"start": v(-25.67, 15.8) * mm, "end": v(-26, 15.43) * mm});
            skLineSegment(sketch, "E2966", {"start": v(-26, 15.43) * mm, "end": v(-26.34, 15.05) * mm});
            skLineSegment(sketch, "E2967", {"start": v(-26.34, 15.05) * mm, "end": v(-26.66, 14.63) * mm});
            skLineSegment(sketch, "E2968", {"start": v(-26.66, 14.63) * mm, "end": v(-26.97, 14.2) * mm});
            skLineSegment(sketch, "E2969", {"start": v(-26.97, 14.2) * mm, "end": v(-27.28, 13.74) * mm});
            skLineSegment(sketch, "E2970", {"start": v(-27.28, 13.74) * mm, "end": v(-27.58, 13.26) * mm});
            skLineSegment(sketch, "E2971", {"start": v(-27.58, 13.26) * mm, "end": v(-27.87, 12.76) * mm});
            skLineSegment(sketch, "E2972", {"start": v(-27.87, 12.76) * mm, "end": v(-28.16, 12.25) * mm});
            skLineSegment(sketch, "E2973", {"start": v(-28.16, 12.25) * mm, "end": v(-28.74, 11.2) * mm});
            skLineSegment(sketch, "E2974", {"start": v(-28.74, 11.2) * mm, "end": v(-29.3, 10.11) * mm});
            skLineSegment(sketch, "E2975", {"start": v(-29.3, 10.11) * mm, "end": v(-29.88, 9.02) * mm});
            skLineSegment(sketch, "E2976", {"start": v(-29.88, 9.02) * mm, "end": v(-30.47, 7.94) * mm});
            skLineSegment(sketch, "E2977", {"start": v(-30.47, 7.94) * mm, "end": v(-30.79, 7.38) * mm});
            skLineSegment(sketch, "E2978", {"start": v(-30.79, 7.38) * mm, "end": v(-31.11, 6.81) * mm});
            skLineSegment(sketch, "E2979", {"start": v(-31.11, 6.81) * mm, "end": v(-31.8, 5.68) * mm});
            skLineSegment(sketch, "E2980", {"start": v(-31.8, 5.68) * mm, "end": v(-32.49, 4.56) * mm});
            skLineSegment(sketch, "E2981", {"start": v(-32.49, 4.56) * mm, "end": v(-33.18, 3.45) * mm});
            skLineSegment(sketch, "E2982", {"start": v(-33.18, 3.45) * mm, "end": v(-33.84, 2.37) * mm});
            skLineSegment(sketch, "E2983", {"start": v(-33.84, 2.37) * mm, "end": v(-34.46, 1.3) * mm});
            skLineSegment(sketch, "E2984", {"start": v(-34.46, 1.3) * mm, "end": v(-34.75, 0.8) * mm});
            skLineSegment(sketch, "E2985", {"start": v(-34.75, 0.8) * mm, "end": v(-35.02, 0.3) * mm});
            skLineSegment(sketch, "E2986", {"start": v(-35.02, 0.3) * mm, "end": v(-35.27, -0.2) * mm});
            skLineSegment(sketch, "E2987", {"start": v(-35.27, -0.2) * mm, "end": v(-35.5, -0.68) * mm});
            skSolve(sketch);
        }
        {
            var Q0;
            Q0=makeQuery(id+"F0.imprint","IMPRINT",FACE,{"disambiguationData":[TD([[makeQuery(id+"F0.imprint","IMPRINT",EDGE,{"derivedFrom":sQuery(id+"F0.wireOp",EDGE,"E0")}),-1.0]])]});
            extrude(context, id + "F1", {"entities" : qUnion([Q0]), "depth" : 3 * mm});
        }
    });
